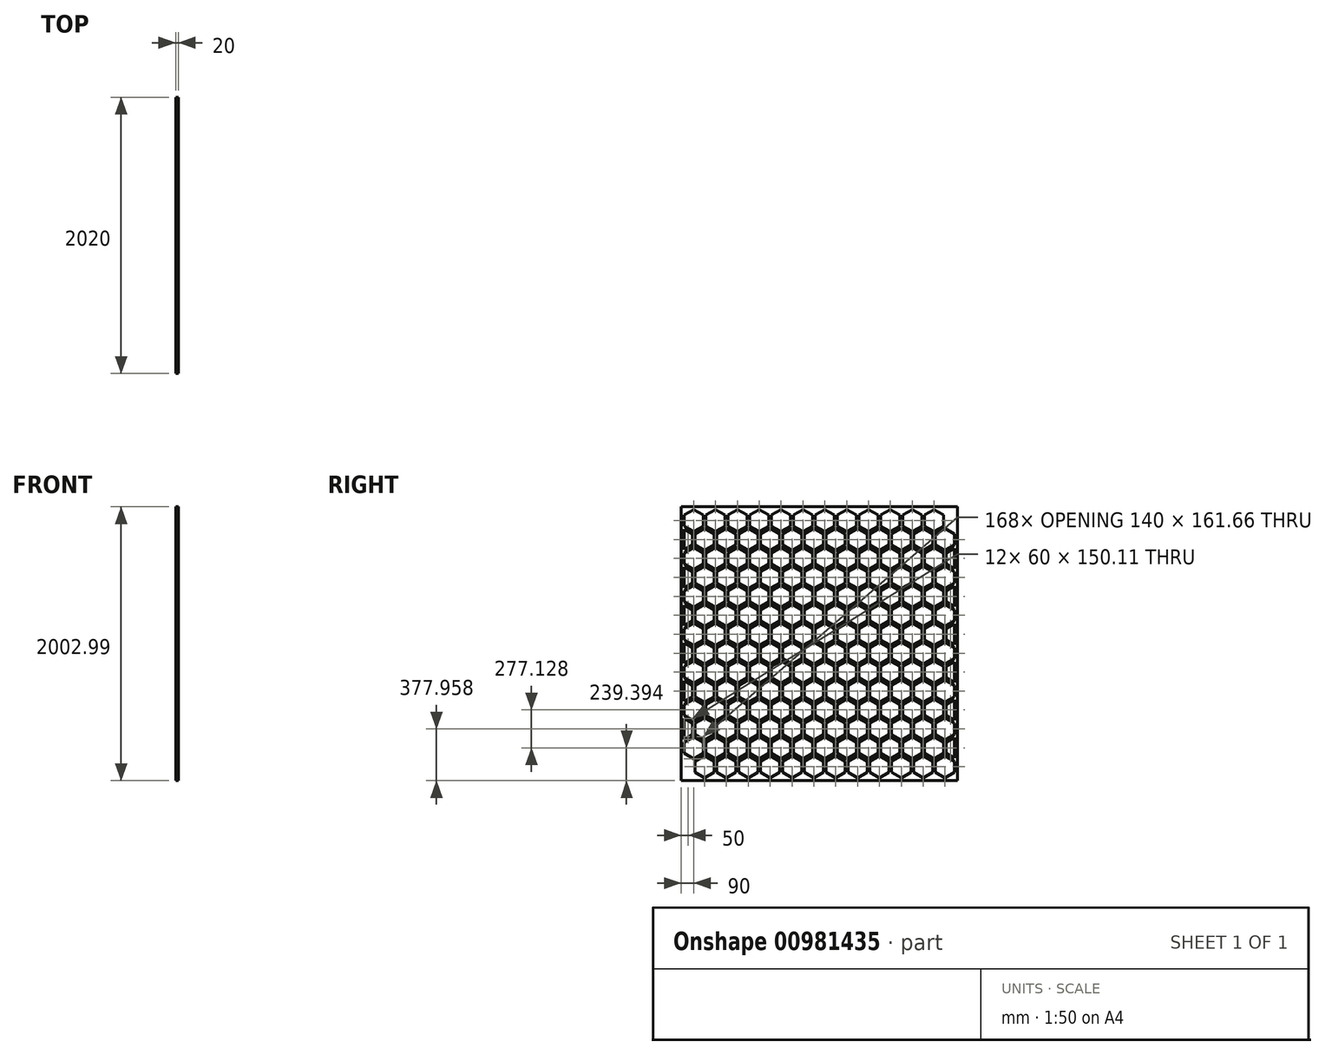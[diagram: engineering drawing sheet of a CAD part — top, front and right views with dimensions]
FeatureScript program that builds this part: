
annotation { "Feature Type Name" : "Feature", "Feature Type Description" : "" }
export const myFeature = defineFeature(function(context is Context, id is Id, definition is map)
    precondition{}
    {
        {
            var Q0;
            Q0=qCreatedBy(makeId("Right.planeOp"),FACE);
            var sketch = newSketch(context, id + "F0", { "sketchPlane" : qUnion([Q0])});
            skLineSegment(sketch, "E0", {"start": v(0, -80.83) * mm, "end": v(-70, -40.41) * mm});
            skLineSegment(sketch, "E1", {"start": v(-70, -40.41) * mm, "end": v(-70, 40.41) * mm});
            skLineSegment(sketch, "E2", {"start": v(-70, 40.41) * mm, "end": v(0, 80.83) * mm});
            skLineSegment(sketch, "E3", {"start": v(0, 80.83) * mm, "end": v(70, 40.41) * mm});
            skLineSegment(sketch, "E4", {"start": v(70, 40.41) * mm, "end": v(70, -40.41) * mm});
            skLineSegment(sketch, "E5", {"start": v(70, -40.41) * mm, "end": v(0, -80.83) * mm});
            skLineSegment(sketch, "E6.MirrorCS", {"start": v(10, 98.15) * mm, "end": v(80, 57.74) * mm});
            skLineSegment(sketch, "E7.MirrorCS", {"start": v(80, 57.74) * mm, "end": v(150, 98.15) * mm});
            skLineSegment(sketch, "E8.MirrorCS", {"start": v(80, 219.4) * mm, "end": v(10, 178.98) * mm});
            skLineSegment(sketch, "E9.MirrorCS", {"start": v(150, 178.98) * mm, "end": v(80, 219.4) * mm});
            skLineSegment(sketch, "E10.MirrorCS", {"start": v(150, 98.15) * mm, "end": v(150, 178.98) * mm});
            skLineSegment(sketch, "E11.MirrorCS", {"start": v(10, 178.98) * mm, "end": v(10, 98.15) * mm});
            skLineSegment(sketch, "E12.MirrorCS", {"start": v(160, -80.83) * mm, "end": v(230, -40.41) * mm});
            skLineSegment(sketch, "E13.MirrorCS", {"start": v(90, 40.41) * mm, "end": v(90, -40.41) * mm});
            skLineSegment(sketch, "E14.MirrorCS", {"start": v(230, 40.41) * mm, "end": v(160, 80.83) * mm});
            skLineSegment(sketch, "E15.MirrorCS", {"start": v(230, -40.41) * mm, "end": v(230, 40.41) * mm});
            skLineSegment(sketch, "E16.MirrorCS", {"start": v(160, 80.83) * mm, "end": v(90, 40.41) * mm});
            skLineSegment(sketch, "E17.MirrorCS", {"start": v(90, -40.41) * mm, "end": v(160, -80.83) * mm});
            skLineSegment(sketch, "E18.MirrorCS", {"start": v(410, 40.41) * mm, "end": v(410, -40.41) * mm});
            skLineSegment(sketch, "E19.MirrorCS", {"start": v(400, 57.74) * mm, "end": v(330, 98.15) * mm});
            skLineSegment(sketch, "E20.MirrorCS", {"start": v(320, 80.83) * mm, "end": v(390, 40.41) * mm});
            skLineSegment(sketch, "E21.MirrorCS", {"start": v(480, 80.83) * mm, "end": v(410, 40.41) * mm});
            skLineSegment(sketch, "E22.MirrorCS", {"start": v(320, -80.83) * mm, "end": v(250, -40.41) * mm});
            skLineSegment(sketch, "E23.MirrorCS", {"start": v(390, 40.41) * mm, "end": v(390, -40.41) * mm});
            skLineSegment(sketch, "E24.MirrorCS", {"start": v(250, -40.41) * mm, "end": v(250, 40.41) * mm});
            skLineSegment(sketch, "E25.MirrorCS", {"start": v(480, -80.83) * mm, "end": v(550, -40.41) * mm});
            skLineSegment(sketch, "E26.MirrorCS", {"start": v(330, 178.98) * mm, "end": v(400, 219.4) * mm});
            skLineSegment(sketch, "E27.MirrorCS", {"start": v(550, 40.41) * mm, "end": v(480, 80.83) * mm});
            skLineSegment(sketch, "E28.MirrorCS", {"start": v(470, 178.98) * mm, "end": v(470, 98.15) * mm});
            skLineSegment(sketch, "E29.MirrorCS", {"start": v(550, -40.41) * mm, "end": v(550, 40.41) * mm});
            skLineSegment(sketch, "E30.MirrorCS", {"start": v(390, -40.41) * mm, "end": v(320, -80.83) * mm});
            skLineSegment(sketch, "E31.MirrorCS", {"start": v(410, -40.41) * mm, "end": v(480, -80.83) * mm});
            skLineSegment(sketch, "E32.MirrorCS", {"start": v(250, 40.41) * mm, "end": v(320, 80.83) * mm});
            skLineSegment(sketch, "E33.MirrorCS", {"start": v(470, 98.15) * mm, "end": v(400, 57.74) * mm});
            skLineSegment(sketch, "E34.MirrorCS", {"start": v(330, 98.15) * mm, "end": v(330, 178.98) * mm});
            skLineSegment(sketch, "E35.MirrorCS", {"start": v(400, 219.4) * mm, "end": v(470, 178.98) * mm});
            skLineSegment(sketch, "E36.MirrorCS", {"start": v(1120, -80.83) * mm, "end": v(1190, -40.41) * mm});
            skLineSegment(sketch, "E37.MirrorCS", {"start": v(870, 40.41) * mm, "end": v(800, 80.83) * mm});
            skLineSegment(sketch, "E38.MirrorCS", {"start": v(800, 80.83) * mm, "end": v(730, 40.41) * mm});
            skLineSegment(sketch, "E39.MirrorCS", {"start": v(640, 80.83) * mm, "end": v(710, 40.41) * mm});
            skLineSegment(sketch, "E40.MirrorCS", {"start": v(790, 178.98) * mm, "end": v(720, 219.4) * mm});
            skLineSegment(sketch, "E41.MirrorCS", {"start": v(960, -80.83) * mm, "end": v(890, -40.41) * mm});
            skLineSegment(sketch, "E42.MirrorCS", {"start": v(570, 40.41) * mm, "end": v(640, 80.83) * mm});
            skLineSegment(sketch, "E43.MirrorCS", {"start": v(1120, 80.83) * mm, "end": v(1050, 40.41) * mm});
            skLineSegment(sketch, "E44.MirrorCS", {"start": v(970, 178.98) * mm, "end": v(1040, 219.4) * mm});
            skLineSegment(sketch, "E45.MirrorCS", {"start": v(650, 98.15) * mm, "end": v(720, 57.74) * mm});
            skLineSegment(sketch, "E46.MirrorCS", {"start": v(710, 40.41) * mm, "end": v(710, -40.41) * mm});
            skLineSegment(sketch, "E47.MirrorCS", {"start": v(1030, 40.41) * mm, "end": v(1030, -40.41) * mm});
            skLineSegment(sketch, "E48.MirrorCS", {"start": v(720, 219.4) * mm, "end": v(650, 178.98) * mm});
            skLineSegment(sketch, "E49.MirrorCS", {"start": v(890, -40.41) * mm, "end": v(890, 40.41) * mm});
            skLineSegment(sketch, "E50.MirrorCS", {"start": v(570, -40.41) * mm, "end": v(570, 40.41) * mm});
            skLineSegment(sketch, "E51.MirrorCS", {"start": v(1110, 98.15) * mm, "end": v(1040, 57.74) * mm});
            skLineSegment(sketch, "E52.MirrorCS", {"start": v(870, -40.41) * mm, "end": v(870, 40.41) * mm});
            skLineSegment(sketch, "E53.MirrorCS", {"start": v(1040, 57.74) * mm, "end": v(970, 98.15) * mm});
            skLineSegment(sketch, "E54.MirrorCS", {"start": v(890, 40.41) * mm, "end": v(960, 80.83) * mm});
            skLineSegment(sketch, "E55.MirrorCS", {"start": v(970, 98.15) * mm, "end": v(970, 178.98) * mm});
            skLineSegment(sketch, "E56.MirrorCS", {"start": v(730, -40.41) * mm, "end": v(800, -80.83) * mm});
            skLineSegment(sketch, "E57.MirrorCS", {"start": v(1110, 178.98) * mm, "end": v(1110, 98.15) * mm});
            skLineSegment(sketch, "E58.MirrorCS", {"start": v(790, 98.15) * mm, "end": v(790, 178.98) * mm});
            skLineSegment(sketch, "E59.MirrorCS", {"start": v(650, 178.98) * mm, "end": v(650, 98.15) * mm});
            skLineSegment(sketch, "E60.MirrorCS", {"start": v(1190, -40.41) * mm, "end": v(1190, 40.41) * mm});
            skLineSegment(sketch, "E61.MirrorCS", {"start": v(1190, 40.41) * mm, "end": v(1120, 80.83) * mm});
            skLineSegment(sketch, "E62.MirrorCS", {"start": v(960, 80.83) * mm, "end": v(1030, 40.41) * mm});
            skLineSegment(sketch, "E63.MirrorCS", {"start": v(710, -40.41) * mm, "end": v(640, -80.83) * mm});
            skLineSegment(sketch, "E64.MirrorCS", {"start": v(1030, -40.41) * mm, "end": v(960, -80.83) * mm});
            skLineSegment(sketch, "E65.MirrorCS", {"start": v(640, -80.83) * mm, "end": v(570, -40.41) * mm});
            skLineSegment(sketch, "E66.MirrorCS", {"start": v(730, 40.41) * mm, "end": v(730, -40.41) * mm});
            skLineSegment(sketch, "E67.MirrorCS", {"start": v(1050, -40.41) * mm, "end": v(1120, -80.83) * mm});
            skLineSegment(sketch, "E68.MirrorCS", {"start": v(720, 57.74) * mm, "end": v(790, 98.15) * mm});
            skLineSegment(sketch, "E69.MirrorCS", {"start": v(800, -80.83) * mm, "end": v(870, -40.41) * mm});
            skLineSegment(sketch, "E70.MirrorCS", {"start": v(1040, 219.4) * mm, "end": v(1110, 178.98) * mm});
            skLineSegment(sketch, "E71.MirrorCS", {"start": v(1050, 40.41) * mm, "end": v(1050, -40.41) * mm});
            skLineSegment(sketch, "E72.MirrorCS", {"start": v(-640, -80.83) * mm, "end": v(-710, -40.41) * mm});
            skLineSegment(sketch, "E73.MirrorCS", {"start": v(-710, 40.41) * mm, "end": v(-640, 80.83) * mm});
            skLineSegment(sketch, "E74.MirrorCS", {"start": v(-710, -40.41) * mm, "end": v(-710, 40.41) * mm});
            skLineSegment(sketch, "E75.MirrorCS", {"start": v(-160, 80.83) * mm, "end": v(-230, 40.41) * mm});
            skLineSegment(sketch, "E76.MirrorCS", {"start": v(-160, -80.83) * mm, "end": v(-90, -40.41) * mm});
            skLineSegment(sketch, "E77.MirrorCS", {"start": v(-250, -40.41) * mm, "end": v(-320, -80.83) * mm});
            skLineSegment(sketch, "E78.MirrorCS", {"start": v(-480, 80.83) * mm, "end": v(-550, 40.41) * mm});
            skLineSegment(sketch, "E79.MirrorCS", {"start": v(-490, 178.98) * mm, "end": v(-560, 219.4) * mm});
            skLineSegment(sketch, "E80.MirrorCS", {"start": v(-630, 98.15) * mm, "end": v(-560, 57.74) * mm});
            skLineSegment(sketch, "E81.MirrorCS", {"start": v(-570, -40.41) * mm, "end": v(-640, -80.83) * mm});
            skLineSegment(sketch, "E82.MirrorCS", {"start": v(-90, -40.41) * mm, "end": v(-90, 40.41) * mm});
            skLineSegment(sketch, "E83.MirrorCS", {"start": v(-630, 178.98) * mm, "end": v(-630, 98.15) * mm});
            skLineSegment(sketch, "E84.MirrorCS", {"start": v(-320, -80.83) * mm, "end": v(-390, -40.41) * mm});
            skLineSegment(sketch, "E85.MirrorCS", {"start": v(-480, -80.83) * mm, "end": v(-410, -40.41) * mm});
            skLineSegment(sketch, "E86.MirrorCS", {"start": v(-490, 98.15) * mm, "end": v(-490, 178.98) * mm});
            skLineSegment(sketch, "E87.MirrorCS", {"start": v(-570, 40.41) * mm, "end": v(-570, -40.41) * mm});
            skLineSegment(sketch, "E88.MirrorCS", {"start": v(-410, 40.41) * mm, "end": v(-480, 80.83) * mm});
            skLineSegment(sketch, "E89.MirrorCS", {"start": v(-170, 178.98) * mm, "end": v(-170, 98.15) * mm});
            skLineSegment(sketch, "E90.MirrorCS", {"start": v(-310, 178.98) * mm, "end": v(-240, 219.4) * mm});
            skLineSegment(sketch, "E91.MirrorCS", {"start": v(-230, 40.41) * mm, "end": v(-230, -40.41) * mm});
            skLineSegment(sketch, "E92.MirrorCS", {"start": v(-550, 40.41) * mm, "end": v(-550, -40.41) * mm});
            skLineSegment(sketch, "E93.MirrorCS", {"start": v(-390, 40.41) * mm, "end": v(-320, 80.83) * mm});
            skLineSegment(sketch, "E94.MirrorCS", {"start": v(-240, 219.4) * mm, "end": v(-170, 178.98) * mm});
            skLineSegment(sketch, "E95.MirrorCS", {"start": v(-560, 57.74) * mm, "end": v(-490, 98.15) * mm});
            skLineSegment(sketch, "E96.MirrorCS", {"start": v(-550, -40.41) * mm, "end": v(-480, -80.83) * mm});
            skLineSegment(sketch, "E97.MirrorCS", {"start": v(-250, 40.41) * mm, "end": v(-250, -40.41) * mm});
            skLineSegment(sketch, "E98.MirrorCS", {"start": v(-90, 40.41) * mm, "end": v(-160, 80.83) * mm});
            skLineSegment(sketch, "E99.MirrorCS", {"start": v(-230, -40.41) * mm, "end": v(-160, -80.83) * mm});
            skLineSegment(sketch, "E100.MirrorCS", {"start": v(-240, 57.74) * mm, "end": v(-310, 98.15) * mm});
            skLineSegment(sketch, "E101.MirrorCS", {"start": v(-310, 98.15) * mm, "end": v(-310, 178.98) * mm});
            skLineSegment(sketch, "E102.MirrorCS", {"start": v(-390, -40.41) * mm, "end": v(-390, 40.41) * mm});
            skLineSegment(sketch, "E103.MirrorCS", {"start": v(-170, 98.15) * mm, "end": v(-240, 57.74) * mm});
            skLineSegment(sketch, "E104.MirrorCS", {"start": v(-320, 80.83) * mm, "end": v(-250, 40.41) * mm});
            skLineSegment(sketch, "E105.MirrorCS", {"start": v(-560, 219.4) * mm, "end": v(-630, 178.98) * mm});
            skLineSegment(sketch, "E106.MirrorCS", {"start": v(-640, 80.83) * mm, "end": v(-570, 40.41) * mm});
            skLineSegment(sketch, "E107.MirrorCS", {"start": v(-410, -40.41) * mm, "end": v(-410, 40.41) * mm});
            skLineSegment(sketch, "E108.MirrorCS", {"start": v(-400, 57.74) * mm, "end": v(-470, 98.15) * mm});
            skLineSegment(sketch, "E109.MirrorCS", {"start": v(-330, 98.15) * mm, "end": v(-400, 57.74) * mm});
            skLineSegment(sketch, "E110.MirrorCS", {"start": v(-400, 219.4) * mm, "end": v(-330, 178.98) * mm});
            skLineSegment(sketch, "E111.MirrorCS", {"start": v(-470, 98.15) * mm, "end": v(-470, 178.98) * mm});
            skLineSegment(sketch, "E112.MirrorCS", {"start": v(-470, 178.98) * mm, "end": v(-400, 219.4) * mm});
            skLineSegment(sketch, "E113.MirrorCS", {"start": v(-330, 178.98) * mm, "end": v(-330, 98.15) * mm});
            skLineSegment(sketch, "E114.MirrorCS", {"start": v(310, 178.98) * mm, "end": v(310, 98.15) * mm});
            skLineSegment(sketch, "E115.MirrorCS", {"start": v(240, 219.4) * mm, "end": v(310, 178.98) * mm});
            skLineSegment(sketch, "E116.MirrorCS", {"start": v(240, 57.74) * mm, "end": v(170, 98.15) * mm});
            skLineSegment(sketch, "E117.MirrorCS", {"start": v(310, 98.15) * mm, "end": v(240, 57.74) * mm});
            skLineSegment(sketch, "E118.MirrorCS", {"start": v(170, 178.98) * mm, "end": v(240, 219.4) * mm});
            skLineSegment(sketch, "E119.MirrorCS", {"start": v(170, 98.15) * mm, "end": v(170, 178.98) * mm});
            skLineSegment(sketch, "E120.MirrorCS", {"start": v(-10, 98.15) * mm, "end": v(-10, 178.98) * mm});
            skLineSegment(sketch, "E121.MirrorCS", {"start": v(-80, 57.74) * mm, "end": v(-10, 98.15) * mm});
            skLineSegment(sketch, "E122.MirrorCS", {"start": v(-150, 98.15) * mm, "end": v(-80, 57.74) * mm});
            skLineSegment(sketch, "E123.MirrorCS", {"start": v(-150, 178.98) * mm, "end": v(-150, 98.15) * mm});
            skLineSegment(sketch, "E124.MirrorCS", {"start": v(-80, 219.4) * mm, "end": v(-150, 178.98) * mm});
            skLineSegment(sketch, "E125.MirrorCS", {"start": v(-10, 178.98) * mm, "end": v(-80, 219.4) * mm});
            skLineSegment(sketch, "E126.MirrorCS", {"start": v(-790, 178.98) * mm, "end": v(-790, 98.15) * mm});
            skLineSegment(sketch, "E127.MirrorCS", {"start": v(-720, 219.4) * mm, "end": v(-790, 178.98) * mm});
            skLineSegment(sketch, "E128.MirrorCS", {"start": v(-650, 178.98) * mm, "end": v(-720, 219.4) * mm});
            skLineSegment(sketch, "E129.MirrorCS", {"start": v(-650, 98.15) * mm, "end": v(-650, 178.98) * mm});
            skLineSegment(sketch, "E130.MirrorCS", {"start": v(-720, 57.74) * mm, "end": v(-650, 98.15) * mm});
            skLineSegment(sketch, "E131.MirrorCS", {"start": v(-790, 98.15) * mm, "end": v(-720, 57.74) * mm});
            skLineSegment(sketch, "E132.MirrorCS", {"start": v(1130, 98.15) * mm, "end": v(1190, 63.5) * mm});
            skLineSegment(sketch, "E133.MirrorCS", {"start": v(1130, 178.98) * mm, "end": v(1130, 98.15) * mm});
            skLineSegment(sketch, "E134.MirrorCS", {"start": v(1190, 213.62) * mm, "end": v(1130, 178.98) * mm});
            skLineSegment(sketch, "E135.MirrorCS", {"start": v(950, 178.98) * mm, "end": v(950, 98.15) * mm});
            skLineSegment(sketch, "E136.MirrorCS", {"start": v(880, 219.4) * mm, "end": v(950, 178.98) * mm});
            skLineSegment(sketch, "E137.MirrorCS", {"start": v(950, 98.15) * mm, "end": v(880, 57.74) * mm});
            skLineSegment(sketch, "E138.MirrorCS", {"start": v(880, 57.74) * mm, "end": v(810, 98.15) * mm});
            skLineSegment(sketch, "E139.MirrorCS", {"start": v(810, 98.15) * mm, "end": v(810, 178.98) * mm});
            skLineSegment(sketch, "E140.MirrorCS", {"start": v(810, 178.98) * mm, "end": v(880, 219.4) * mm});
            skLineSegment(sketch, "E141.MirrorCS", {"start": v(490, 98.15) * mm, "end": v(560, 57.74) * mm});
            skLineSegment(sketch, "E142.MirrorCS", {"start": v(560, 57.74) * mm, "end": v(630, 98.15) * mm});
            skLineSegment(sketch, "E143.MirrorCS", {"start": v(630, 98.15) * mm, "end": v(630, 178.98) * mm});
            skLineSegment(sketch, "E144.MirrorCS", {"start": v(630, 178.98) * mm, "end": v(560, 219.4) * mm});
            skLineSegment(sketch, "E145.MirrorCS", {"start": v(560, 219.4) * mm, "end": v(490, 178.98) * mm});
            skLineSegment(sketch, "E146.MirrorCS", {"start": v(490, 178.98) * mm, "end": v(490, 98.15) * mm});
            skLineSegment(sketch, "E147.MirrorCS", {"start": v(0, 357.96) * mm, "end": v(-70, 317.54) * mm});
            skLineSegment(sketch, "E148.MirrorCS", {"start": v(0, 196.3) * mm, "end": v(70, 236.71) * mm});
            skLineSegment(sketch, "E149.MirrorCS", {"start": v(-70, 236.71) * mm, "end": v(0, 196.3) * mm});
            skLineSegment(sketch, "E150.MirrorCS", {"start": v(-170, 178.98) * mm, "end": v(-240, 219.4) * mm});
            skLineSegment(sketch, "E151.MirrorCS", {"start": v(640, 357.96) * mm, "end": v(570, 317.54) * mm});
            skLineSegment(sketch, "E152.MirrorCS", {"start": v(-80, 219.4) * mm, "end": v(-10, 178.98) * mm});
            skLineSegment(sketch, "E153.MirrorCS", {"start": v(560, 219.4) * mm, "end": v(630, 178.98) * mm});
            skLineSegment(sketch, "E154.MirrorCS", {"start": v(390, 236.71) * mm, "end": v(390, 317.54) * mm});
            skLineSegment(sketch, "E155.MirrorCS", {"start": v(10, 178.98) * mm, "end": v(80, 219.4) * mm});
            skLineSegment(sketch, "E156.MirrorCS", {"start": v(-250, 236.71) * mm, "end": v(-250, 317.54) * mm});
            skLineSegment(sketch, "E157.MirrorCS", {"start": v(710, 236.71) * mm, "end": v(710, 317.54) * mm});
            skLineSegment(sketch, "E158.MirrorCS", {"start": v(240, 219.4) * mm, "end": v(170, 178.98) * mm});
            skLineSegment(sketch, "E159.MirrorCS", {"start": v(-150, 178.98) * mm, "end": v(-80, 219.4) * mm});
            skLineSegment(sketch, "E160.MirrorCS", {"start": v(-400, 219.4) * mm, "end": v(-470, 178.98) * mm});
            skLineSegment(sketch, "E161.MirrorCS", {"start": v(410, 236.71) * mm, "end": v(410, 317.54) * mm});
            skLineSegment(sketch, "E162.MirrorCS", {"start": v(640, 196.3) * mm, "end": v(710, 236.71) * mm});
            skLineSegment(sketch, "E163.MirrorCS", {"start": v(550, 236.71) * mm, "end": v(480, 196.3) * mm});
            skLineSegment(sketch, "E164.MirrorCS", {"start": v(-240, 219.4) * mm, "end": v(-310, 178.98) * mm});
            skLineSegment(sketch, "E165.MirrorCS", {"start": v(480, 357.96) * mm, "end": v(550, 317.54) * mm});
            skLineSegment(sketch, "E166.MirrorCS", {"start": v(570, 236.71) * mm, "end": v(640, 196.3) * mm});
            skLineSegment(sketch, "E167.MirrorCS", {"start": v(-480, 196.3) * mm, "end": v(-550, 236.71) * mm});
            skLineSegment(sketch, "E168.MirrorCS", {"start": v(950, 178.98) * mm, "end": v(880, 219.4) * mm});
            skLineSegment(sketch, "E169.MirrorCS", {"start": v(-480, 357.96) * mm, "end": v(-410, 317.54) * mm});
            skLineSegment(sketch, "E170.MirrorCS", {"start": v(-410, 317.54) * mm, "end": v(-410, 236.71) * mm});
            skLineSegment(sketch, "E171.MirrorCS", {"start": v(-560, 219.4) * mm, "end": v(-490, 178.98) * mm});
            skLineSegment(sketch, "E172.MirrorCS", {"start": v(-550, 317.54) * mm, "end": v(-480, 357.96) * mm});
            skLineSegment(sketch, "E173.MirrorCS", {"start": v(480, 196.3) * mm, "end": v(410, 236.71) * mm});
            skLineSegment(sketch, "E174.MirrorCS", {"start": v(320, 196.3) * mm, "end": v(390, 236.71) * mm});
            skLineSegment(sketch, "E175.MirrorCS", {"start": v(320, 357.96) * mm, "end": v(250, 317.54) * mm});
            skLineSegment(sketch, "E176.MirrorCS", {"start": v(90, 236.71) * mm, "end": v(90, 317.54) * mm});
            skLineSegment(sketch, "E177.MirrorCS", {"start": v(80, 219.4) * mm, "end": v(150, 178.98) * mm});
            skLineSegment(sketch, "E178.MirrorCS", {"start": v(960, 196.3) * mm, "end": v(1030, 236.71) * mm});
            skLineSegment(sketch, "E179.MirrorCS", {"start": v(-230, 317.54) * mm, "end": v(-160, 357.96) * mm});
            skLineSegment(sketch, "E180.MirrorCS", {"start": v(400, 219.4) * mm, "end": v(330, 178.98) * mm});
            skLineSegment(sketch, "E181.MirrorCS", {"start": v(160, 357.96) * mm, "end": v(230, 317.54) * mm});
            skLineSegment(sketch, "E182.MirrorCS", {"start": v(-390, 317.54) * mm, "end": v(-390, 236.71) * mm});
            skLineSegment(sketch, "E183.MirrorCS", {"start": v(650, 178.98) * mm, "end": v(720, 219.4) * mm});
            skLineSegment(sketch, "E184.MirrorCS", {"start": v(-90, 236.71) * mm, "end": v(-160, 196.3) * mm});
            skLineSegment(sketch, "E185.MirrorCS", {"start": v(-330, 178.98) * mm, "end": v(-400, 219.4) * mm});
            skLineSegment(sketch, "E186.MirrorCS", {"start": v(-640, 196.3) * mm, "end": v(-570, 236.71) * mm});
            skLineSegment(sketch, "E187.MirrorCS", {"start": v(1120, 196.3) * mm, "end": v(1050, 236.71) * mm});
            skLineSegment(sketch, "E188.MirrorCS", {"start": v(1030, 317.54) * mm, "end": v(960, 357.96) * mm});
            skLineSegment(sketch, "E189.MirrorCS", {"start": v(160, 196.3) * mm, "end": v(90, 236.71) * mm});
            skLineSegment(sketch, "E190.MirrorCS", {"start": v(470, 178.98) * mm, "end": v(400, 219.4) * mm});
            skLineSegment(sketch, "E191.MirrorCS", {"start": v(880, 219.4) * mm, "end": v(810, 178.98) * mm});
            skLineSegment(sketch, "E192.MirrorCS", {"start": v(310, 178.98) * mm, "end": v(240, 219.4) * mm});
            skLineSegment(sketch, "E193.MirrorCS", {"start": v(-730, 236.71) * mm, "end": v(-790, 202.07) * mm});
            skLineSegment(sketch, "E194.MirrorCS", {"start": v(-390, 236.71) * mm, "end": v(-320, 196.3) * mm});
            skLineSegment(sketch, "E195.MirrorCS", {"start": v(-410, 236.71) * mm, "end": v(-480, 196.3) * mm});
            skLineSegment(sketch, "E196.MirrorCS", {"start": v(-320, 196.3) * mm, "end": v(-250, 236.71) * mm});
            skLineSegment(sketch, "E197.MirrorCS", {"start": v(-730, 317.54) * mm, "end": v(-730, 236.71) * mm});
            skLineSegment(sketch, "E198.MirrorCS", {"start": v(-710, 236.71) * mm, "end": v(-640, 196.3) * mm});
            skLineSegment(sketch, "E199.MirrorCS", {"start": v(1190, 236.71) * mm, "end": v(1120, 196.3) * mm});
            skLineSegment(sketch, "E200.MirrorCS", {"start": v(230, 317.54) * mm, "end": v(230, 236.71) * mm});
            skLineSegment(sketch, "E201.MirrorCS", {"start": v(-160, 196.3) * mm, "end": v(-230, 236.71) * mm});
            skLineSegment(sketch, "E202.MirrorCS", {"start": v(1190, 317.54) * mm, "end": v(1190, 236.71) * mm});
            skLineSegment(sketch, "E203.MirrorCS", {"start": v(250, 236.71) * mm, "end": v(320, 196.3) * mm});
            skLineSegment(sketch, "E204.MirrorCS", {"start": v(1130, 178.98) * mm, "end": v(1190, 213.62) * mm});
            skLineSegment(sketch, "E205.MirrorCS", {"start": v(720, 219.4) * mm, "end": v(790, 178.98) * mm});
            skLineSegment(sketch, "E206.MirrorCS", {"start": v(870, 236.71) * mm, "end": v(800, 196.3) * mm});
            skLineSegment(sketch, "E207.MirrorCS", {"start": v(410, 317.54) * mm, "end": v(480, 357.96) * mm});
            skLineSegment(sketch, "E208.MirrorCS", {"start": v(730, 317.54) * mm, "end": v(800, 357.96) * mm});
            skLineSegment(sketch, "E209.MirrorCS", {"start": v(-570, 317.54) * mm, "end": v(-640, 357.96) * mm});
            skLineSegment(sketch, "E210.MirrorCS", {"start": v(-230, 236.71) * mm, "end": v(-230, 317.54) * mm});
            skLineSegment(sketch, "E211.MirrorCS", {"start": v(1120, 357.96) * mm, "end": v(1190, 317.54) * mm});
            skLineSegment(sketch, "E212.MirrorCS", {"start": v(1050, 236.71) * mm, "end": v(1050, 317.54) * mm});
            skLineSegment(sketch, "E213.MirrorCS", {"start": v(730, 236.71) * mm, "end": v(730, 317.54) * mm});
            skLineSegment(sketch, "E214.MirrorCS", {"start": v(-790, 352.18) * mm, "end": v(-730, 317.54) * mm});
            skLineSegment(sketch, "E215.MirrorCS", {"start": v(-250, 317.54) * mm, "end": v(-320, 357.96) * mm});
            skLineSegment(sketch, "E216.MirrorCS", {"start": v(-570, 236.71) * mm, "end": v(-570, 317.54) * mm});
            skLineSegment(sketch, "E217.MirrorCS", {"start": v(-640, 357.96) * mm, "end": v(-710, 317.54) * mm});
            skLineSegment(sketch, "E218.MirrorCS", {"start": v(1040, 219.4) * mm, "end": v(970, 178.98) * mm});
            skLineSegment(sketch, "E219.MirrorCS", {"start": v(-160, 357.96) * mm, "end": v(-90, 317.54) * mm});
            skLineSegment(sketch, "E220.MirrorCS", {"start": v(-710, 317.54) * mm, "end": v(-710, 236.71) * mm});
            skLineSegment(sketch, "E221.MirrorCS", {"start": v(800, 196.3) * mm, "end": v(730, 236.71) * mm});
            skLineSegment(sketch, "E222.MirrorCS", {"start": v(890, 317.54) * mm, "end": v(890, 236.71) * mm});
            skLineSegment(sketch, "E223.MirrorCS", {"start": v(550, 317.54) * mm, "end": v(550, 236.71) * mm});
            skLineSegment(sketch, "E224.MirrorCS", {"start": v(-90, 317.54) * mm, "end": v(-90, 236.71) * mm});
            skLineSegment(sketch, "E225.MirrorCS", {"start": v(-720, 219.4) * mm, "end": v(-650, 178.98) * mm});
            skLineSegment(sketch, "E226.MirrorCS", {"start": v(90, 317.54) * mm, "end": v(160, 357.96) * mm});
            skLineSegment(sketch, "E227.MirrorCS", {"start": v(1110, 178.98) * mm, "end": v(1040, 219.4) * mm});
            skLineSegment(sketch, "E228.MirrorCS", {"start": v(1030, 236.71) * mm, "end": v(1030, 317.54) * mm});
            skLineSegment(sketch, "E229.MirrorCS", {"start": v(250, 317.54) * mm, "end": v(250, 236.71) * mm});
            skLineSegment(sketch, "E230.MirrorCS", {"start": v(-790, 178.98) * mm, "end": v(-720, 219.4) * mm});
            skLineSegment(sketch, "E231.MirrorCS", {"start": v(-630, 178.98) * mm, "end": v(-560, 219.4) * mm});
            skLineSegment(sketch, "E232.MirrorCS", {"start": v(890, 236.71) * mm, "end": v(960, 196.3) * mm});
            skLineSegment(sketch, "E233.MirrorCS", {"start": v(230, 236.71) * mm, "end": v(160, 196.3) * mm});
            skLineSegment(sketch, "E234.MirrorCS", {"start": v(490, 178.98) * mm, "end": v(560, 219.4) * mm});
            skLineSegment(sketch, "E235.MirrorCS", {"start": v(1050, 317.54) * mm, "end": v(1120, 357.96) * mm});
            skLineSegment(sketch, "E236.MirrorCS", {"start": v(70, 317.54) * mm, "end": v(0, 357.96) * mm});
            skLineSegment(sketch, "E237.MirrorCS", {"start": v(870, 317.54) * mm, "end": v(870, 236.71) * mm});
            skLineSegment(sketch, "E238.MirrorCS", {"start": v(-550, 236.71) * mm, "end": v(-550, 317.54) * mm});
            skLineSegment(sketch, "E239.MirrorCS", {"start": v(-320, 357.96) * mm, "end": v(-390, 317.54) * mm});
            skLineSegment(sketch, "E240.MirrorCS", {"start": v(390, 317.54) * mm, "end": v(320, 357.96) * mm});
            skLineSegment(sketch, "E241.MirrorCS", {"start": v(570, 317.54) * mm, "end": v(570, 236.71) * mm});
            skLineSegment(sketch, "E242.MirrorCS", {"start": v(70, 236.71) * mm, "end": v(70, 317.54) * mm});
            skLineSegment(sketch, "E243.MirrorCS", {"start": v(960, 357.96) * mm, "end": v(890, 317.54) * mm});
            skLineSegment(sketch, "E244.MirrorCS", {"start": v(710, 317.54) * mm, "end": v(640, 357.96) * mm});
            skLineSegment(sketch, "E245.MirrorCS", {"start": v(800, 357.96) * mm, "end": v(870, 317.54) * mm});
            skLineSegment(sketch, "E246.MirrorCS", {"start": v(-70, 317.54) * mm, "end": v(-70, 236.71) * mm});
            skLineSegment(sketch, "E247.MirrorCS", {"start": v(1040, 334.86) * mm, "end": v(970, 375.28) * mm});
            skLineSegment(sketch, "E248.MirrorCS", {"start": v(80, 334.86) * mm, "end": v(150, 375.28) * mm});
            skLineSegment(sketch, "E249.MirrorCS", {"start": v(-240, 334.86) * mm, "end": v(-170, 375.28) * mm});
            skLineSegment(sketch, "E250.MirrorCS", {"start": v(0, 635.09) * mm, "end": v(-70, 594.67) * mm});
            skLineSegment(sketch, "E251.MirrorCS", {"start": v(1040, 334.86) * mm, "end": v(1110, 375.28) * mm});
            skLineSegment(sketch, "E252.MirrorCS", {"start": v(0, 473.43) * mm, "end": v(70, 513.84) * mm});
            skLineSegment(sketch, "E253.MirrorCS", {"start": v(-630, 375.28) * mm, "end": v(-560, 334.86) * mm});
            skLineSegment(sketch, "E254.MirrorCS", {"start": v(-720, 334.86) * mm, "end": v(-790, 375.28) * mm});
            skLineSegment(sketch, "E255.MirrorCS", {"start": v(720, 334.86) * mm, "end": v(650, 375.28) * mm});
            skLineSegment(sketch, "E256.MirrorCS", {"start": v(310, 375.28) * mm, "end": v(240, 334.86) * mm});
            skLineSegment(sketch, "E257.MirrorCS", {"start": v(470, 375.28) * mm, "end": v(400, 334.86) * mm});
            skLineSegment(sketch, "E258.MirrorCS", {"start": v(10, 375.28) * mm, "end": v(80, 334.86) * mm});
            skLineSegment(sketch, "E259.MirrorCS", {"start": v(-720, 334.86) * mm, "end": v(-650, 375.28) * mm});
            skLineSegment(sketch, "E260.MirrorCS", {"start": v(-150, 375.28) * mm, "end": v(-80, 334.86) * mm});
            skLineSegment(sketch, "E261.MirrorCS", {"start": v(-470, 375.28) * mm, "end": v(-400, 334.86) * mm});
            skLineSegment(sketch, "E262.MirrorCS", {"start": v(400, 334.86) * mm, "end": v(330, 375.28) * mm});
            skLineSegment(sketch, "E263.MirrorCS", {"start": v(170, 375.28) * mm, "end": v(240, 334.86) * mm});
            skLineSegment(sketch, "E264.MirrorCS", {"start": v(1130, 375.28) * mm, "end": v(1190, 340.64) * mm});
            skLineSegment(sketch, "E265.MirrorCS", {"start": v(-330, 375.28) * mm, "end": v(-400, 334.86) * mm});
            skLineSegment(sketch, "E266.MirrorCS", {"start": v(950, 375.28) * mm, "end": v(880, 334.86) * mm});
            skLineSegment(sketch, "E267.MirrorCS", {"start": v(880, 334.86) * mm, "end": v(810, 375.28) * mm});
            skLineSegment(sketch, "E268.MirrorCS", {"start": v(720, 334.86) * mm, "end": v(790, 375.28) * mm});
            skLineSegment(sketch, "E269.MirrorCS", {"start": v(-240, 334.86) * mm, "end": v(-310, 375.28) * mm});
            skLineSegment(sketch, "E270.MirrorCS", {"start": v(-560, 334.86) * mm, "end": v(-490, 375.28) * mm});
            skLineSegment(sketch, "E271.MirrorCS", {"start": v(560, 334.86) * mm, "end": v(490, 375.28) * mm});
            skLineSegment(sketch, "E272.MirrorCS", {"start": v(560, 334.86) * mm, "end": v(630, 375.28) * mm});
            skLineSegment(sketch, "E273.MirrorCS", {"start": v(-80, 334.86) * mm, "end": v(-10, 375.28) * mm});
            skLineSegment(sketch, "E274.MirrorCS", {"start": v(160, 473.43) * mm, "end": v(90, 513.84) * mm});
            skLineSegment(sketch, "E275.MirrorCS", {"start": v(1110, 375.28) * mm, "end": v(1110, 456.1) * mm});
            skLineSegment(sketch, "E276.MirrorCS", {"start": v(230, 513.84) * mm, "end": v(160, 473.43) * mm});
            skLineSegment(sketch, "E277.MirrorCS", {"start": v(-710, 594.67) * mm, "end": v(-710, 513.84) * mm});
            skLineSegment(sketch, "E278.MirrorCS", {"start": v(-170, 456.1) * mm, "end": v(-240, 496.52) * mm});
            skLineSegment(sketch, "E279.MirrorCS", {"start": v(390, 513.84) * mm, "end": v(390, 594.67) * mm});
            skLineSegment(sketch, "E280.MirrorCS", {"start": v(970, 375.28) * mm, "end": v(1040, 334.86) * mm});
            skLineSegment(sketch, "E281.MirrorCS", {"start": v(1130, 375.28) * mm, "end": v(1130, 456.1) * mm});
            skLineSegment(sketch, "E282.MirrorCS", {"start": v(710, 594.67) * mm, "end": v(640, 635.09) * mm});
            skLineSegment(sketch, "E283.MirrorCS", {"start": v(570, 513.84) * mm, "end": v(640, 473.43) * mm});
            skLineSegment(sketch, "E284.MirrorCS", {"start": v(1190, 594.67) * mm, "end": v(1190, 513.84) * mm});
            skLineSegment(sketch, "E285.MirrorCS", {"start": v(1050, 513.84) * mm, "end": v(1050, 594.67) * mm});
            skLineSegment(sketch, "E286.MirrorCS", {"start": v(870, 317.54) * mm, "end": v(800, 357.96) * mm});
            skLineSegment(sketch, "E287.MirrorCS", {"start": v(630, 375.28) * mm, "end": v(560, 334.86) * mm});
            skLineSegment(sketch, "E288.MirrorCS", {"start": v(90, 594.67) * mm, "end": v(160, 635.09) * mm});
            skLineSegment(sketch, "E289.MirrorCS", {"start": v(640, 357.96) * mm, "end": v(710, 317.54) * mm});
            skLineSegment(sketch, "E290.MirrorCS", {"start": v(-570, 513.84) * mm, "end": v(-570, 594.67) * mm});
            skLineSegment(sketch, "E291.MirrorCS", {"start": v(810, 375.28) * mm, "end": v(880, 334.86) * mm});
            skLineSegment(sketch, "E292.MirrorCS", {"start": v(-790, 375.28) * mm, "end": v(-720, 334.86) * mm});
            skLineSegment(sketch, "E293.MirrorCS", {"start": v(-320, 635.09) * mm, "end": v(-390, 594.67) * mm});
            skLineSegment(sketch, "E294.MirrorCS", {"start": v(-560, 334.86) * mm, "end": v(-630, 375.28) * mm});
            skLineSegment(sketch, "E295.MirrorCS", {"start": v(250, 594.67) * mm, "end": v(250, 513.84) * mm});
            skLineSegment(sketch, "E296.MirrorCS", {"start": v(310, 456.1) * mm, "end": v(240, 496.52) * mm});
            skLineSegment(sketch, "E297.MirrorCS", {"start": v(-790, 456.1) * mm, "end": v(-720, 496.52) * mm});
            skLineSegment(sketch, "E298.MirrorCS", {"start": v(800, 357.96) * mm, "end": v(730, 317.54) * mm});
            skLineSegment(sketch, "E299.MirrorCS", {"start": v(880, 334.86) * mm, "end": v(950, 375.28) * mm});
            skLineSegment(sketch, "E300.MirrorCS", {"start": v(-710, 317.54) * mm, "end": v(-640, 357.96) * mm});
            skLineSegment(sketch, "E301.MirrorCS", {"start": v(-10, 375.28) * mm, "end": v(-80, 334.86) * mm});
            skLineSegment(sketch, "E302.MirrorCS", {"start": v(-560, 496.52) * mm, "end": v(-490, 456.1) * mm});
            skLineSegment(sketch, "E303.MirrorCS", {"start": v(240, 334.86) * mm, "end": v(310, 375.28) * mm});
            skLineSegment(sketch, "E304.MirrorCS", {"start": v(800, 473.43) * mm, "end": v(730, 513.84) * mm});
            skLineSegment(sketch, "E305.MirrorCS", {"start": v(650, 375.28) * mm, "end": v(650, 456.1) * mm});
            skLineSegment(sketch, "E306.MirrorCS", {"start": v(-490, 375.28) * mm, "end": v(-560, 334.86) * mm});
            skLineSegment(sketch, "E307.MirrorCS", {"start": v(160, 635.09) * mm, "end": v(230, 594.67) * mm});
            skLineSegment(sketch, "E308.MirrorCS", {"start": v(960, 473.43) * mm, "end": v(1030, 513.84) * mm});
            skLineSegment(sketch, "E309.MirrorCS", {"start": v(160, 357.96) * mm, "end": v(90, 317.54) * mm});
            skLineSegment(sketch, "E310.MirrorCS", {"start": v(-310, 375.28) * mm, "end": v(-240, 334.86) * mm});
            skLineSegment(sketch, "E311.MirrorCS", {"start": v(890, 594.67) * mm, "end": v(890, 513.84) * mm});
            skLineSegment(sketch, "E312.MirrorCS", {"start": v(-170, 375.28) * mm, "end": v(-240, 334.86) * mm});
            skLineSegment(sketch, "E313.MirrorCS", {"start": v(-330, 375.28) * mm, "end": v(-330, 456.1) * mm});
            skLineSegment(sketch, "E314.MirrorCS", {"start": v(-790, 629.31) * mm, "end": v(-730, 594.67) * mm});
            skLineSegment(sketch, "E315.MirrorCS", {"start": v(790, 375.28) * mm, "end": v(720, 334.86) * mm});
            skLineSegment(sketch, "E316.MirrorCS", {"start": v(10, 375.28) * mm, "end": v(10, 456.1) * mm});
            skLineSegment(sketch, "E317.MirrorCS", {"start": v(-70, 594.67) * mm, "end": v(-70, 513.84) * mm});
            skLineSegment(sketch, "E318.MirrorCS", {"start": v(-400, 334.86) * mm, "end": v(-330, 375.28) * mm});
            skLineSegment(sketch, "E319.MirrorCS", {"start": v(320, 357.96) * mm, "end": v(390, 317.54) * mm});
            skLineSegment(sketch, "E320.MirrorCS", {"start": v(1120, 357.96) * mm, "end": v(1050, 317.54) * mm});
            skLineSegment(sketch, "E321.MirrorCS", {"start": v(-730, 513.84) * mm, "end": v(-790, 479.2) * mm});
            skLineSegment(sketch, "E322.MirrorCS", {"start": v(-480, 473.43) * mm, "end": v(-550, 513.84) * mm});
            skLineSegment(sketch, "E323.MirrorCS", {"start": v(170, 456.1) * mm, "end": v(170, 375.28) * mm});
            skLineSegment(sketch, "E324.MirrorCS", {"start": v(-320, 473.43) * mm, "end": v(-250, 513.84) * mm});
            skLineSegment(sketch, "E325.MirrorCS", {"start": v(1030, 594.67) * mm, "end": v(960, 635.09) * mm});
            skLineSegment(sketch, "E326.MirrorCS", {"start": v(410, 594.67) * mm, "end": v(480, 635.09) * mm});
            skLineSegment(sketch, "E327.MirrorCS", {"start": v(570, 317.54) * mm, "end": v(640, 357.96) * mm});
            skLineSegment(sketch, "E328.MirrorCS", {"start": v(-250, 594.67) * mm, "end": v(-320, 635.09) * mm});
            skLineSegment(sketch, "E329.MirrorCS", {"start": v(230, 594.67) * mm, "end": v(230, 513.84) * mm});
            skLineSegment(sketch, "E330.MirrorCS", {"start": v(-160, 635.09) * mm, "end": v(-90, 594.67) * mm});
            skLineSegment(sketch, "E331.MirrorCS", {"start": v(1040, 496.52) * mm, "end": v(970, 456.1) * mm});
            skLineSegment(sketch, "E332.MirrorCS", {"start": v(320, 635.09) * mm, "end": v(250, 594.67) * mm});
            skLineSegment(sketch, "E333.MirrorCS", {"start": v(-150, 375.28) * mm, "end": v(-150, 456.1) * mm});
            skLineSegment(sketch, "E334.MirrorCS", {"start": v(-70, 317.54) * mm, "end": v(0, 357.96) * mm});
            skLineSegment(sketch, "E335.MirrorCS", {"start": v(-70, 513.84) * mm, "end": v(0, 473.43) * mm});
            skLineSegment(sketch, "E336.MirrorCS", {"start": v(90, 513.84) * mm, "end": v(90, 594.67) * mm});
            skLineSegment(sketch, "E337.MirrorCS", {"start": v(730, 513.84) * mm, "end": v(730, 594.67) * mm});
            skLineSegment(sketch, "E338.MirrorCS", {"start": v(490, 375.28) * mm, "end": v(490, 456.1) * mm});
            skLineSegment(sketch, "E339.MirrorCS", {"start": v(810, 456.1) * mm, "end": v(810, 375.28) * mm});
            skLineSegment(sketch, "E340.MirrorCS", {"start": v(470, 375.28) * mm, "end": v(470, 456.1) * mm});
            skLineSegment(sketch, "E341.MirrorCS", {"start": v(-400, 334.86) * mm, "end": v(-470, 375.28) * mm});
            skLineSegment(sketch, "E342.MirrorCS", {"start": v(0, 357.96) * mm, "end": v(70, 317.54) * mm});
            skLineSegment(sketch, "E343.MirrorCS", {"start": v(-790, 375.28) * mm, "end": v(-790, 456.1) * mm});
            skLineSegment(sketch, "E344.MirrorCS", {"start": v(-730, 594.67) * mm, "end": v(-730, 513.84) * mm});
            skLineSegment(sketch, "E345.MirrorCS", {"start": v(-170, 375.28) * mm, "end": v(-170, 456.1) * mm});
            skLineSegment(sketch, "E346.MirrorCS", {"start": v(-550, 513.84) * mm, "end": v(-550, 594.67) * mm});
            skLineSegment(sketch, "E347.MirrorCS", {"start": v(-470, 456.1) * mm, "end": v(-470, 375.28) * mm});
            skLineSegment(sketch, "E348.MirrorCS", {"start": v(950, 375.28) * mm, "end": v(950, 456.1) * mm});
            skLineSegment(sketch, "E349.MirrorCS", {"start": v(240, 334.86) * mm, "end": v(170, 375.28) * mm});
            skLineSegment(sketch, "E350.MirrorCS", {"start": v(-480, 357.96) * mm, "end": v(-550, 317.54) * mm});
            skLineSegment(sketch, "E351.MirrorCS", {"start": v(470, 456.1) * mm, "end": v(400, 496.52) * mm});
            skLineSegment(sketch, "E352.MirrorCS", {"start": v(-490, 456.1) * mm, "end": v(-490, 375.28) * mm});
            skLineSegment(sketch, "E353.MirrorCS", {"start": v(-390, 513.84) * mm, "end": v(-320, 473.43) * mm});
            skLineSegment(sketch, "E354.MirrorCS", {"start": v(250, 317.54) * mm, "end": v(320, 357.96) * mm});
            skLineSegment(sketch, "E355.MirrorCS", {"start": v(970, 456.1) * mm, "end": v(970, 375.28) * mm});
            skLineSegment(sketch, "E356.MirrorCS", {"start": v(-250, 513.84) * mm, "end": v(-250, 594.67) * mm});
            skLineSegment(sketch, "E357.MirrorCS", {"start": v(-480, 635.09) * mm, "end": v(-410, 594.67) * mm});
            skLineSegment(sketch, "E358.MirrorCS", {"start": v(-90, 513.84) * mm, "end": v(-160, 473.43) * mm});
            skLineSegment(sketch, "E359.MirrorCS", {"start": v(870, 594.67) * mm, "end": v(870, 513.84) * mm});
            skLineSegment(sketch, "E360.MirrorCS", {"start": v(1120, 635.09) * mm, "end": v(1190, 594.67) * mm});
            skLineSegment(sketch, "E361.MirrorCS", {"start": v(320, 473.43) * mm, "end": v(390, 513.84) * mm});
            skLineSegment(sketch, "E362.MirrorCS", {"start": v(-80, 496.52) * mm, "end": v(-10, 456.1) * mm});
            skLineSegment(sketch, "E363.MirrorCS", {"start": v(-570, 594.67) * mm, "end": v(-640, 635.09) * mm});
            skLineSegment(sketch, "E364.MirrorCS", {"start": v(870, 513.84) * mm, "end": v(800, 473.43) * mm});
            skLineSegment(sketch, "E365.MirrorCS", {"start": v(-10, 456.1) * mm, "end": v(-10, 375.28) * mm});
            skLineSegment(sketch, "E366.MirrorCS", {"start": v(80, 334.86) * mm, "end": v(10, 375.28) * mm});
            skLineSegment(sketch, "E367.MirrorCS", {"start": v(-310, 456.1) * mm, "end": v(-310, 375.28) * mm});
            skLineSegment(sketch, "E368.MirrorCS", {"start": v(70, 594.67) * mm, "end": v(0, 635.09) * mm});
            skLineSegment(sketch, "E369.MirrorCS", {"start": v(480, 635.09) * mm, "end": v(550, 594.67) * mm});
            skLineSegment(sketch, "E370.MirrorCS", {"start": v(250, 513.84) * mm, "end": v(320, 473.43) * mm});
            skLineSegment(sketch, "E371.MirrorCS", {"start": v(570, 594.67) * mm, "end": v(570, 513.84) * mm});
            skLineSegment(sketch, "E372.MirrorCS", {"start": v(1030, 513.84) * mm, "end": v(1030, 594.67) * mm});
            skLineSegment(sketch, "E373.MirrorCS", {"start": v(-90, 594.67) * mm, "end": v(-90, 513.84) * mm});
            skLineSegment(sketch, "E374.MirrorCS", {"start": v(550, 594.67) * mm, "end": v(550, 513.84) * mm});
            skLineSegment(sketch, "E375.MirrorCS", {"start": v(960, 357.96) * mm, "end": v(1030, 317.54) * mm});
            skLineSegment(sketch, "E376.MirrorCS", {"start": v(80, 496.52) * mm, "end": v(150, 456.1) * mm});
            skLineSegment(sketch, "E377.MirrorCS", {"start": v(-640, 473.43) * mm, "end": v(-570, 513.84) * mm});
            skLineSegment(sketch, "E378.MirrorCS", {"start": v(-160, 473.43) * mm, "end": v(-230, 513.84) * mm});
            skLineSegment(sketch, "E379.MirrorCS", {"start": v(-320, 357.96) * mm, "end": v(-250, 317.54) * mm});
            skLineSegment(sketch, "E380.MirrorCS", {"start": v(1190, 340.64) * mm, "end": v(1130, 375.28) * mm});
            skLineSegment(sketch, "E381.MirrorCS", {"start": v(1130, 456.1) * mm, "end": v(1190, 490.75) * mm});
            skLineSegment(sketch, "E382.MirrorCS", {"start": v(640, 635.09) * mm, "end": v(570, 594.67) * mm});
            skLineSegment(sketch, "E383.MirrorCS", {"start": v(-650, 375.28) * mm, "end": v(-720, 334.86) * mm});
            skLineSegment(sketch, "E384.MirrorCS", {"start": v(-410, 317.54) * mm, "end": v(-480, 357.96) * mm});
            skLineSegment(sketch, "E385.MirrorCS", {"start": v(-550, 594.67) * mm, "end": v(-480, 635.09) * mm});
            skLineSegment(sketch, "E386.MirrorCS", {"start": v(-400, 496.52) * mm, "end": v(-470, 456.1) * mm});
            skLineSegment(sketch, "E387.MirrorCS", {"start": v(550, 513.84) * mm, "end": v(480, 473.43) * mm});
            skLineSegment(sketch, "E388.MirrorCS", {"start": v(150, 456.1) * mm, "end": v(150, 375.28) * mm});
            skLineSegment(sketch, "E389.MirrorCS", {"start": v(330, 375.28) * mm, "end": v(400, 334.86) * mm});
            skLineSegment(sketch, "E390.MirrorCS", {"start": v(-720, 496.52) * mm, "end": v(-650, 456.1) * mm});
            skLineSegment(sketch, "E391.MirrorCS", {"start": v(490, 456.1) * mm, "end": v(560, 496.52) * mm});
            skLineSegment(sketch, "E392.MirrorCS", {"start": v(800, 635.09) * mm, "end": v(870, 594.67) * mm});
            skLineSegment(sketch, "E393.MirrorCS", {"start": v(-240, 496.52) * mm, "end": v(-310, 456.1) * mm});
            skLineSegment(sketch, "E394.MirrorCS", {"start": v(-230, 594.67) * mm, "end": v(-160, 635.09) * mm});
            skLineSegment(sketch, "E395.MirrorCS", {"start": v(1190, 513.84) * mm, "end": v(1120, 473.43) * mm});
            skLineSegment(sketch, "E396.MirrorCS", {"start": v(720, 496.52) * mm, "end": v(790, 456.1) * mm});
            skLineSegment(sketch, "E397.MirrorCS", {"start": v(-390, 594.67) * mm, "end": v(-390, 513.84) * mm});
            skLineSegment(sketch, "E398.MirrorCS", {"start": v(-630, 375.28) * mm, "end": v(-630, 456.1) * mm});
            skLineSegment(sketch, "E399.MirrorCS", {"start": v(730, 594.67) * mm, "end": v(800, 635.09) * mm});
            skLineSegment(sketch, "E400.MirrorCS", {"start": v(-90, 317.54) * mm, "end": v(-160, 357.96) * mm});
            skLineSegment(sketch, "E401.MirrorCS", {"start": v(480, 357.96) * mm, "end": v(410, 317.54) * mm});
            skLineSegment(sketch, "E402.MirrorCS", {"start": v(390, 594.67) * mm, "end": v(320, 635.09) * mm});
            skLineSegment(sketch, "E403.MirrorCS", {"start": v(10, 456.1) * mm, "end": v(80, 496.52) * mm});
            skLineSegment(sketch, "E404.MirrorCS", {"start": v(890, 317.54) * mm, "end": v(960, 357.96) * mm});
            skLineSegment(sketch, "E405.MirrorCS", {"start": v(650, 375.28) * mm, "end": v(720, 334.86) * mm});
            skLineSegment(sketch, "E406.MirrorCS", {"start": v(490, 375.28) * mm, "end": v(560, 334.86) * mm});
            skLineSegment(sketch, "E407.MirrorCS", {"start": v(560, 496.52) * mm, "end": v(630, 456.1) * mm});
            skLineSegment(sketch, "E408.MirrorCS", {"start": v(-330, 456.1) * mm, "end": v(-400, 496.52) * mm});
            skLineSegment(sketch, "E409.MirrorCS", {"start": v(1190, 317.54) * mm, "end": v(1120, 357.96) * mm});
            skLineSegment(sketch, "E410.MirrorCS", {"start": v(70, 513.84) * mm, "end": v(70, 594.67) * mm});
            skLineSegment(sketch, "E411.MirrorCS", {"start": v(-410, 513.84) * mm, "end": v(-480, 473.43) * mm});
            skLineSegment(sketch, "E412.MirrorCS", {"start": v(-80, 334.86) * mm, "end": v(-150, 375.28) * mm});
            skLineSegment(sketch, "E413.MirrorCS", {"start": v(-390, 317.54) * mm, "end": v(-320, 357.96) * mm});
            skLineSegment(sketch, "E414.MirrorCS", {"start": v(1050, 594.67) * mm, "end": v(1120, 635.09) * mm});
            skLineSegment(sketch, "E415.MirrorCS", {"start": v(890, 513.84) * mm, "end": v(960, 473.43) * mm});
            skLineSegment(sketch, "E416.MirrorCS", {"start": v(150, 375.28) * mm, "end": v(80, 334.86) * mm});
            skLineSegment(sketch, "E417.MirrorCS", {"start": v(640, 473.43) * mm, "end": v(710, 513.84) * mm});
            skLineSegment(sketch, "E418.MirrorCS", {"start": v(-630, 456.1) * mm, "end": v(-560, 496.52) * mm});
            skLineSegment(sketch, "E419.MirrorCS", {"start": v(790, 456.1) * mm, "end": v(790, 375.28) * mm});
            skLineSegment(sketch, "E420.MirrorCS", {"start": v(-160, 357.96) * mm, "end": v(-230, 317.54) * mm});
            skLineSegment(sketch, "E421.MirrorCS", {"start": v(310, 375.28) * mm, "end": v(310, 456.1) * mm});
            skLineSegment(sketch, "E422.MirrorCS", {"start": v(-730, 317.54) * mm, "end": v(-790, 352.18) * mm});
            skLineSegment(sketch, "E423.MirrorCS", {"start": v(-150, 456.1) * mm, "end": v(-80, 496.52) * mm});
            skLineSegment(sketch, "E424.MirrorCS", {"start": v(1110, 375.28) * mm, "end": v(1040, 334.86) * mm});
            skLineSegment(sketch, "E425.MirrorCS", {"start": v(550, 317.54) * mm, "end": v(480, 357.96) * mm});
            skLineSegment(sketch, "E426.MirrorCS", {"start": v(-650, 456.1) * mm, "end": v(-650, 375.28) * mm});
            skLineSegment(sketch, "E427.MirrorCS", {"start": v(880, 496.52) * mm, "end": v(810, 456.1) * mm});
            skLineSegment(sketch, "E428.MirrorCS", {"start": v(-640, 357.96) * mm, "end": v(-570, 317.54) * mm});
            skLineSegment(sketch, "E429.MirrorCS", {"start": v(330, 456.1) * mm, "end": v(330, 375.28) * mm});
            skLineSegment(sketch, "E430.MirrorCS", {"start": v(410, 513.84) * mm, "end": v(410, 594.67) * mm});
            skLineSegment(sketch, "E431.MirrorCS", {"start": v(960, 635.09) * mm, "end": v(890, 594.67) * mm});
            skLineSegment(sketch, "E432.MirrorCS", {"start": v(240, 496.52) * mm, "end": v(170, 456.1) * mm});
            skLineSegment(sketch, "E433.MirrorCS", {"start": v(230, 317.54) * mm, "end": v(160, 357.96) * mm});
            skLineSegment(sketch, "E434.MirrorCS", {"start": v(710, 513.84) * mm, "end": v(710, 594.67) * mm});
            skLineSegment(sketch, "E435.MirrorCS", {"start": v(-640, 635.09) * mm, "end": v(-710, 594.67) * mm});
            skLineSegment(sketch, "E436.MirrorCS", {"start": v(1120, 473.43) * mm, "end": v(1050, 513.84) * mm});
            skLineSegment(sketch, "E437.MirrorCS", {"start": v(480, 473.43) * mm, "end": v(410, 513.84) * mm});
            skLineSegment(sketch, "E438.MirrorCS", {"start": v(-710, 513.84) * mm, "end": v(-640, 473.43) * mm});
            skLineSegment(sketch, "E439.MirrorCS", {"start": v(630, 456.1) * mm, "end": v(630, 375.28) * mm});
            skLineSegment(sketch, "E440.MirrorCS", {"start": v(650, 456.1) * mm, "end": v(720, 496.52) * mm});
            skLineSegment(sketch, "E441.MirrorCS", {"start": v(950, 456.1) * mm, "end": v(880, 496.52) * mm});
            skLineSegment(sketch, "E442.MirrorCS", {"start": v(-230, 513.84) * mm, "end": v(-230, 594.67) * mm});
            skLineSegment(sketch, "E443.MirrorCS", {"start": v(1110, 456.1) * mm, "end": v(1040, 496.52) * mm});
            skLineSegment(sketch, "E444.MirrorCS", {"start": v(400, 334.86) * mm, "end": v(470, 375.28) * mm});
            skLineSegment(sketch, "E445.MirrorCS", {"start": v(400, 496.52) * mm, "end": v(330, 456.1) * mm});
            skLineSegment(sketch, "E446.MirrorCS", {"start": v(-410, 594.67) * mm, "end": v(-410, 513.84) * mm});
            skLineSegment(sketch, "E447.MirrorCS", {"start": v(1130, 733.23) * mm, "end": v(1190, 767.88) * mm});
            skLineSegment(sketch, "E448.MirrorCS", {"start": v(320, 750.56) * mm, "end": v(250, 790.97) * mm});
            skLineSegment(sketch, "E449.MirrorCS", {"start": v(950, 733.23) * mm, "end": v(880, 773.65) * mm});
            skLineSegment(sketch, "E450.MirrorCS", {"start": v(-400, 773.65) * mm, "end": v(-470, 733.23) * mm});
            skLineSegment(sketch, "E451.MirrorCS", {"start": v(10, 733.23) * mm, "end": v(80, 773.65) * mm});
            skLineSegment(sketch, "E452.MirrorCS", {"start": v(150, 733.23) * mm, "end": v(80, 773.65) * mm});
            skLineSegment(sketch, "E453.MirrorCS", {"start": v(80, 889.12) * mm, "end": v(150, 929.53) * mm});
            skLineSegment(sketch, "E454.MirrorCS", {"start": v(560, 773.65) * mm, "end": v(630, 733.23) * mm});
            skLineSegment(sketch, "E455.MirrorCS", {"start": v(1190, 790.97) * mm, "end": v(1120, 750.56) * mm});
            skLineSegment(sketch, "E456.MirrorCS", {"start": v(720, 889.12) * mm, "end": v(790, 929.53) * mm});
            skLineSegment(sketch, "E457.MirrorCS", {"start": v(1110, 733.23) * mm, "end": v(1040, 773.65) * mm});
            skLineSegment(sketch, "E458.MirrorCS", {"start": v(-650, 733.23) * mm, "end": v(-720, 773.65) * mm});
            skLineSegment(sketch, "E459.MirrorCS", {"start": v(550, 790.97) * mm, "end": v(480, 750.56) * mm});
            skLineSegment(sketch, "E460.MirrorCS", {"start": v(490, 733.23) * mm, "end": v(560, 773.65) * mm});
            skLineSegment(sketch, "E461.MirrorCS", {"start": v(0, 750.56) * mm, "end": v(70, 790.97) * mm});
            skLineSegment(sketch, "E462.MirrorCS", {"start": v(810, 733.23) * mm, "end": v(880, 773.65) * mm});
            skLineSegment(sketch, "E463.MirrorCS", {"start": v(10, 929.53) * mm, "end": v(80, 889.12) * mm});
            skLineSegment(sketch, "E464.MirrorCS", {"start": v(-80, 889.12) * mm, "end": v(-10, 929.53) * mm});
            skLineSegment(sketch, "E465.MirrorCS", {"start": v(640, 750.56) * mm, "end": v(710, 790.97) * mm});
            skLineSegment(sketch, "E466.MirrorCS", {"start": v(-80, 773.65) * mm, "end": v(-150, 733.23) * mm});
            skLineSegment(sketch, "E467.MirrorCS", {"start": v(-70, 790.97) * mm, "end": v(0, 750.56) * mm});
            skLineSegment(sketch, "E468.MirrorCS", {"start": v(320, 750.56) * mm, "end": v(390, 790.97) * mm});
            skLineSegment(sketch, "E469.MirrorCS", {"start": v(-70, 1068.1) * mm, "end": v(0, 1027.68) * mm});
            skLineSegment(sketch, "E470.MirrorCS", {"start": v(870, 790.97) * mm, "end": v(800, 750.56) * mm});
            skLineSegment(sketch, "E471.MirrorCS", {"start": v(400, 773.65) * mm, "end": v(330, 733.23) * mm});
            skLineSegment(sketch, "E472.MirrorCS", {"start": v(1040, 889.12) * mm, "end": v(970, 929.53) * mm});
            skLineSegment(sketch, "E473.MirrorCS", {"start": v(-730, 790.97) * mm, "end": v(-790, 756.33) * mm});
            skLineSegment(sketch, "E474.MirrorCS", {"start": v(-630, 929.53) * mm, "end": v(-560, 889.12) * mm});
            skLineSegment(sketch, "E475.MirrorCS", {"start": v(480, 750.56) * mm, "end": v(410, 790.97) * mm});
            skLineSegment(sketch, "E476.MirrorCS", {"start": v(1040, 889.12) * mm, "end": v(1110, 929.53) * mm});
            skLineSegment(sketch, "E477.MirrorCS", {"start": v(0, 1027.68) * mm, "end": v(70, 1068.1) * mm});
            skLineSegment(sketch, "E478.MirrorCS", {"start": v(-240, 889.12) * mm, "end": v(-310, 929.53) * mm});
            skLineSegment(sketch, "E479.MirrorCS", {"start": v(-720, 773.65) * mm, "end": v(-790, 733.23) * mm});
            skLineSegment(sketch, "E480.MirrorCS", {"start": v(470, 929.53) * mm, "end": v(400, 889.12) * mm});
            skLineSegment(sketch, "E481.MirrorCS", {"start": v(-320, 750.56) * mm, "end": v(-250, 790.97) * mm});
            skLineSegment(sketch, "E482.MirrorCS", {"start": v(960, 750.56) * mm, "end": v(1030, 790.97) * mm});
            skLineSegment(sketch, "E483.MirrorCS", {"start": v(790, 733.23) * mm, "end": v(720, 773.65) * mm});
            skLineSegment(sketch, "E484.MirrorCS", {"start": v(-410, 790.97) * mm, "end": v(-480, 750.56) * mm});
            skLineSegment(sketch, "E485.MirrorCS", {"start": v(-150, 929.53) * mm, "end": v(-80, 889.12) * mm});
            skLineSegment(sketch, "E486.MirrorCS", {"start": v(650, 733.23) * mm, "end": v(720, 773.65) * mm});
            skLineSegment(sketch, "E487.MirrorCS", {"start": v(960, 750.56) * mm, "end": v(890, 790.97) * mm});
            skLineSegment(sketch, "E488.MirrorCS", {"start": v(-240, 773.65) * mm, "end": v(-170, 733.23) * mm});
            skLineSegment(sketch, "E489.MirrorCS", {"start": v(-560, 889.12) * mm, "end": v(-490, 929.53) * mm});
            skLineSegment(sketch, "E490.MirrorCS", {"start": v(310, 929.53) * mm, "end": v(240, 889.12) * mm});
            skLineSegment(sketch, "E491.MirrorCS", {"start": v(-640, 750.56) * mm, "end": v(-570, 790.97) * mm});
            skLineSegment(sketch, "E492.MirrorCS", {"start": v(720, 889.12) * mm, "end": v(650, 929.53) * mm});
            skLineSegment(sketch, "E493.MirrorCS", {"start": v(880, 889.12) * mm, "end": v(810, 929.53) * mm});
            skLineSegment(sketch, "E494.MirrorCS", {"start": v(560, 889.12) * mm, "end": v(490, 929.53) * mm});
            skLineSegment(sketch, "E495.MirrorCS", {"start": v(560, 889.12) * mm, "end": v(630, 929.53) * mm});
            skLineSegment(sketch, "E496.MirrorCS", {"start": v(-390, 790.97) * mm, "end": v(-320, 750.56) * mm});
            skLineSegment(sketch, "E497.MirrorCS", {"start": v(-240, 889.12) * mm, "end": v(-170, 929.53) * mm});
            skLineSegment(sketch, "E498.MirrorCS", {"start": v(400, 889.12) * mm, "end": v(330, 929.53) * mm});
            skLineSegment(sketch, "E499.MirrorCS", {"start": v(-240, 773.65) * mm, "end": v(-310, 733.23) * mm});
            skLineSegment(sketch, "E500.MirrorCS", {"start": v(-160, 750.56) * mm, "end": v(-90, 790.97) * mm});
            skLineSegment(sketch, "E501.MirrorCS", {"start": v(-720, 889.12) * mm, "end": v(-650, 929.53) * mm});
            skLineSegment(sketch, "E502.MirrorCS", {"start": v(90, 790.97) * mm, "end": v(160, 750.56) * mm});
            skLineSegment(sketch, "E503.MirrorCS", {"start": v(-560, 773.65) * mm, "end": v(-490, 733.23) * mm});
            skLineSegment(sketch, "E504.MirrorCS", {"start": v(-560, 773.65) * mm, "end": v(-630, 733.23) * mm});
            skLineSegment(sketch, "E505.MirrorCS", {"start": v(0, 1189.34) * mm, "end": v(-70, 1148.93) * mm});
            skLineSegment(sketch, "E506.MirrorCS", {"start": v(-550, 790.97) * mm, "end": v(-480, 750.56) * mm});
            skLineSegment(sketch, "E507.MirrorCS", {"start": v(240, 773.65) * mm, "end": v(170, 733.23) * mm});
            skLineSegment(sketch, "E508.MirrorCS", {"start": v(170, 929.53) * mm, "end": v(240, 889.12) * mm});
            skLineSegment(sketch, "E509.MirrorCS", {"start": v(800, 750.56) * mm, "end": v(730, 790.97) * mm});
            skLineSegment(sketch, "E510.MirrorCS", {"start": v(-330, 733.23) * mm, "end": v(-400, 773.65) * mm});
            skLineSegment(sketch, "E511.MirrorCS", {"start": v(-160, 750.56) * mm, "end": v(-230, 790.97) * mm});
            skLineSegment(sketch, "E512.MirrorCS", {"start": v(950, 929.53) * mm, "end": v(880, 889.12) * mm});
            skLineSegment(sketch, "E513.MirrorCS", {"start": v(-10, 733.23) * mm, "end": v(-80, 773.65) * mm});
            skLineSegment(sketch, "E514.MirrorCS", {"start": v(-470, 929.53) * mm, "end": v(-400, 889.12) * mm});
            skLineSegment(sketch, "E515.MirrorCS", {"start": v(1130, 929.53) * mm, "end": v(1190, 894.9) * mm});
            skLineSegment(sketch, "E516.MirrorCS", {"start": v(-330, 929.53) * mm, "end": v(-400, 889.12) * mm});
            skLineSegment(sketch, "E517.MirrorCS", {"start": v(570, 790.97) * mm, "end": v(640, 750.56) * mm});
            skLineSegment(sketch, "E518.MirrorCS", {"start": v(310, 733.23) * mm, "end": v(240, 773.65) * mm});
            skLineSegment(sketch, "E519.MirrorCS", {"start": v(970, 733.23) * mm, "end": v(1040, 773.65) * mm});
            skLineSegment(sketch, "E520.MirrorCS", {"start": v(230, 790.97) * mm, "end": v(160, 750.56) * mm});
            skLineSegment(sketch, "E521.MirrorCS", {"start": v(1120, 750.56) * mm, "end": v(1050, 790.97) * mm});
            skLineSegment(sketch, "E522.MirrorCS", {"start": v(-640, 750.56) * mm, "end": v(-710, 790.97) * mm});
            skLineSegment(sketch, "E523.MirrorCS", {"start": v(470, 733.23) * mm, "end": v(400, 773.65) * mm});
            skLineSegment(sketch, "E524.MirrorCS", {"start": v(-720, 889.12) * mm, "end": v(-790, 929.53) * mm});
            skLineSegment(sketch, "E525.MirrorCS", {"start": v(550, 790.97) * mm, "end": v(550, 871.8) * mm});
            skLineSegment(sketch, "E526.MirrorCS", {"start": v(570, 790.97) * mm, "end": v(570, 871.8) * mm});
            skLineSegment(sketch, "E527.MirrorCS", {"start": v(310, 929.53) * mm, "end": v(310, 1010.36) * mm});
            skLineSegment(sketch, "E528.MirrorCS", {"start": v(-170, 929.53) * mm, "end": v(-240, 889.12) * mm});
            skLineSegment(sketch, "E529.MirrorCS", {"start": v(880, 773.65) * mm, "end": v(950, 733.23) * mm});
            skLineSegment(sketch, "E530.MirrorCS", {"start": v(710, 790.97) * mm, "end": v(640, 750.56) * mm});
            skLineSegment(sketch, "E531.MirrorCS", {"start": v(250, 1068.1) * mm, "end": v(320, 1027.68) * mm});
            skLineSegment(sketch, "E532.MirrorCS", {"start": v(870, 871.8) * mm, "end": v(800, 912.21) * mm});
            skLineSegment(sketch, "E533.MirrorCS", {"start": v(800, 750.56) * mm, "end": v(870, 790.97) * mm});
            skLineSegment(sketch, "E534.MirrorCS", {"start": v(490, 929.53) * mm, "end": v(490, 1010.36) * mm});
            skLineSegment(sketch, "E535.MirrorCS", {"start": v(-90, 594.67) * mm, "end": v(-160, 635.09) * mm});
            skLineSegment(sketch, "E536.MirrorCS", {"start": v(-560, 1050.78) * mm, "end": v(-490, 1010.36) * mm});
            skLineSegment(sketch, "E537.MirrorCS", {"start": v(-150, 652.4) * mm, "end": v(-80, 612) * mm});
            skLineSegment(sketch, "E538.MirrorCS", {"start": v(70, 1068.1) * mm, "end": v(70, 1148.93) * mm});
            skLineSegment(sketch, "E539.MirrorCS", {"start": v(630, 733.23) * mm, "end": v(560, 773.65) * mm});
            skLineSegment(sketch, "E540.MirrorCS", {"start": v(-790, 733.23) * mm, "end": v(-790, 652.4) * mm});
            skLineSegment(sketch, "E541.MirrorCS", {"start": v(320, 912.21) * mm, "end": v(390, 871.8) * mm});
            skLineSegment(sketch, "E542.MirrorCS", {"start": v(470, 929.53) * mm, "end": v(470, 1010.36) * mm});
            skLineSegment(sketch, "E543.MirrorCS", {"start": v(-80, 773.65) * mm, "end": v(-10, 733.23) * mm});
            skLineSegment(sketch, "E544.MirrorCS", {"start": v(-170, 733.23) * mm, "end": v(-170, 652.4) * mm});
            skLineSegment(sketch, "E545.MirrorCS", {"start": v(230, 1148.93) * mm, "end": v(230, 1068.1) * mm});
            skLineSegment(sketch, "E546.MirrorCS", {"start": v(-490, 652.4) * mm, "end": v(-490, 733.23) * mm});
            skLineSegment(sketch, "E547.MirrorCS", {"start": v(-90, 1068.1) * mm, "end": v(-160, 1027.68) * mm});
            skLineSegment(sketch, "E548.MirrorCS", {"start": v(-480, 750.56) * mm, "end": v(-550, 790.97) * mm});
            skLineSegment(sketch, "E549.MirrorCS", {"start": v(-390, 1148.93) * mm, "end": v(-390, 1068.1) * mm});
            skLineSegment(sketch, "E550.MirrorCS", {"start": v(-640, 1189.34) * mm, "end": v(-710, 1148.93) * mm});
            skLineSegment(sketch, "E551.MirrorCS", {"start": v(1030, 790.97) * mm, "end": v(960, 750.56) * mm});
            skLineSegment(sketch, "E552.MirrorCS", {"start": v(70, 1148.93) * mm, "end": v(0, 1189.34) * mm});
            skLineSegment(sketch, "E553.MirrorCS", {"start": v(-490, 733.23) * mm, "end": v(-560, 773.65) * mm});
            skLineSegment(sketch, "E554.MirrorCS", {"start": v(-160, 1189.34) * mm, "end": v(-90, 1148.93) * mm});
            skLineSegment(sketch, "E555.MirrorCS", {"start": v(880, 773.65) * mm, "end": v(810, 733.23) * mm});
            skLineSegment(sketch, "E556.MirrorCS", {"start": v(-720, 1050.78) * mm, "end": v(-650, 1010.36) * mm});
            skLineSegment(sketch, "E557.MirrorCS", {"start": v(1110, 929.53) * mm, "end": v(1110, 1010.36) * mm});
            skLineSegment(sketch, "E558.MirrorCS", {"start": v(810, 652.4) * mm, "end": v(810, 733.23) * mm});
            skLineSegment(sketch, "E559.MirrorCS", {"start": v(1130, 652.4) * mm, "end": v(1190, 617.76) * mm});
            skLineSegment(sketch, "E560.MirrorCS", {"start": v(-400, 1050.78) * mm, "end": v(-470, 1010.36) * mm});
            skLineSegment(sketch, "E561.MirrorCS", {"start": v(80, 612) * mm, "end": v(150, 652.4) * mm});
            skLineSegment(sketch, "E562.MirrorCS", {"start": v(-10, 652.4) * mm, "end": v(-10, 733.23) * mm});
            skLineSegment(sketch, "E563.MirrorCS", {"start": v(-90, 790.97) * mm, "end": v(-160, 750.56) * mm});
            skLineSegment(sketch, "E564.MirrorCS", {"start": v(1030, 1068.1) * mm, "end": v(1030, 1148.93) * mm});
            skLineSegment(sketch, "E565.MirrorCS", {"start": v(-150, 733.23) * mm, "end": v(-80, 773.65) * mm});
            skLineSegment(sketch, "E566.MirrorCS", {"start": v(390, 1068.1) * mm, "end": v(390, 1148.93) * mm});
            skLineSegment(sketch, "E567.MirrorCS", {"start": v(570, 1068.1) * mm, "end": v(640, 1027.68) * mm});
            skLineSegment(sketch, "E568.MirrorCS", {"start": v(570, 871.8) * mm, "end": v(640, 912.21) * mm});
            skLineSegment(sketch, "E569.MirrorCS", {"start": v(150, 929.53) * mm, "end": v(80, 889.12) * mm});
            skLineSegment(sketch, "E570.MirrorCS", {"start": v(1190, 894.9) * mm, "end": v(1130, 929.53) * mm});
            skLineSegment(sketch, "E571.MirrorCS", {"start": v(800, 635.09) * mm, "end": v(730, 594.67) * mm});
            skLineSegment(sketch, "E572.MirrorCS", {"start": v(-400, 889.12) * mm, "end": v(-330, 929.53) * mm});
            skLineSegment(sketch, "E573.MirrorCS", {"start": v(800, 1189.34) * mm, "end": v(870, 1148.93) * mm});
            skLineSegment(sketch, "E574.MirrorCS", {"start": v(1120, 1189.34) * mm, "end": v(1190, 1148.93) * mm});
            skLineSegment(sketch, "E575.MirrorCS", {"start": v(1190, 767.88) * mm, "end": v(1130, 733.23) * mm});
            skLineSegment(sketch, "E576.MirrorCS", {"start": v(720, 773.65) * mm, "end": v(650, 733.23) * mm});
            skLineSegment(sketch, "E577.MirrorCS", {"start": v(-470, 733.23) * mm, "end": v(-400, 773.65) * mm});
            skLineSegment(sketch, "E578.MirrorCS", {"start": v(170, 733.23) * mm, "end": v(240, 773.65) * mm});
            skLineSegment(sketch, "E579.MirrorCS", {"start": v(320, 1189.34) * mm, "end": v(250, 1148.93) * mm});
            skLineSegment(sketch, "E580.MirrorCS", {"start": v(1190, 594.67) * mm, "end": v(1120, 635.09) * mm});
            skLineSegment(sketch, "E581.MirrorCS", {"start": v(640, 750.56) * mm, "end": v(570, 790.97) * mm});
            skLineSegment(sketch, "E582.MirrorCS", {"start": v(1110, 1010.36) * mm, "end": v(1040, 1050.78) * mm});
            skLineSegment(sketch, "E583.MirrorCS", {"start": v(-320, 1189.34) * mm, "end": v(-390, 1148.93) * mm});
            skLineSegment(sketch, "E584.MirrorCS", {"start": v(550, 1148.93) * mm, "end": v(550, 1068.1) * mm});
            skLineSegment(sketch, "E585.MirrorCS", {"start": v(310, 652.4) * mm, "end": v(240, 612) * mm});
            skLineSegment(sketch, "E586.MirrorCS", {"start": v(250, 1148.93) * mm, "end": v(250, 1068.1) * mm});
            skLineSegment(sketch, "E587.MirrorCS", {"start": v(-320, 1027.68) * mm, "end": v(-250, 1068.1) * mm});
            skLineSegment(sketch, "E588.MirrorCS", {"start": v(880, 1050.78) * mm, "end": v(810, 1010.36) * mm});
            skLineSegment(sketch, "E589.MirrorCS", {"start": v(470, 1010.36) * mm, "end": v(400, 1050.78) * mm});
            skLineSegment(sketch, "E590.MirrorCS", {"start": v(640, 1189.34) * mm, "end": v(570, 1148.93) * mm});
            skLineSegment(sketch, "E591.MirrorCS", {"start": v(400, 612) * mm, "end": v(330, 652.4) * mm});
            skLineSegment(sketch, "E592.MirrorCS", {"start": v(250, 790.97) * mm, "end": v(320, 750.56) * mm});
            skLineSegment(sketch, "E593.MirrorCS", {"start": v(-710, 1068.1) * mm, "end": v(-640, 1027.68) * mm});
            skLineSegment(sketch, "E594.MirrorCS", {"start": v(560, 1050.78) * mm, "end": v(630, 1010.36) * mm});
            skLineSegment(sketch, "E595.MirrorCS", {"start": v(-10, 929.53) * mm, "end": v(-80, 889.12) * mm});
            skLineSegment(sketch, "E596.MirrorCS", {"start": v(890, 1148.93) * mm, "end": v(890, 1068.1) * mm});
            skLineSegment(sketch, "E597.MirrorCS", {"start": v(-710, 1148.93) * mm, "end": v(-710, 1068.1) * mm});
            skLineSegment(sketch, "E598.MirrorCS", {"start": v(-70, 1148.93) * mm, "end": v(-70, 1068.1) * mm});
            skLineSegment(sketch, "E599.MirrorCS", {"start": v(240, 773.65) * mm, "end": v(310, 733.23) * mm});
            skLineSegment(sketch, "E600.MirrorCS", {"start": v(-310, 1010.36) * mm, "end": v(-310, 929.53) * mm});
            skLineSegment(sketch, "E601.MirrorCS", {"start": v(-250, 1068.1) * mm, "end": v(-250, 1148.93) * mm});
            skLineSegment(sketch, "E602.MirrorCS", {"start": v(640, 635.09) * mm, "end": v(710, 594.67) * mm});
            skLineSegment(sketch, "E603.MirrorCS", {"start": v(400, 773.65) * mm, "end": v(470, 733.23) * mm});
            skLineSegment(sketch, "E604.MirrorCS", {"start": v(-720, 773.65) * mm, "end": v(-650, 733.23) * mm});
            skLineSegment(sketch, "E605.MirrorCS", {"start": v(330, 929.53) * mm, "end": v(400, 889.12) * mm});
            skLineSegment(sketch, "E606.MirrorCS", {"start": v(1050, 1068.1) * mm, "end": v(1050, 1148.93) * mm});
            skLineSegment(sketch, "E607.MirrorCS", {"start": v(10, 733.23) * mm, "end": v(10, 652.4) * mm});
            skLineSegment(sketch, "E608.MirrorCS", {"start": v(-90, 790.97) * mm, "end": v(-90, 871.8) * mm});
            skLineSegment(sketch, "E609.MirrorCS", {"start": v(90, 1068.1) * mm, "end": v(90, 1148.93) * mm});
            skLineSegment(sketch, "E610.MirrorCS", {"start": v(70, 790.97) * mm, "end": v(0, 750.56) * mm});
            skLineSegment(sketch, "E611.MirrorCS", {"start": v(1050, 790.97) * mm, "end": v(1120, 750.56) * mm});
            skLineSegment(sketch, "E612.MirrorCS", {"start": v(-790, 733.23) * mm, "end": v(-720, 773.65) * mm});
            skLineSegment(sketch, "E613.MirrorCS", {"start": v(160, 912.21) * mm, "end": v(90, 871.8) * mm});
            skLineSegment(sketch, "E614.MirrorCS", {"start": v(-640, 1027.68) * mm, "end": v(-570, 1068.1) * mm});
            skLineSegment(sketch, "E615.MirrorCS", {"start": v(710, 1148.93) * mm, "end": v(640, 1189.34) * mm});
            skLineSegment(sketch, "E616.MirrorCS", {"start": v(1110, 652.4) * mm, "end": v(1040, 612) * mm});
            skLineSegment(sketch, "E617.MirrorCS", {"start": v(-650, 1010.36) * mm, "end": v(-650, 929.53) * mm});
            skLineSegment(sketch, "E618.MirrorCS", {"start": v(720, 1050.78) * mm, "end": v(790, 1010.36) * mm});
            skLineSegment(sketch, "E619.MirrorCS", {"start": v(-410, 790.97) * mm, "end": v(-410, 871.8) * mm});
            skLineSegment(sketch, "E620.MirrorCS", {"start": v(-720, 612) * mm, "end": v(-650, 652.4) * mm});
            skLineSegment(sketch, "E621.MirrorCS", {"start": v(-480, 1027.68) * mm, "end": v(-550, 1068.1) * mm});
            skLineSegment(sketch, "E622.MirrorCS", {"start": v(10, 1010.36) * mm, "end": v(80, 1050.78) * mm});
            skLineSegment(sketch, "E623.MirrorCS", {"start": v(150, 1010.36) * mm, "end": v(150, 929.53) * mm});
            skLineSegment(sketch, "E624.MirrorCS", {"start": v(720, 612) * mm, "end": v(790, 652.4) * mm});
            skLineSegment(sketch, "E625.MirrorCS", {"start": v(-560, 889.12) * mm, "end": v(-630, 929.53) * mm});
            skLineSegment(sketch, "E626.MirrorCS", {"start": v(-390, 594.67) * mm, "end": v(-320, 635.09) * mm});
            skLineSegment(sketch, "E627.MirrorCS", {"start": v(-480, 1189.34) * mm, "end": v(-410, 1148.93) * mm});
            skLineSegment(sketch, "E628.MirrorCS", {"start": v(790, 929.53) * mm, "end": v(720, 889.12) * mm});
            skLineSegment(sketch, "E629.MirrorCS", {"start": v(400, 1050.78) * mm, "end": v(330, 1010.36) * mm});
            skLineSegment(sketch, "E630.MirrorCS", {"start": v(230, 594.67) * mm, "end": v(160, 635.09) * mm});
            skLineSegment(sketch, "E631.MirrorCS", {"start": v(-790, 1183.57) * mm, "end": v(-730, 1148.93) * mm});
            skLineSegment(sketch, "E632.MirrorCS", {"start": v(1130, 1010.36) * mm, "end": v(1190, 1045) * mm});
            skLineSegment(sketch, "E633.MirrorCS", {"start": v(-470, 1010.36) * mm, "end": v(-470, 929.53) * mm});
            skLineSegment(sketch, "E634.MirrorCS", {"start": v(90, 1148.93) * mm, "end": v(160, 1189.34) * mm});
            skLineSegment(sketch, "E635.MirrorCS", {"start": v(1120, 912.21) * mm, "end": v(1050, 871.8) * mm});
            skLineSegment(sketch, "E636.MirrorCS", {"start": v(310, 1010.36) * mm, "end": v(240, 1050.78) * mm});
            skLineSegment(sketch, "E637.MirrorCS", {"start": v(890, 1068.1) * mm, "end": v(960, 1027.68) * mm});
            skLineSegment(sketch, "E638.MirrorCS", {"start": v(-480, 750.56) * mm, "end": v(-410, 790.97) * mm});
            skLineSegment(sketch, "E639.MirrorCS", {"start": v(950, 733.23) * mm, "end": v(950, 652.4) * mm});
            skLineSegment(sketch, "E640.MirrorCS", {"start": v(-470, 652.4) * mm, "end": v(-470, 733.23) * mm});
            skLineSegment(sketch, "E641.MirrorCS", {"start": v(-570, 1068.1) * mm, "end": v(-570, 1148.93) * mm});
            skLineSegment(sketch, "E642.MirrorCS", {"start": v(-650, 652.4) * mm, "end": v(-650, 733.23) * mm});
            skLineSegment(sketch, "E643.MirrorCS", {"start": v(-230, 1068.1) * mm, "end": v(-230, 1148.93) * mm});
            skLineSegment(sketch, "E644.MirrorCS", {"start": v(1190, 1068.1) * mm, "end": v(1120, 1027.68) * mm});
            skLineSegment(sketch, "E645.MirrorCS", {"start": v(80, 773.65) * mm, "end": v(150, 733.23) * mm});
            skLineSegment(sketch, "E646.MirrorCS", {"start": v(90, 871.8) * mm, "end": v(90, 790.97) * mm});
            skLineSegment(sketch, "E647.MirrorCS", {"start": v(240, 889.12) * mm, "end": v(170, 929.53) * mm});
            skLineSegment(sketch, "E648.MirrorCS", {"start": v(570, 1148.93) * mm, "end": v(570, 1068.1) * mm});
            skLineSegment(sketch, "E649.MirrorCS", {"start": v(-480, 912.21) * mm, "end": v(-550, 871.8) * mm});
            skLineSegment(sketch, "E650.MirrorCS", {"start": v(730, 790.97) * mm, "end": v(800, 750.56) * mm});
            skLineSegment(sketch, "E651.MirrorCS", {"start": v(400, 889.12) * mm, "end": v(470, 929.53) * mm});
            skLineSegment(sketch, "E652.MirrorCS", {"start": v(320, 1027.68) * mm, "end": v(390, 1068.1) * mm});
            skLineSegment(sketch, "E653.MirrorCS", {"start": v(-480, 635.09) * mm, "end": v(-550, 594.67) * mm});
            skLineSegment(sketch, "E654.MirrorCS", {"start": v(-640, 912.21) * mm, "end": v(-570, 871.8) * mm});
            skLineSegment(sketch, "E655.MirrorCS", {"start": v(890, 790.97) * mm, "end": v(960, 750.56) * mm});
            skLineSegment(sketch, "E656.MirrorCS", {"start": v(-730, 871.8) * mm, "end": v(-790, 906.44) * mm});
            skLineSegment(sketch, "E657.MirrorCS", {"start": v(650, 1010.36) * mm, "end": v(720, 1050.78) * mm});
            skLineSegment(sketch, "E658.MirrorCS", {"start": v(1130, 733.23) * mm, "end": v(1130, 652.4) * mm});
            skLineSegment(sketch, "E659.MirrorCS", {"start": v(160, 750.56) * mm, "end": v(90, 790.97) * mm});
            skLineSegment(sketch, "E660.MirrorCS", {"start": v(-70, 594.67) * mm, "end": v(0, 635.09) * mm});
            skLineSegment(sketch, "E661.MirrorCS", {"start": v(480, 1027.68) * mm, "end": v(410, 1068.1) * mm});
            skLineSegment(sketch, "E662.MirrorCS", {"start": v(560, 773.65) * mm, "end": v(490, 733.23) * mm});
            skLineSegment(sketch, "E663.MirrorCS", {"start": v(730, 1068.1) * mm, "end": v(730, 1148.93) * mm});
            skLineSegment(sketch, "E664.MirrorCS", {"start": v(1040, 1050.78) * mm, "end": v(970, 1010.36) * mm});
            skLineSegment(sketch, "E665.MirrorCS", {"start": v(-790, 652.4) * mm, "end": v(-720, 612) * mm});
            skLineSegment(sketch, "E666.MirrorCS", {"start": v(-570, 1148.93) * mm, "end": v(-640, 1189.34) * mm});
            skLineSegment(sketch, "E667.MirrorCS", {"start": v(650, 929.53) * mm, "end": v(720, 889.12) * mm});
            skLineSegment(sketch, "E668.MirrorCS", {"start": v(490, 929.53) * mm, "end": v(560, 889.12) * mm});
            skLineSegment(sketch, "E669.MirrorCS", {"start": v(890, 790.97) * mm, "end": v(890, 871.8) * mm});
            skLineSegment(sketch, "E670.MirrorCS", {"start": v(950, 652.4) * mm, "end": v(880, 612) * mm});
            skLineSegment(sketch, "E671.MirrorCS", {"start": v(-330, 652.4) * mm, "end": v(-400, 612) * mm});
            skLineSegment(sketch, "E672.MirrorCS", {"start": v(80, 773.65) * mm, "end": v(10, 733.23) * mm});
            skLineSegment(sketch, "E673.MirrorCS", {"start": v(160, 1027.68) * mm, "end": v(90, 1068.1) * mm});
            skLineSegment(sketch, "E674.MirrorCS", {"start": v(870, 594.67) * mm, "end": v(800, 635.09) * mm});
            skLineSegment(sketch, "E675.MirrorCS", {"start": v(640, 912.21) * mm, "end": v(710, 871.8) * mm});
            skLineSegment(sketch, "E676.MirrorCS", {"start": v(80, 1050.78) * mm, "end": v(150, 1010.36) * mm});
            skLineSegment(sketch, "E677.MirrorCS", {"start": v(0, 912.21) * mm, "end": v(70, 871.8) * mm});
            skLineSegment(sketch, "E678.MirrorCS", {"start": v(410, 1148.93) * mm, "end": v(480, 1189.34) * mm});
            skLineSegment(sketch, "E679.MirrorCS", {"start": v(-570, 871.8) * mm, "end": v(-570, 790.97) * mm});
            skLineSegment(sketch, "E680.MirrorCS", {"start": v(-170, 733.23) * mm, "end": v(-240, 773.65) * mm});
            skLineSegment(sketch, "E681.MirrorCS", {"start": v(-710, 790.97) * mm, "end": v(-710, 871.8) * mm});
            skLineSegment(sketch, "E682.MirrorCS", {"start": v(-630, 652.4) * mm, "end": v(-560, 612) * mm});
            skLineSegment(sketch, "E683.MirrorCS", {"start": v(-710, 594.67) * mm, "end": v(-640, 635.09) * mm});
            skLineSegment(sketch, "E684.MirrorCS", {"start": v(550, 1068.1) * mm, "end": v(480, 1027.68) * mm});
            skLineSegment(sketch, "E685.MirrorCS", {"start": v(1190, 871.8) * mm, "end": v(1120, 912.21) * mm});
            skLineSegment(sketch, "E686.MirrorCS", {"start": v(-80, 1050.78) * mm, "end": v(-10, 1010.36) * mm});
            skLineSegment(sketch, "E687.MirrorCS", {"start": v(-630, 1010.36) * mm, "end": v(-560, 1050.78) * mm});
            skLineSegment(sketch, "E688.MirrorCS", {"start": v(480, 1189.34) * mm, "end": v(550, 1148.93) * mm});
            skLineSegment(sketch, "E689.MirrorCS", {"start": v(1190, 790.97) * mm, "end": v(1190, 871.8) * mm});
            skLineSegment(sketch, "E690.MirrorCS", {"start": v(570, 594.67) * mm, "end": v(640, 635.09) * mm});
            skLineSegment(sketch, "E691.MirrorCS", {"start": v(490, 733.23) * mm, "end": v(490, 652.4) * mm});
            skLineSegment(sketch, "E692.MirrorCS", {"start": v(-330, 1010.36) * mm, "end": v(-400, 1050.78) * mm});
            skLineSegment(sketch, "E693.MirrorCS", {"start": v(650, 733.23) * mm, "end": v(650, 652.4) * mm});
            skLineSegment(sketch, "E694.MirrorCS", {"start": v(-10, 1010.36) * mm, "end": v(-10, 929.53) * mm});
            skLineSegment(sketch, "E695.MirrorCS", {"start": v(810, 929.53) * mm, "end": v(880, 889.12) * mm});
            skLineSegment(sketch, "E696.MirrorCS", {"start": v(1110, 929.53) * mm, "end": v(1040, 889.12) * mm});
            skLineSegment(sketch, "E697.MirrorCS", {"start": v(10, 929.53) * mm, "end": v(10, 1010.36) * mm});
            skLineSegment(sketch, "E698.MirrorCS", {"start": v(710, 871.8) * mm, "end": v(710, 790.97) * mm});
            skLineSegment(sketch, "E699.MirrorCS", {"start": v(870, 790.97) * mm, "end": v(870, 871.8) * mm});
            skLineSegment(sketch, "E700.MirrorCS", {"start": v(-250, 1148.93) * mm, "end": v(-320, 1189.34) * mm});
            skLineSegment(sketch, "E701.MirrorCS", {"start": v(-240, 612) * mm, "end": v(-310, 652.4) * mm});
            skLineSegment(sketch, "E702.MirrorCS", {"start": v(-790, 756.33) * mm, "end": v(-730, 790.97) * mm});
            skLineSegment(sketch, "E703.MirrorCS", {"start": v(-560, 612) * mm, "end": v(-490, 652.4) * mm});
            skLineSegment(sketch, "E704.MirrorCS", {"start": v(-630, 733.23) * mm, "end": v(-630, 652.4) * mm});
            skLineSegment(sketch, "E705.MirrorCS", {"start": v(-400, 773.65) * mm, "end": v(-330, 733.23) * mm});
            skLineSegment(sketch, "E706.MirrorCS", {"start": v(870, 1068.1) * mm, "end": v(800, 1027.68) * mm});
            skLineSegment(sketch, "E707.MirrorCS", {"start": v(-250, 790.97) * mm, "end": v(-320, 750.56) * mm});
            skLineSegment(sketch, "E708.MirrorCS", {"start": v(-710, 790.97) * mm, "end": v(-640, 750.56) * mm});
            skLineSegment(sketch, "E709.MirrorCS", {"start": v(950, 929.53) * mm, "end": v(950, 1010.36) * mm});
            skLineSegment(sketch, "E710.MirrorCS", {"start": v(-170, 929.53) * mm, "end": v(-170, 1010.36) * mm});
            skLineSegment(sketch, "E711.MirrorCS", {"start": v(970, 1010.36) * mm, "end": v(970, 929.53) * mm});
            skLineSegment(sketch, "E712.MirrorCS", {"start": v(230, 790.97) * mm, "end": v(230, 871.8) * mm});
            skLineSegment(sketch, "E713.MirrorCS", {"start": v(-390, 871.8) * mm, "end": v(-320, 912.21) * mm});
            skLineSegment(sketch, "E714.MirrorCS", {"start": v(1110, 733.23) * mm, "end": v(1110, 652.4) * mm});
            skLineSegment(sketch, "E715.MirrorCS", {"start": v(-90, 1148.93) * mm, "end": v(-90, 1068.1) * mm});
            skLineSegment(sketch, "E716.MirrorCS", {"start": v(-630, 929.53) * mm, "end": v(-630, 1010.36) * mm});
            skLineSegment(sketch, "E717.MirrorCS", {"start": v(320, 635.09) * mm, "end": v(390, 594.67) * mm});
            skLineSegment(sketch, "E718.MirrorCS", {"start": v(240, 889.12) * mm, "end": v(310, 929.53) * mm});
            skLineSegment(sketch, "E719.MirrorCS", {"start": v(0, 750.56) * mm, "end": v(-70, 790.97) * mm});
            skLineSegment(sketch, "E720.MirrorCS", {"start": v(-650, 929.53) * mm, "end": v(-720, 889.12) * mm});
            skLineSegment(sketch, "E721.MirrorCS", {"start": v(-730, 594.67) * mm, "end": v(-790, 629.31) * mm});
            skLineSegment(sketch, "E722.MirrorCS", {"start": v(480, 635.09) * mm, "end": v(410, 594.67) * mm});
            skLineSegment(sketch, "E723.MirrorCS", {"start": v(480, 750.56) * mm, "end": v(550, 790.97) * mm});
            skLineSegment(sketch, "E724.MirrorCS", {"start": v(970, 652.4) * mm, "end": v(970, 733.23) * mm});
            skLineSegment(sketch, "E725.MirrorCS", {"start": v(470, 733.23) * mm, "end": v(470, 652.4) * mm});
            skLineSegment(sketch, "E726.MirrorCS", {"start": v(490, 1010.36) * mm, "end": v(560, 1050.78) * mm});
            skLineSegment(sketch, "E727.MirrorCS", {"start": v(1030, 871.8) * mm, "end": v(1030, 790.97) * mm});
            skLineSegment(sketch, "E728.MirrorCS", {"start": v(1120, 750.56) * mm, "end": v(1190, 790.97) * mm});
            skLineSegment(sketch, "E729.MirrorCS", {"start": v(630, 652.4) * mm, "end": v(630, 733.23) * mm});
            skLineSegment(sketch, "E730.MirrorCS", {"start": v(170, 652.4) * mm, "end": v(170, 733.23) * mm});
            skLineSegment(sketch, "E731.MirrorCS", {"start": v(-320, 635.09) * mm, "end": v(-250, 594.67) * mm});
            skLineSegment(sketch, "E732.MirrorCS", {"start": v(-150, 1010.36) * mm, "end": v(-80, 1050.78) * mm});
            skLineSegment(sketch, "E733.MirrorCS", {"start": v(-230, 1148.93) * mm, "end": v(-160, 1189.34) * mm});
            skLineSegment(sketch, "E734.MirrorCS", {"start": v(810, 1010.36) * mm, "end": v(810, 929.53) * mm});
            skLineSegment(sketch, "E735.MirrorCS", {"start": v(240, 612) * mm, "end": v(170, 652.4) * mm});
            skLineSegment(sketch, "E736.MirrorCS", {"start": v(-70, 790.97) * mm, "end": v(-70, 871.8) * mm});
            skLineSegment(sketch, "E737.MirrorCS", {"start": v(150, 652.4) * mm, "end": v(150, 733.23) * mm});
            skLineSegment(sketch, "E738.MirrorCS", {"start": v(-550, 1068.1) * mm, "end": v(-550, 1148.93) * mm});
            skLineSegment(sketch, "E739.MirrorCS", {"start": v(250, 871.8) * mm, "end": v(320, 912.21) * mm});
            skLineSegment(sketch, "E740.MirrorCS", {"start": v(470, 652.4) * mm, "end": v(400, 612) * mm});
            skLineSegment(sketch, "E741.MirrorCS", {"start": v(230, 871.8) * mm, "end": v(160, 912.21) * mm});
            skLineSegment(sketch, "E742.MirrorCS", {"start": v(1030, 1148.93) * mm, "end": v(960, 1189.34) * mm});
            skLineSegment(sketch, "E743.MirrorCS", {"start": v(1040, 612) * mm, "end": v(970, 652.4) * mm});
            skLineSegment(sketch, "E744.MirrorCS", {"start": v(-310, 733.23) * mm, "end": v(-240, 773.65) * mm});
            skLineSegment(sketch, "E745.MirrorCS", {"start": v(410, 1068.1) * mm, "end": v(410, 1148.93) * mm});
            skLineSegment(sketch, "E746.MirrorCS", {"start": v(-390, 790.97) * mm, "end": v(-390, 871.8) * mm});
            skLineSegment(sketch, "E747.MirrorCS", {"start": v(880, 612) * mm, "end": v(810, 652.4) * mm});
            skLineSegment(sketch, "E748.MirrorCS", {"start": v(-70, 871.8) * mm, "end": v(0, 912.21) * mm});
            skLineSegment(sketch, "E749.MirrorCS", {"start": v(230, 1068.1) * mm, "end": v(160, 1027.68) * mm});
            skLineSegment(sketch, "E750.MirrorCS", {"start": v(550, 594.67) * mm, "end": v(480, 635.09) * mm});
            skLineSegment(sketch, "E751.MirrorCS", {"start": v(-170, 1010.36) * mm, "end": v(-240, 1050.78) * mm});
            skLineSegment(sketch, "E752.MirrorCS", {"start": v(240, 1050.78) * mm, "end": v(170, 1010.36) * mm});
            skLineSegment(sketch, "E753.MirrorCS", {"start": v(160, 635.09) * mm, "end": v(90, 594.67) * mm});
            skLineSegment(sketch, "E754.MirrorCS", {"start": v(880, 889.12) * mm, "end": v(950, 929.53) * mm});
            skLineSegment(sketch, "E755.MirrorCS", {"start": v(-160, 1027.68) * mm, "end": v(-230, 1068.1) * mm});
            skLineSegment(sketch, "E756.MirrorCS", {"start": v(1040, 773.65) * mm, "end": v(970, 733.23) * mm});
            skLineSegment(sketch, "E757.MirrorCS", {"start": v(-80, 889.12) * mm, "end": v(-150, 929.53) * mm});
            skLineSegment(sketch, "E758.MirrorCS", {"start": v(630, 929.53) * mm, "end": v(560, 889.12) * mm});
            skLineSegment(sketch, "E759.MirrorCS", {"start": v(1190, 1148.93) * mm, "end": v(1190, 1068.1) * mm});
            skLineSegment(sketch, "E760.MirrorCS", {"start": v(-550, 871.8) * mm, "end": v(-550, 790.97) * mm});
            skLineSegment(sketch, "E761.MirrorCS", {"start": v(70, 871.8) * mm, "end": v(70, 790.97) * mm});
            skLineSegment(sketch, "E762.MirrorCS", {"start": v(410, 790.97) * mm, "end": v(480, 750.56) * mm});
            skLineSegment(sketch, "E763.MirrorCS", {"start": v(-150, 733.23) * mm, "end": v(-150, 652.4) * mm});
            skLineSegment(sketch, "E764.MirrorCS", {"start": v(730, 1148.93) * mm, "end": v(800, 1189.34) * mm});
            skLineSegment(sketch, "E765.MirrorCS", {"start": v(960, 635.09) * mm, "end": v(1030, 594.67) * mm});
            skLineSegment(sketch, "E766.MirrorCS", {"start": v(-730, 790.97) * mm, "end": v(-730, 871.8) * mm});
            skLineSegment(sketch, "E767.MirrorCS", {"start": v(-310, 929.53) * mm, "end": v(-240, 889.12) * mm});
            skLineSegment(sketch, "E768.MirrorCS", {"start": v(390, 1148.93) * mm, "end": v(320, 1189.34) * mm});
            skLineSegment(sketch, "E769.MirrorCS", {"start": v(-550, 1148.93) * mm, "end": v(-480, 1189.34) * mm});
            skLineSegment(sketch, "E770.MirrorCS", {"start": v(790, 1010.36) * mm, "end": v(790, 929.53) * mm});
            skLineSegment(sketch, "E771.MirrorCS", {"start": v(390, 871.8) * mm, "end": v(390, 790.97) * mm});
            skLineSegment(sketch, "E772.MirrorCS", {"start": v(-320, 750.56) * mm, "end": v(-390, 790.97) * mm});
            skLineSegment(sketch, "E773.MirrorCS", {"start": v(800, 1027.68) * mm, "end": v(730, 1068.1) * mm});
            skLineSegment(sketch, "E774.MirrorCS", {"start": v(-490, 1010.36) * mm, "end": v(-490, 929.53) * mm});
            skLineSegment(sketch, "E775.MirrorCS", {"start": v(960, 912.21) * mm, "end": v(1030, 871.8) * mm});
            skLineSegment(sketch, "E776.MirrorCS", {"start": v(390, 790.97) * mm, "end": v(320, 750.56) * mm});
            skLineSegment(sketch, "E777.MirrorCS", {"start": v(870, 1148.93) * mm, "end": v(870, 1068.1) * mm});
            skLineSegment(sketch, "E778.MirrorCS", {"start": v(1120, 1027.68) * mm, "end": v(1050, 1068.1) * mm});
            skLineSegment(sketch, "E779.MirrorCS", {"start": v(-490, 929.53) * mm, "end": v(-560, 889.12) * mm});
            skLineSegment(sketch, "E780.MirrorCS", {"start": v(-790, 929.53) * mm, "end": v(-790, 1010.36) * mm});
            skLineSegment(sketch, "E781.MirrorCS", {"start": v(-240, 1050.78) * mm, "end": v(-310, 1010.36) * mm});
            skLineSegment(sketch, "E782.MirrorCS", {"start": v(890, 871.8) * mm, "end": v(960, 912.21) * mm});
            skLineSegment(sketch, "E783.MirrorCS", {"start": v(550, 871.8) * mm, "end": v(480, 912.21) * mm});
            skLineSegment(sketch, "E784.MirrorCS", {"start": v(170, 1010.36) * mm, "end": v(170, 929.53) * mm});
            skLineSegment(sketch, "E785.MirrorCS", {"start": v(730, 871.8) * mm, "end": v(730, 790.97) * mm});
            skLineSegment(sketch, "E786.MirrorCS", {"start": v(-330, 733.23) * mm, "end": v(-330, 652.4) * mm});
            skLineSegment(sketch, "E787.MirrorCS", {"start": v(-630, 733.23) * mm, "end": v(-560, 773.65) * mm});
            skLineSegment(sketch, "E788.MirrorCS", {"start": v(-710, 871.8) * mm, "end": v(-640, 912.21) * mm});
            skLineSegment(sketch, "E789.MirrorCS", {"start": v(-330, 929.53) * mm, "end": v(-330, 1010.36) * mm});
            skLineSegment(sketch, "E790.MirrorCS", {"start": v(-170, 652.4) * mm, "end": v(-240, 612) * mm});
            skLineSegment(sketch, "E791.MirrorCS", {"start": v(-310, 652.4) * mm, "end": v(-310, 733.23) * mm});
            skLineSegment(sketch, "E792.MirrorCS", {"start": v(970, 929.53) * mm, "end": v(1040, 889.12) * mm});
            skLineSegment(sketch, "E793.MirrorCS", {"start": v(-730, 1148.93) * mm, "end": v(-730, 1068.1) * mm});
            skLineSegment(sketch, "E794.MirrorCS", {"start": v(310, 733.23) * mm, "end": v(310, 652.4) * mm});
            skLineSegment(sketch, "E795.MirrorCS", {"start": v(-410, 1068.1) * mm, "end": v(-480, 1027.68) * mm});
            skLineSegment(sketch, "E796.MirrorCS", {"start": v(-410, 594.67) * mm, "end": v(-480, 635.09) * mm});
            skLineSegment(sketch, "E797.MirrorCS", {"start": v(-160, 912.21) * mm, "end": v(-230, 871.8) * mm});
            skLineSegment(sketch, "E798.MirrorCS", {"start": v(-150, 929.53) * mm, "end": v(-150, 1010.36) * mm});
            skLineSegment(sketch, "E799.MirrorCS", {"start": v(-230, 871.8) * mm, "end": v(-230, 790.97) * mm});
            skLineSegment(sketch, "E800.MirrorCS", {"start": v(250, 790.97) * mm, "end": v(250, 871.8) * mm});
            skLineSegment(sketch, "E801.MirrorCS", {"start": v(-410, 871.8) * mm, "end": v(-480, 912.21) * mm});
            skLineSegment(sketch, "E802.MirrorCS", {"start": v(710, 1068.1) * mm, "end": v(710, 1148.93) * mm});
            skLineSegment(sketch, "E803.MirrorCS", {"start": v(790, 652.4) * mm, "end": v(790, 733.23) * mm});
            skLineSegment(sketch, "E804.MirrorCS", {"start": v(650, 652.4) * mm, "end": v(720, 612) * mm});
            skLineSegment(sketch, "E805.MirrorCS", {"start": v(160, 750.56) * mm, "end": v(230, 790.97) * mm});
            skLineSegment(sketch, "E806.MirrorCS", {"start": v(-790, 1010.36) * mm, "end": v(-720, 1050.78) * mm});
            skLineSegment(sketch, "E807.MirrorCS", {"start": v(-410, 1148.93) * mm, "end": v(-410, 1068.1) * mm});
            skLineSegment(sketch, "E808.MirrorCS", {"start": v(490, 652.4) * mm, "end": v(560, 612) * mm});
            skLineSegment(sketch, "E809.MirrorCS", {"start": v(80, 889.12) * mm, "end": v(10, 929.53) * mm});
            skLineSegment(sketch, "E810.MirrorCS", {"start": v(-160, 635.09) * mm, "end": v(-230, 594.67) * mm});
            skLineSegment(sketch, "E811.MirrorCS", {"start": v(-320, 912.21) * mm, "end": v(-250, 871.8) * mm});
            skLineSegment(sketch, "E812.MirrorCS", {"start": v(-250, 871.8) * mm, "end": v(-250, 790.97) * mm});
            skLineSegment(sketch, "E813.MirrorCS", {"start": v(10, 652.4) * mm, "end": v(80, 612) * mm});
            skLineSegment(sketch, "E814.MirrorCS", {"start": v(-80, 612) * mm, "end": v(-10, 652.4) * mm});
            skLineSegment(sketch, "E815.MirrorCS", {"start": v(-790, 929.53) * mm, "end": v(-720, 889.12) * mm});
            skLineSegment(sketch, "E816.MirrorCS", {"start": v(-400, 889.12) * mm, "end": v(-470, 929.53) * mm});
            skLineSegment(sketch, "E817.MirrorCS", {"start": v(-570, 790.97) * mm, "end": v(-640, 750.56) * mm});
            skLineSegment(sketch, "E818.MirrorCS", {"start": v(650, 929.53) * mm, "end": v(650, 1010.36) * mm});
            skLineSegment(sketch, "E819.MirrorCS", {"start": v(1130, 929.53) * mm, "end": v(1130, 1010.36) * mm});
            skLineSegment(sketch, "E820.MirrorCS", {"start": v(950, 1010.36) * mm, "end": v(880, 1050.78) * mm});
            skLineSegment(sketch, "E821.MirrorCS", {"start": v(410, 871.8) * mm, "end": v(410, 790.97) * mm});
            skLineSegment(sketch, "E822.MirrorCS", {"start": v(330, 652.4) * mm, "end": v(330, 733.23) * mm});
            skLineSegment(sketch, "E823.MirrorCS", {"start": v(640, 1027.68) * mm, "end": v(710, 1068.1) * mm});
            skLineSegment(sketch, "E824.MirrorCS", {"start": v(1120, 635.09) * mm, "end": v(1050, 594.67) * mm});
            skLineSegment(sketch, "E825.MirrorCS", {"start": v(-640, 635.09) * mm, "end": v(-570, 594.67) * mm});
            skLineSegment(sketch, "E826.MirrorCS", {"start": v(330, 733.23) * mm, "end": v(400, 773.65) * mm});
            skLineSegment(sketch, "E827.MirrorCS", {"start": v(330, 1010.36) * mm, "end": v(330, 929.53) * mm});
            skLineSegment(sketch, "E828.MirrorCS", {"start": v(-90, 871.8) * mm, "end": v(-160, 912.21) * mm});
            skLineSegment(sketch, "E829.MirrorCS", {"start": v(-390, 1068.1) * mm, "end": v(-320, 1027.68) * mm});
            skLineSegment(sketch, "E830.MirrorCS", {"start": v(-230, 790.97) * mm, "end": v(-160, 750.56) * mm});
            skLineSegment(sketch, "E831.MirrorCS", {"start": v(160, 1189.34) * mm, "end": v(230, 1148.93) * mm});
            skLineSegment(sketch, "E832.MirrorCS", {"start": v(0, 635.09) * mm, "end": v(70, 594.67) * mm});
            skLineSegment(sketch, "E833.MirrorCS", {"start": v(960, 1027.68) * mm, "end": v(1030, 1068.1) * mm});
            skLineSegment(sketch, "E834.MirrorCS", {"start": v(250, 594.67) * mm, "end": v(320, 635.09) * mm});
            skLineSegment(sketch, "E835.MirrorCS", {"start": v(1050, 871.8) * mm, "end": v(1050, 790.97) * mm});
            skLineSegment(sketch, "E836.MirrorCS", {"start": v(560, 612) * mm, "end": v(630, 652.4) * mm});
            skLineSegment(sketch, "E837.MirrorCS", {"start": v(1050, 1148.93) * mm, "end": v(1120, 1189.34) * mm});
            skLineSegment(sketch, "E838.MirrorCS", {"start": v(720, 773.65) * mm, "end": v(790, 733.23) * mm});
            skLineSegment(sketch, "E839.MirrorCS", {"start": v(1040, 773.65) * mm, "end": v(1110, 733.23) * mm});
            skLineSegment(sketch, "E840.MirrorCS", {"start": v(630, 1010.36) * mm, "end": v(630, 929.53) * mm});
            skLineSegment(sketch, "E841.MirrorCS", {"start": v(-730, 1068.1) * mm, "end": v(-790, 1033.46) * mm});
            skLineSegment(sketch, "E842.MirrorCS", {"start": v(800, 912.21) * mm, "end": v(730, 871.8) * mm});
            skLineSegment(sketch, "E843.MirrorCS", {"start": v(890, 594.67) * mm, "end": v(960, 635.09) * mm});
            skLineSegment(sketch, "E844.MirrorCS", {"start": v(480, 912.21) * mm, "end": v(410, 871.8) * mm});
            skLineSegment(sketch, "E845.MirrorCS", {"start": v(-400, 612) * mm, "end": v(-470, 652.4) * mm});
            skLineSegment(sketch, "E846.MirrorCS", {"start": v(960, 1189.34) * mm, "end": v(890, 1148.93) * mm});
            skLineSegment(sketch, "E847.MirrorCS", {"start": v(-640, 1466.47) * mm, "end": v(-710, 1426.06) * mm});
            skLineSegment(sketch, "E848.MirrorCS", {"start": v(-400, 1882.16) * mm, "end": v(-470, 1841.75) * mm});
            skLineSegment(sketch, "E849.MirrorCS", {"start": v(400, 1327.9) * mm, "end": v(470, 1287.5) * mm});
            skLineSegment(sketch, "E850.MirrorCS", {"start": v(790, 1841.75) * mm, "end": v(720, 1882.16) * mm});
            skLineSegment(sketch, "E851.MirrorCS", {"start": v(400, 1443.38) * mm, "end": v(330, 1483.8) * mm});
            skLineSegment(sketch, "E852.MirrorCS", {"start": v(-650, 1841.75) * mm, "end": v(-720, 1882.16) * mm});
            skLineSegment(sketch, "E853.MirrorCS", {"start": v(1040, 1443.38) * mm, "end": v(970, 1483.8) * mm});
            skLineSegment(sketch, "E854.MirrorCS", {"start": v(640, 1466.47) * mm, "end": v(570, 1426.06) * mm});
            skLineSegment(sketch, "E855.MirrorCS", {"start": v(1190, 1322.13) * mm, "end": v(1130, 1287.5) * mm});
            skLineSegment(sketch, "E856.MirrorCS", {"start": v(630, 1287.5) * mm, "end": v(560, 1327.9) * mm});
            skLineSegment(sketch, "E857.MirrorCS", {"start": v(-570, 1622.35) * mm, "end": v(-640, 1581.94) * mm});
            skLineSegment(sketch, "E858.MirrorCS", {"start": v(-790, 1841.75) * mm, "end": v(-720, 1882.16) * mm});
            skLineSegment(sketch, "E859.MirrorCS", {"start": v(1110, 1841.75) * mm, "end": v(1040, 1882.16) * mm});
            skLineSegment(sketch, "E860.MirrorCS", {"start": v(-560, 1882.16) * mm, "end": v(-490, 1841.75) * mm});
            skLineSegment(sketch, "E861.MirrorCS", {"start": v(-320, 1581.94) * mm, "end": v(-250, 1622.35) * mm});
            skLineSegment(sketch, "E862.MirrorCS", {"start": v(490, 1287.5) * mm, "end": v(560, 1327.9) * mm});
            skLineSegment(sketch, "E863.MirrorCS", {"start": v(-150, 1841.75) * mm, "end": v(-80, 1882.16) * mm});
            skLineSegment(sketch, "E864.MirrorCS", {"start": v(-630, 1287.5) * mm, "end": v(-560, 1327.9) * mm});
            skLineSegment(sketch, "E865.MirrorCS", {"start": v(-80, 1327.9) * mm, "end": v(-10, 1287.5) * mm});
            skLineSegment(sketch, "E866.MirrorCS", {"start": v(10, 1483.8) * mm, "end": v(80, 1443.38) * mm});
            skLineSegment(sketch, "E867.MirrorCS", {"start": v(240, 1882.16) * mm, "end": v(310, 1841.75) * mm});
            skLineSegment(sketch, "E868.MirrorCS", {"start": v(70, 1622.35) * mm, "end": v(0, 1581.94) * mm});
            skLineSegment(sketch, "E869.MirrorCS", {"start": v(960, 1581.94) * mm, "end": v(1030, 1622.35) * mm});
            skLineSegment(sketch, "E870.MirrorCS", {"start": v(-400, 1443.38) * mm, "end": v(-470, 1483.8) * mm});
            skLineSegment(sketch, "E871.MirrorCS", {"start": v(-720, 1327.9) * mm, "end": v(-790, 1287.5) * mm});
            skLineSegment(sketch, "E872.MirrorCS", {"start": v(-150, 1483.8) * mm, "end": v(-80, 1443.38) * mm});
            skLineSegment(sketch, "E873.MirrorCS", {"start": v(890, 1622.35) * mm, "end": v(960, 1581.94) * mm});
            skLineSegment(sketch, "E874.MirrorCS", {"start": v(810, 1841.75) * mm, "end": v(880, 1882.16) * mm});
            skLineSegment(sketch, "E875.MirrorCS", {"start": v(-400, 1327.9) * mm, "end": v(-330, 1287.5) * mm});
            skLineSegment(sketch, "E876.MirrorCS", {"start": v(650, 1841.75) * mm, "end": v(720, 1882.16) * mm});
            skLineSegment(sketch, "E877.MirrorCS", {"start": v(560, 1882.16) * mm, "end": v(630, 1841.75) * mm});
            skLineSegment(sketch, "E878.MirrorCS", {"start": v(640, 1466.47) * mm, "end": v(710, 1426.06) * mm});
            skLineSegment(sketch, "E879.MirrorCS", {"start": v(-470, 1287.5) * mm, "end": v(-400, 1327.9) * mm});
            skLineSegment(sketch, "E880.MirrorCS", {"start": v(-330, 1483.8) * mm, "end": v(-400, 1443.38) * mm});
            skLineSegment(sketch, "E881.MirrorCS", {"start": v(470, 1483.8) * mm, "end": v(400, 1443.38) * mm});
            skLineSegment(sketch, "E882.MirrorCS", {"start": v(80, 1882.16) * mm, "end": v(150, 1841.75) * mm});
            skLineSegment(sketch, "E883.MirrorCS", {"start": v(-70, 1426.06) * mm, "end": v(0, 1466.47) * mm});
            skLineSegment(sketch, "E884.MirrorCS", {"start": v(-630, 1841.75) * mm, "end": v(-560, 1882.16) * mm});
            skLineSegment(sketch, "E885.MirrorCS", {"start": v(-70, 1622.35) * mm, "end": v(0, 1581.94) * mm});
            skLineSegment(sketch, "E886.MirrorCS", {"start": v(890, 1426.06) * mm, "end": v(960, 1466.47) * mm});
            skLineSegment(sketch, "E887.MirrorCS", {"start": v(550, 1426.06) * mm, "end": v(480, 1466.47) * mm});
            skLineSegment(sketch, "E888.MirrorCS", {"start": v(10, 1287.5) * mm, "end": v(80, 1327.9) * mm});
            skLineSegment(sketch, "E889.MirrorCS", {"start": v(640, 1581.94) * mm, "end": v(710, 1622.35) * mm});
            skLineSegment(sketch, "E890.MirrorCS", {"start": v(950, 1483.8) * mm, "end": v(880, 1443.38) * mm});
            skLineSegment(sketch, "E891.MirrorCS", {"start": v(950, 1841.75) * mm, "end": v(880, 1882.16) * mm});
            skLineSegment(sketch, "E892.MirrorCS", {"start": v(880, 1327.9) * mm, "end": v(950, 1287.5) * mm});
            skLineSegment(sketch, "E893.MirrorCS", {"start": v(1040, 1882.16) * mm, "end": v(970, 1841.75) * mm});
            skLineSegment(sketch, "E894.MirrorCS", {"start": v(960, 1466.47) * mm, "end": v(1030, 1426.06) * mm});
            skLineSegment(sketch, "E895.MirrorCS", {"start": v(-730, 1426.06) * mm, "end": v(-790, 1460.7) * mm});
            skLineSegment(sketch, "E896.MirrorCS", {"start": v(-240, 1443.38) * mm, "end": v(-310, 1483.8) * mm});
            skLineSegment(sketch, "E897.MirrorCS", {"start": v(-410, 1426.06) * mm, "end": v(-480, 1466.47) * mm});
            skLineSegment(sketch, "E898.MirrorCS", {"start": v(-160, 1581.94) * mm, "end": v(-90, 1622.35) * mm});
            skLineSegment(sketch, "E899.MirrorCS", {"start": v(870, 1426.06) * mm, "end": v(800, 1466.47) * mm});
            skLineSegment(sketch, "E900.MirrorCS", {"start": v(1190, 1449.15) * mm, "end": v(1130, 1483.8) * mm});
            skLineSegment(sketch, "E901.MirrorCS", {"start": v(870, 1622.35) * mm, "end": v(800, 1581.94) * mm});
            skLineSegment(sketch, "E902.MirrorCS", {"start": v(320, 1581.94) * mm, "end": v(250, 1622.35) * mm});
            skLineSegment(sketch, "E903.MirrorCS", {"start": v(-720, 1443.38) * mm, "end": v(-650, 1483.8) * mm});
            skLineSegment(sketch, "E904.MirrorCS", {"start": v(-570, 1426.06) * mm, "end": v(-640, 1466.47) * mm});
            skLineSegment(sketch, "E905.MirrorCS", {"start": v(-560, 1443.38) * mm, "end": v(-630, 1483.8) * mm});
            skLineSegment(sketch, "E906.MirrorCS", {"start": v(10, 1841.75) * mm, "end": v(80, 1882.16) * mm});
            skLineSegment(sketch, "E907.MirrorCS", {"start": v(1040, 1443.38) * mm, "end": v(1110, 1483.8) * mm});
            skLineSegment(sketch, "E908.MirrorCS", {"start": v(-560, 1443.38) * mm, "end": v(-490, 1483.8) * mm});
            skLineSegment(sketch, "E909.MirrorCS", {"start": v(480, 1466.47) * mm, "end": v(410, 1426.06) * mm});
            skLineSegment(sketch, "E910.MirrorCS", {"start": v(-150, 1287.5) * mm, "end": v(-80, 1327.9) * mm});
            skLineSegment(sketch, "E911.MirrorCS", {"start": v(330, 1287.5) * mm, "end": v(400, 1327.9) * mm});
            skLineSegment(sketch, "E912.MirrorCS", {"start": v(150, 1287.5) * mm, "end": v(80, 1327.9) * mm});
            skLineSegment(sketch, "E913.MirrorCS", {"start": v(-790, 1483.8) * mm, "end": v(-720, 1443.38) * mm});
            skLineSegment(sketch, "E914.MirrorCS", {"start": v(570, 1622.35) * mm, "end": v(640, 1581.94) * mm});
            skLineSegment(sketch, "E915.MirrorCS", {"start": v(0, 1466.47) * mm, "end": v(70, 1426.06) * mm});
            skLineSegment(sketch, "E916.MirrorCS", {"start": v(150, 1483.8) * mm, "end": v(80, 1443.38) * mm});
            skLineSegment(sketch, "E917.MirrorCS", {"start": v(480, 1581.94) * mm, "end": v(410, 1622.35) * mm});
            skLineSegment(sketch, "E918.MirrorCS", {"start": v(320, 1466.47) * mm, "end": v(250, 1426.06) * mm});
            skLineSegment(sketch, "E919.MirrorCS", {"start": v(-480, 1581.94) * mm, "end": v(-410, 1622.35) * mm});
            skLineSegment(sketch, "E920.MirrorCS", {"start": v(-720, 1327.9) * mm, "end": v(-650, 1287.5) * mm});
            skLineSegment(sketch, "E921.MirrorCS", {"start": v(1120, 1581.94) * mm, "end": v(1050, 1622.35) * mm});
            skLineSegment(sketch, "E922.MirrorCS", {"start": v(320, 1581.94) * mm, "end": v(390, 1622.35) * mm});
            skLineSegment(sketch, "E923.MirrorCS", {"start": v(560, 1443.38) * mm, "end": v(630, 1483.8) * mm});
            skLineSegment(sketch, "E924.MirrorCS", {"start": v(240, 1443.38) * mm, "end": v(170, 1483.8) * mm});
            skLineSegment(sketch, "E925.MirrorCS", {"start": v(-330, 1841.75) * mm, "end": v(-400, 1882.16) * mm});
            skLineSegment(sketch, "E926.MirrorCS", {"start": v(560, 1882.16) * mm, "end": v(490, 1841.75) * mm});
            skLineSegment(sketch, "E927.MirrorCS", {"start": v(240, 1443.38) * mm, "end": v(310, 1483.8) * mm});
            skLineSegment(sketch, "E928.MirrorCS", {"start": v(1120, 1466.47) * mm, "end": v(1050, 1426.06) * mm});
            skLineSegment(sketch, "E929.MirrorCS", {"start": v(1120, 1581.94) * mm, "end": v(1190, 1622.35) * mm});
            skLineSegment(sketch, "E930.MirrorCS", {"start": v(720, 1327.9) * mm, "end": v(790, 1287.5) * mm});
            skLineSegment(sketch, "E931.MirrorCS", {"start": v(-490, 1287.5) * mm, "end": v(-560, 1327.9) * mm});
            skLineSegment(sketch, "E932.MirrorCS", {"start": v(800, 1581.94) * mm, "end": v(730, 1622.35) * mm});
            skLineSegment(sketch, "E933.MirrorCS", {"start": v(1040, 1327.9) * mm, "end": v(1110, 1287.5) * mm});
            skLineSegment(sketch, "E934.MirrorCS", {"start": v(-160, 1466.47) * mm, "end": v(-90, 1426.06) * mm});
            skLineSegment(sketch, "E935.MirrorCS", {"start": v(560, 1443.38) * mm, "end": v(490, 1483.8) * mm});
            skLineSegment(sketch, "E936.MirrorCS", {"start": v(-170, 1483.8) * mm, "end": v(-240, 1443.38) * mm});
            skLineSegment(sketch, "E937.MirrorCS", {"start": v(810, 1483.8) * mm, "end": v(880, 1443.38) * mm});
            skLineSegment(sketch, "E938.MirrorCS", {"start": v(-10, 1841.75) * mm, "end": v(-80, 1882.16) * mm});
            skLineSegment(sketch, "E939.MirrorCS", {"start": v(-240, 1882.16) * mm, "end": v(-310, 1841.75) * mm});
            skLineSegment(sketch, "E940.MirrorCS", {"start": v(1120, 1466.47) * mm, "end": v(1190, 1426.06) * mm});
            skLineSegment(sketch, "E941.MirrorCS", {"start": v(240, 1882.16) * mm, "end": v(170, 1841.75) * mm});
            skLineSegment(sketch, "E942.MirrorCS", {"start": v(-550, 1622.35) * mm, "end": v(-480, 1581.94) * mm});
            skLineSegment(sketch, "E943.MirrorCS", {"start": v(400, 1882.16) * mm, "end": v(470, 1841.75) * mm});
            skLineSegment(sketch, "E944.MirrorCS", {"start": v(-170, 1287.5) * mm, "end": v(-240, 1327.9) * mm});
            skLineSegment(sketch, "E945.MirrorCS", {"start": v(-160, 1581.94) * mm, "end": v(-230, 1622.35) * mm});
            skLineSegment(sketch, "E946.MirrorCS", {"start": v(160, 1581.94) * mm, "end": v(230, 1622.35) * mm});
            skLineSegment(sketch, "E947.MirrorCS", {"start": v(1040, 1327.9) * mm, "end": v(970, 1287.5) * mm});
            skLineSegment(sketch, "E948.MirrorCS", {"start": v(-250, 1426.06) * mm, "end": v(-320, 1466.47) * mm});
            skLineSegment(sketch, "E949.MirrorCS", {"start": v(-480, 1466.47) * mm, "end": v(-550, 1426.06) * mm});
            skLineSegment(sketch, "E950.MirrorCS", {"start": v(-390, 1622.35) * mm, "end": v(-320, 1581.94) * mm});
            skLineSegment(sketch, "E951.MirrorCS", {"start": v(330, 1841.75) * mm, "end": v(400, 1882.16) * mm});
            skLineSegment(sketch, "E952.MirrorCS", {"start": v(810, 1287.5) * mm, "end": v(880, 1327.9) * mm});
            skLineSegment(sketch, "E953.MirrorCS", {"start": v(-390, 1426.06) * mm, "end": v(-320, 1466.47) * mm});
            skLineSegment(sketch, "E954.MirrorCS", {"start": v(160, 1466.47) * mm, "end": v(90, 1426.06) * mm});
            skLineSegment(sketch, "E955.MirrorCS", {"start": v(790, 1483.8) * mm, "end": v(720, 1443.38) * mm});
            skLineSegment(sketch, "E956.MirrorCS", {"start": v(160, 1581.94) * mm, "end": v(90, 1622.35) * mm});
            skLineSegment(sketch, "E957.MirrorCS", {"start": v(-160, 1466.47) * mm, "end": v(-230, 1426.06) * mm});
            skLineSegment(sketch, "E958.MirrorCS", {"start": v(480, 1581.94) * mm, "end": v(550, 1622.35) * mm});
            skLineSegment(sketch, "E959.MirrorCS", {"start": v(720, 1327.9) * mm, "end": v(650, 1287.5) * mm});
            skLineSegment(sketch, "E960.MirrorCS", {"start": v(240, 1327.9) * mm, "end": v(310, 1287.5) * mm});
            skLineSegment(sketch, "E961.MirrorCS", {"start": v(-240, 1882.16) * mm, "end": v(-170, 1841.75) * mm});
            skLineSegment(sketch, "E962.MirrorCS", {"start": v(-310, 1287.5) * mm, "end": v(-240, 1327.9) * mm});
            skLineSegment(sketch, "E963.MirrorCS", {"start": v(-10, 1483.8) * mm, "end": v(-80, 1443.38) * mm});
            skLineSegment(sketch, "E964.MirrorCS", {"start": v(170, 1287.5) * mm, "end": v(240, 1327.9) * mm});
            skLineSegment(sketch, "E965.MirrorCS", {"start": v(-710, 1622.35) * mm, "end": v(-640, 1581.94) * mm});
            skLineSegment(sketch, "E966.MirrorCS", {"start": v(650, 1483.8) * mm, "end": v(720, 1443.38) * mm});
            skLineSegment(sketch, "E967.MirrorCS", {"start": v(730, 1426.06) * mm, "end": v(800, 1466.47) * mm});
            skLineSegment(sketch, "E968.MirrorCS", {"start": v(230, 1426.06) * mm, "end": v(160, 1466.47) * mm});
            skLineSegment(sketch, "E969.MirrorCS", {"start": v(320, 1466.47) * mm, "end": v(390, 1426.06) * mm});
            skLineSegment(sketch, "E970.MirrorCS", {"start": v(-730, 1622.35) * mm, "end": v(-790, 1587.71) * mm});
            skLineSegment(sketch, "E971.MirrorCS", {"start": v(-80, 1882.16) * mm, "end": v(-10, 1841.75) * mm});
            skLineSegment(sketch, "E972.MirrorCS", {"start": v(1110, 1206.66) * mm, "end": v(1040, 1166.25) * mm});
            skLineSegment(sketch, "E973.MirrorCS", {"start": v(240, 1720.5) * mm, "end": v(170, 1760.92) * mm});
            skLineSegment(sketch, "E974.MirrorCS", {"start": v(400, 1443.38) * mm, "end": v(470, 1483.8) * mm});
            skLineSegment(sketch, "E975.MirrorCS", {"start": v(570, 1426.06) * mm, "end": v(570, 1345.23) * mm});
            skLineSegment(sketch, "E976.MirrorCS", {"start": v(630, 1760.92) * mm, "end": v(630, 1841.75) * mm});
            skLineSegment(sketch, "E977.MirrorCS", {"start": v(80, 1605.03) * mm, "end": v(150, 1564.62) * mm});
            skLineSegment(sketch, "E978.MirrorCS", {"start": v(870, 1622.35) * mm, "end": v(870, 1703.18) * mm});
            skLineSegment(sketch, "E979.MirrorCS", {"start": v(490, 1841.75) * mm, "end": v(490, 1760.92) * mm});
            skLineSegment(sketch, "E980.MirrorCS", {"start": v(890, 1622.35) * mm, "end": v(890, 1703.18) * mm});
            skLineSegment(sketch, "E981.MirrorCS", {"start": v(170, 1841.75) * mm, "end": v(240, 1882.16) * mm});
            skLineSegment(sketch, "E982.MirrorCS", {"start": v(410, 1703.18) * mm, "end": v(410, 1622.35) * mm});
            skLineSegment(sketch, "E983.MirrorCS", {"start": v(570, 1622.35) * mm, "end": v(570, 1703.18) * mm});
            skLineSegment(sketch, "E984.MirrorCS", {"start": v(720, 1882.16) * mm, "end": v(650, 1841.75) * mm});
            skLineSegment(sketch, "E985.MirrorCS", {"start": v(1130, 1287.5) * mm, "end": v(1190, 1322.13) * mm});
            skLineSegment(sketch, "E986.MirrorCS", {"start": v(310, 1287.5) * mm, "end": v(310, 1206.66) * mm});
            skLineSegment(sketch, "E987.MirrorCS", {"start": v(400, 1166.25) * mm, "end": v(330, 1206.66) * mm});
            skLineSegment(sketch, "E988.MirrorCS", {"start": v(-570, 1345.23) * mm, "end": v(-570, 1426.06) * mm});
            skLineSegment(sketch, "E989.MirrorCS", {"start": v(-490, 1760.92) * mm, "end": v(-490, 1841.75) * mm});
            skLineSegment(sketch, "E990.MirrorCS", {"start": v(560, 1720.5) * mm, "end": v(630, 1760.92) * mm});
            skLineSegment(sketch, "E991.MirrorCS", {"start": v(330, 1483.8) * mm, "end": v(400, 1443.38) * mm});
            skLineSegment(sketch, "E992.MirrorCS", {"start": v(870, 1148.93) * mm, "end": v(800, 1189.34) * mm});
            skLineSegment(sketch, "E993.MirrorCS", {"start": v(-330, 1287.5) * mm, "end": v(-330, 1206.66) * mm});
            skLineSegment(sketch, "E994.MirrorCS", {"start": v(400, 1605.03) * mm, "end": v(330, 1564.62) * mm});
            skLineSegment(sketch, "E995.MirrorCS", {"start": v(-730, 1345.23) * mm, "end": v(-790, 1310.59) * mm});
            skLineSegment(sketch, "E996.MirrorCS", {"start": v(-390, 1426.06) * mm, "end": v(-390, 1345.23) * mm});
            skLineSegment(sketch, "E997.MirrorCS", {"start": v(250, 1622.35) * mm, "end": v(250, 1703.18) * mm});
            skLineSegment(sketch, "E998.MirrorCS", {"start": v(640, 1189.34) * mm, "end": v(710, 1148.93) * mm});
            skLineSegment(sketch, "E999.MirrorCS", {"start": v(-470, 1564.62) * mm, "end": v(-470, 1483.8) * mm});
            skLineSegment(sketch, "E1000.MirrorCS", {"start": v(-10, 1760.92) * mm, "end": v(-10, 1841.75) * mm});
            skLineSegment(sketch, "E1001.MirrorCS", {"start": v(890, 1148.93) * mm, "end": v(960, 1189.34) * mm});
            skLineSegment(sketch, "E1002.MirrorCS", {"start": v(310, 1841.75) * mm, "end": v(240, 1882.16) * mm});
            skLineSegment(sketch, "E1003.MirrorCS", {"start": v(710, 1426.06) * mm, "end": v(640, 1466.47) * mm});
            skLineSegment(sketch, "E1004.MirrorCS", {"start": v(1110, 1287.5) * mm, "end": v(1040, 1327.9) * mm});
            skLineSegment(sketch, "E1005.MirrorCS", {"start": v(-150, 1483.8) * mm, "end": v(-150, 1564.62) * mm});
            skLineSegment(sketch, "E1006.MirrorCS", {"start": v(230, 1622.35) * mm, "end": v(230, 1703.18) * mm});
            skLineSegment(sketch, "E1007.MirrorCS", {"start": v(240, 1166.25) * mm, "end": v(170, 1206.66) * mm});
            skLineSegment(sketch, "E1008.MirrorCS", {"start": v(560, 1166.25) * mm, "end": v(630, 1206.66) * mm});
            skLineSegment(sketch, "E1009.MirrorCS", {"start": v(-720, 1882.16) * mm, "end": v(-650, 1841.75) * mm});
            skLineSegment(sketch, "E1010.MirrorCS", {"start": v(70, 1345.23) * mm, "end": v(70, 1426.06) * mm});
            skLineSegment(sketch, "E1011.MirrorCS", {"start": v(150, 1841.75) * mm, "end": v(80, 1882.16) * mm});
            skLineSegment(sketch, "E1012.MirrorCS", {"start": v(710, 1703.18) * mm, "end": v(710, 1622.35) * mm});
            skLineSegment(sketch, "E1013.MirrorCS", {"start": v(-150, 1287.5) * mm, "end": v(-150, 1206.66) * mm});
            skLineSegment(sketch, "E1014.MirrorCS", {"start": v(90, 1622.35) * mm, "end": v(160, 1581.94) * mm});
            skLineSegment(sketch, "E1015.MirrorCS", {"start": v(-710, 1703.18) * mm, "end": v(-640, 1743.6) * mm});
            skLineSegment(sketch, "E1016.MirrorCS", {"start": v(-630, 1564.62) * mm, "end": v(-560, 1605.03) * mm});
            skLineSegment(sketch, "E1017.MirrorCS", {"start": v(-550, 1426.06) * mm, "end": v(-480, 1466.47) * mm});
            skLineSegment(sketch, "E1018.MirrorCS", {"start": v(-240, 1443.38) * mm, "end": v(-170, 1483.8) * mm});
            skLineSegment(sketch, "E1019.MirrorCS", {"start": v(490, 1206.66) * mm, "end": v(560, 1166.25) * mm});
            skLineSegment(sketch, "E1020.MirrorCS", {"start": v(-790, 1564.62) * mm, "end": v(-720, 1605.03) * mm});
            skLineSegment(sketch, "E1021.MirrorCS", {"start": v(490, 1564.62) * mm, "end": v(560, 1605.03) * mm});
            skLineSegment(sketch, "E1022.MirrorCS", {"start": v(470, 1841.75) * mm, "end": v(470, 1760.92) * mm});
            skLineSegment(sketch, "E1023.MirrorCS", {"start": v(-10, 1287.5) * mm, "end": v(-80, 1327.9) * mm});
            skLineSegment(sketch, "E1024.MirrorCS", {"start": v(-70, 1345.23) * mm, "end": v(0, 1304.81) * mm});
            skLineSegment(sketch, "E1025.MirrorCS", {"start": v(960, 1743.6) * mm, "end": v(1030, 1703.18) * mm});
            skLineSegment(sketch, "E1026.MirrorCS", {"start": v(-410, 1703.18) * mm, "end": v(-480, 1743.6) * mm});
            skLineSegment(sketch, "E1027.MirrorCS", {"start": v(470, 1564.62) * mm, "end": v(400, 1605.03) * mm});
            skLineSegment(sketch, "E1028.MirrorCS", {"start": v(-330, 1564.62) * mm, "end": v(-400, 1605.03) * mm});
            skLineSegment(sketch, "E1029.MirrorCS", {"start": v(80, 1327.9) * mm, "end": v(10, 1287.5) * mm});
            skLineSegment(sketch, "E1030.MirrorCS", {"start": v(970, 1760.92) * mm, "end": v(970, 1841.75) * mm});
            skLineSegment(sketch, "E1031.MirrorCS", {"start": v(950, 1760.92) * mm, "end": v(880, 1720.5) * mm});
            skLineSegment(sketch, "E1032.MirrorCS", {"start": v(170, 1760.92) * mm, "end": v(170, 1841.75) * mm});
            skLineSegment(sketch, "E1033.MirrorCS", {"start": v(-640, 1581.94) * mm, "end": v(-570, 1622.35) * mm});
            skLineSegment(sketch, "E1034.MirrorCS", {"start": v(-550, 1345.23) * mm, "end": v(-550, 1426.06) * mm});
            skLineSegment(sketch, "E1035.MirrorCS", {"start": v(-160, 1304.81) * mm, "end": v(-230, 1345.23) * mm});
            skLineSegment(sketch, "E1036.MirrorCS", {"start": v(-240, 1327.9) * mm, "end": v(-310, 1287.5) * mm});
            skLineSegment(sketch, "E1037.MirrorCS", {"start": v(470, 1206.66) * mm, "end": v(400, 1166.25) * mm});
            skLineSegment(sketch, "E1038.MirrorCS", {"start": v(250, 1148.93) * mm, "end": v(320, 1189.34) * mm});
            skLineSegment(sketch, "E1039.MirrorCS", {"start": v(-320, 1466.47) * mm, "end": v(-250, 1426.06) * mm});
            skLineSegment(sketch, "E1040.MirrorCS", {"start": v(90, 1345.23) * mm, "end": v(90, 1426.06) * mm});
            skLineSegment(sketch, "E1041.MirrorCS", {"start": v(650, 1760.92) * mm, "end": v(720, 1720.5) * mm});
            skLineSegment(sketch, "E1042.MirrorCS", {"start": v(160, 1466.47) * mm, "end": v(230, 1426.06) * mm});
            skLineSegment(sketch, "E1043.MirrorCS", {"start": v(-230, 1345.23) * mm, "end": v(-230, 1426.06) * mm});
            skLineSegment(sketch, "E1044.MirrorCS", {"start": v(490, 1760.92) * mm, "end": v(560, 1720.5) * mm});
            skLineSegment(sketch, "E1045.MirrorCS", {"start": v(1130, 1483.8) * mm, "end": v(1190, 1449.15) * mm});
            skLineSegment(sketch, "E1046.MirrorCS", {"start": v(870, 1703.18) * mm, "end": v(800, 1743.6) * mm});
            skLineSegment(sketch, "E1047.MirrorCS", {"start": v(800, 1466.47) * mm, "end": v(730, 1426.06) * mm});
            skLineSegment(sketch, "E1048.MirrorCS", {"start": v(960, 1189.34) * mm, "end": v(1030, 1148.93) * mm});
            skLineSegment(sketch, "E1049.MirrorCS", {"start": v(-70, 1426.06) * mm, "end": v(-70, 1345.23) * mm});
            skLineSegment(sketch, "E1050.MirrorCS", {"start": v(0, 1581.94) * mm, "end": v(70, 1622.35) * mm});
            skLineSegment(sketch, "E1051.MirrorCS", {"start": v(720, 1443.38) * mm, "end": v(790, 1483.8) * mm});
            skLineSegment(sketch, "E1052.MirrorCS", {"start": v(650, 1206.66) * mm, "end": v(720, 1166.25) * mm});
            skLineSegment(sketch, "E1053.MirrorCS", {"start": v(710, 1345.23) * mm, "end": v(710, 1426.06) * mm});
            skLineSegment(sketch, "E1054.MirrorCS", {"start": v(480, 1304.81) * mm, "end": v(410, 1345.23) * mm});
            skLineSegment(sketch, "E1055.MirrorCS", {"start": v(950, 1287.5) * mm, "end": v(880, 1327.9) * mm});
            skLineSegment(sketch, "E1056.MirrorCS", {"start": v(-630, 1841.75) * mm, "end": v(-630, 1760.92) * mm});
            skLineSegment(sketch, "E1057.MirrorCS", {"start": v(-490, 1564.62) * mm, "end": v(-490, 1483.8) * mm});
            skLineSegment(sketch, "E1058.MirrorCS", {"start": v(-250, 1345.23) * mm, "end": v(-250, 1426.06) * mm});
            skLineSegment(sketch, "E1059.MirrorCS", {"start": v(720, 1605.03) * mm, "end": v(790, 1564.62) * mm});
            skLineSegment(sketch, "E1060.MirrorCS", {"start": v(160, 1304.81) * mm, "end": v(90, 1345.23) * mm});
            skLineSegment(sketch, "E1061.MirrorCS", {"start": v(-80, 1443.38) * mm, "end": v(-150, 1483.8) * mm});
            skLineSegment(sketch, "E1062.MirrorCS", {"start": v(330, 1760.92) * mm, "end": v(330, 1841.75) * mm});
            skLineSegment(sketch, "E1063.MirrorCS", {"start": v(470, 1287.5) * mm, "end": v(470, 1206.66) * mm});
            skLineSegment(sketch, "E1064.MirrorCS", {"start": v(880, 1166.25) * mm, "end": v(810, 1206.66) * mm});
            skLineSegment(sketch, "E1065.MirrorCS", {"start": v(890, 1426.06) * mm, "end": v(890, 1345.23) * mm});
            skLineSegment(sketch, "E1066.MirrorCS", {"start": v(1050, 1703.18) * mm, "end": v(1050, 1622.35) * mm});
            skLineSegment(sketch, "E1067.MirrorCS", {"start": v(890, 1345.23) * mm, "end": v(960, 1304.81) * mm});
            skLineSegment(sketch, "E1068.MirrorCS", {"start": v(1110, 1841.75) * mm, "end": v(1110, 1760.92) * mm});
            skLineSegment(sketch, "E1069.MirrorCS", {"start": v(-790, 1460.7) * mm, "end": v(-730, 1426.06) * mm});
            skLineSegment(sketch, "E1070.MirrorCS", {"start": v(470, 1760.92) * mm, "end": v(400, 1720.5) * mm});
            skLineSegment(sketch, "E1071.MirrorCS", {"start": v(1190, 1622.35) * mm, "end": v(1120, 1581.94) * mm});
            skLineSegment(sketch, "E1072.MirrorCS", {"start": v(-560, 1605.03) * mm, "end": v(-490, 1564.62) * mm});
            skLineSegment(sketch, "E1073.MirrorCS", {"start": v(-790, 1287.5) * mm, "end": v(-790, 1206.66) * mm});
            skLineSegment(sketch, "E1074.MirrorCS", {"start": v(-390, 1345.23) * mm, "end": v(-320, 1304.81) * mm});
            skLineSegment(sketch, "E1075.MirrorCS", {"start": v(-560, 1166.25) * mm, "end": v(-490, 1206.66) * mm});
            skLineSegment(sketch, "E1076.MirrorCS", {"start": v(320, 1304.81) * mm, "end": v(390, 1345.23) * mm});
            skLineSegment(sketch, "E1077.MirrorCS", {"start": v(-320, 1581.94) * mm, "end": v(-390, 1622.35) * mm});
            skLineSegment(sketch, "E1078.MirrorCS", {"start": v(-250, 1703.18) * mm, "end": v(-250, 1622.35) * mm});
            skLineSegment(sketch, "E1079.MirrorCS", {"start": v(-480, 1189.34) * mm, "end": v(-550, 1148.93) * mm});
            skLineSegment(sketch, "E1080.MirrorCS", {"start": v(390, 1622.35) * mm, "end": v(320, 1581.94) * mm});
            skLineSegment(sketch, "E1081.MirrorCS", {"start": v(960, 1581.94) * mm, "end": v(890, 1622.35) * mm});
            skLineSegment(sketch, "E1082.MirrorCS", {"start": v(1110, 1564.62) * mm, "end": v(1040, 1605.03) * mm});
            skLineSegment(sketch, "E1083.MirrorCS", {"start": v(-320, 1466.47) * mm, "end": v(-390, 1426.06) * mm});
            skLineSegment(sketch, "E1084.MirrorCS", {"start": v(880, 1605.03) * mm, "end": v(810, 1564.62) * mm});
            skLineSegment(sketch, "E1085.MirrorCS", {"start": v(0, 1743.6) * mm, "end": v(70, 1703.18) * mm});
            skLineSegment(sketch, "E1086.MirrorCS", {"start": v(880, 1882.16) * mm, "end": v(810, 1841.75) * mm});
            skLineSegment(sketch, "E1087.MirrorCS", {"start": v(170, 1206.66) * mm, "end": v(170, 1287.5) * mm});
            skLineSegment(sketch, "E1088.MirrorCS", {"start": v(-150, 1206.66) * mm, "end": v(-80, 1166.25) * mm});
            skLineSegment(sketch, "E1089.MirrorCS", {"start": v(0, 1581.94) * mm, "end": v(-70, 1622.35) * mm});
            skLineSegment(sketch, "E1090.MirrorCS", {"start": v(160, 1743.6) * mm, "end": v(90, 1703.18) * mm});
            skLineSegment(sketch, "E1091.MirrorCS", {"start": v(1030, 1345.23) * mm, "end": v(1030, 1426.06) * mm});
            skLineSegment(sketch, "E1092.MirrorCS", {"start": v(710, 1622.35) * mm, "end": v(640, 1581.94) * mm});
            skLineSegment(sketch, "E1093.MirrorCS", {"start": v(650, 1564.62) * mm, "end": v(720, 1605.03) * mm});
            skLineSegment(sketch, "E1094.MirrorCS", {"start": v(570, 1426.06) * mm, "end": v(640, 1466.47) * mm});
            skLineSegment(sketch, "E1095.MirrorCS", {"start": v(230, 1426.06) * mm, "end": v(230, 1345.23) * mm});
            skLineSegment(sketch, "E1096.MirrorCS", {"start": v(-80, 1720.5) * mm, "end": v(-10, 1760.92) * mm});
            skLineSegment(sketch, "E1097.MirrorCS", {"start": v(-630, 1483.8) * mm, "end": v(-560, 1443.38) * mm});
            skLineSegment(sketch, "E1098.MirrorCS", {"start": v(-630, 1287.5) * mm, "end": v(-630, 1206.66) * mm});
            skLineSegment(sketch, "E1099.MirrorCS", {"start": v(80, 1720.5) * mm, "end": v(150, 1760.92) * mm});
            skLineSegment(sketch, "E1100.MirrorCS", {"start": v(560, 1327.9) * mm, "end": v(630, 1287.5) * mm});
            skLineSegment(sketch, "E1101.MirrorCS", {"start": v(-400, 1166.25) * mm, "end": v(-470, 1206.66) * mm});
            skLineSegment(sketch, "E1102.MirrorCS", {"start": v(570, 1148.93) * mm, "end": v(640, 1189.34) * mm});
            skLineSegment(sketch, "E1103.MirrorCS", {"start": v(-330, 1287.5) * mm, "end": v(-400, 1327.9) * mm});
            skLineSegment(sketch, "E1104.MirrorCS", {"start": v(1120, 1304.81) * mm, "end": v(1050, 1345.23) * mm});
            skLineSegment(sketch, "E1105.MirrorCS", {"start": v(1110, 1483.8) * mm, "end": v(1110, 1564.62) * mm});
            skLineSegment(sketch, "E1106.MirrorCS", {"start": v(-410, 1622.35) * mm, "end": v(-480, 1581.94) * mm});
            skLineSegment(sketch, "E1107.MirrorCS", {"start": v(960, 1304.81) * mm, "end": v(1030, 1345.23) * mm});
            skLineSegment(sketch, "E1108.MirrorCS", {"start": v(-630, 1760.92) * mm, "end": v(-560, 1720.5) * mm});
            skLineSegment(sketch, "E1109.MirrorCS", {"start": v(-650, 1483.8) * mm, "end": v(-720, 1443.38) * mm});
            skLineSegment(sketch, "E1110.MirrorCS", {"start": v(-730, 1148.93) * mm, "end": v(-790, 1183.57) * mm});
            skLineSegment(sketch, "E1111.MirrorCS", {"start": v(880, 1443.38) * mm, "end": v(810, 1483.8) * mm});
            skLineSegment(sketch, "E1112.MirrorCS", {"start": v(10, 1483.8) * mm, "end": v(10, 1564.62) * mm});
            skLineSegment(sketch, "E1113.MirrorCS", {"start": v(1130, 1483.8) * mm, "end": v(1130, 1564.62) * mm});
            skLineSegment(sketch, "E1114.MirrorCS", {"start": v(550, 1345.23) * mm, "end": v(480, 1304.81) * mm});
            skLineSegment(sketch, "E1115.MirrorCS", {"start": v(1050, 1426.06) * mm, "end": v(1120, 1466.47) * mm});
            skLineSegment(sketch, "E1116.MirrorCS", {"start": v(-400, 1720.5) * mm, "end": v(-470, 1760.92) * mm});
            skLineSegment(sketch, "E1117.MirrorCS", {"start": v(-480, 1466.47) * mm, "end": v(-410, 1426.06) * mm});
            skLineSegment(sketch, "E1118.MirrorCS", {"start": v(310, 1206.66) * mm, "end": v(240, 1166.25) * mm});
            skLineSegment(sketch, "E1119.MirrorCS", {"start": v(1040, 1720.5) * mm, "end": v(970, 1760.92) * mm});
            skLineSegment(sketch, "E1120.MirrorCS", {"start": v(170, 1564.62) * mm, "end": v(170, 1483.8) * mm});
            skLineSegment(sketch, "E1121.MirrorCS", {"start": v(-80, 1166.25) * mm, "end": v(-10, 1206.66) * mm});
            skLineSegment(sketch, "E1122.MirrorCS", {"start": v(1030, 1622.35) * mm, "end": v(960, 1581.94) * mm});
            skLineSegment(sketch, "E1123.MirrorCS", {"start": v(-170, 1841.75) * mm, "end": v(-170, 1760.92) * mm});
            skLineSegment(sketch, "E1124.MirrorCS", {"start": v(470, 1841.75) * mm, "end": v(400, 1882.16) * mm});
            skLineSegment(sketch, "E1125.MirrorCS", {"start": v(1190, 1622.35) * mm, "end": v(1190, 1703.18) * mm});
            skLineSegment(sketch, "E1126.MirrorCS", {"start": v(10, 1287.5) * mm, "end": v(10, 1206.66) * mm});
            skLineSegment(sketch, "E1127.MirrorCS", {"start": v(490, 1483.8) * mm, "end": v(560, 1443.38) * mm});
            skLineSegment(sketch, "E1128.MirrorCS", {"start": v(-710, 1345.23) * mm, "end": v(-640, 1304.81) * mm});
            skLineSegment(sketch, "E1129.MirrorCS", {"start": v(-310, 1206.66) * mm, "end": v(-310, 1287.5) * mm});
            skLineSegment(sketch, "E1130.MirrorCS", {"start": v(-470, 1841.75) * mm, "end": v(-400, 1882.16) * mm});
            skLineSegment(sketch, "E1131.MirrorCS", {"start": v(950, 1483.8) * mm, "end": v(950, 1564.62) * mm});
            skLineSegment(sketch, "E1132.MirrorCS", {"start": v(10, 1206.66) * mm, "end": v(80, 1166.25) * mm});
            skLineSegment(sketch, "E1133.MirrorCS", {"start": v(-470, 1760.92) * mm, "end": v(-470, 1841.75) * mm});
            skLineSegment(sketch, "E1134.MirrorCS", {"start": v(970, 1206.66) * mm, "end": v(970, 1287.5) * mm});
            skLineSegment(sketch, "E1135.MirrorCS", {"start": v(-650, 1287.5) * mm, "end": v(-720, 1327.9) * mm});
            skLineSegment(sketch, "E1136.MirrorCS", {"start": v(650, 1287.5) * mm, "end": v(720, 1327.9) * mm});
            skLineSegment(sketch, "E1137.MirrorCS", {"start": v(880, 1327.9) * mm, "end": v(810, 1287.5) * mm});
            skLineSegment(sketch, "E1138.MirrorCS", {"start": v(230, 1703.18) * mm, "end": v(160, 1743.6) * mm});
            skLineSegment(sketch, "E1139.MirrorCS", {"start": v(790, 1760.92) * mm, "end": v(790, 1841.75) * mm});
            skLineSegment(sketch, "E1140.MirrorCS", {"start": v(170, 1483.8) * mm, "end": v(240, 1443.38) * mm});
            skLineSegment(sketch, "E1141.MirrorCS", {"start": v(-90, 1703.18) * mm, "end": v(-160, 1743.6) * mm});
            skLineSegment(sketch, "E1142.MirrorCS", {"start": v(80, 1443.38) * mm, "end": v(150, 1483.8) * mm});
            skLineSegment(sketch, "E1143.MirrorCS", {"start": v(1120, 1743.6) * mm, "end": v(1050, 1703.18) * mm});
            skLineSegment(sketch, "E1144.MirrorCS", {"start": v(240, 1327.9) * mm, "end": v(170, 1287.5) * mm});
            skLineSegment(sketch, "E1145.MirrorCS", {"start": v(-570, 1703.18) * mm, "end": v(-570, 1622.35) * mm});
            skLineSegment(sketch, "E1146.MirrorCS", {"start": v(790, 1287.5) * mm, "end": v(720, 1327.9) * mm});
            skLineSegment(sketch, "E1147.MirrorCS", {"start": v(1050, 1622.35) * mm, "end": v(1120, 1581.94) * mm});
            skLineSegment(sketch, "E1148.MirrorCS", {"start": v(1040, 1605.03) * mm, "end": v(970, 1564.62) * mm});
            skLineSegment(sketch, "E1149.MirrorCS", {"start": v(70, 1703.18) * mm, "end": v(70, 1622.35) * mm});
            skLineSegment(sketch, "E1150.MirrorCS", {"start": v(-410, 1148.93) * mm, "end": v(-480, 1189.34) * mm});
            skLineSegment(sketch, "E1151.MirrorCS", {"start": v(1130, 1206.66) * mm, "end": v(1190, 1172.02) * mm});
            skLineSegment(sketch, "E1152.MirrorCS", {"start": v(-330, 1841.75) * mm, "end": v(-330, 1760.92) * mm});
            skLineSegment(sketch, "E1153.MirrorCS", {"start": v(480, 1466.47) * mm, "end": v(550, 1426.06) * mm});
            skLineSegment(sketch, "E1154.MirrorCS", {"start": v(-640, 1466.47) * mm, "end": v(-570, 1426.06) * mm});
            skLineSegment(sketch, "E1155.MirrorCS", {"start": v(880, 1443.38) * mm, "end": v(950, 1483.8) * mm});
            skLineSegment(sketch, "E1156.MirrorCS", {"start": v(-490, 1483.8) * mm, "end": v(-560, 1443.38) * mm});
            skLineSegment(sketch, "E1157.MirrorCS", {"start": v(-790, 1287.5) * mm, "end": v(-720, 1327.9) * mm});
            skLineSegment(sketch, "E1158.MirrorCS", {"start": v(-410, 1426.06) * mm, "end": v(-410, 1345.23) * mm});
            skLineSegment(sketch, "E1159.MirrorCS", {"start": v(1040, 1882.16) * mm, "end": v(1110, 1841.75) * mm});
            skLineSegment(sketch, "E1160.MirrorCS", {"start": v(800, 1743.6) * mm, "end": v(730, 1703.18) * mm});
            skLineSegment(sketch, "E1161.MirrorCS", {"start": v(-410, 1345.23) * mm, "end": v(-480, 1304.81) * mm});
            skLineSegment(sketch, "E1162.MirrorCS", {"start": v(490, 1841.75) * mm, "end": v(560, 1882.16) * mm});
            skLineSegment(sketch, "E1163.MirrorCS", {"start": v(630, 1206.66) * mm, "end": v(630, 1287.5) * mm});
            skLineSegment(sketch, "E1164.MirrorCS", {"start": v(-710, 1622.35) * mm, "end": v(-710, 1703.18) * mm});
            skLineSegment(sketch, "E1165.MirrorCS", {"start": v(570, 1703.18) * mm, "end": v(640, 1743.6) * mm});
            skLineSegment(sketch, "E1166.MirrorCS", {"start": v(-70, 1148.93) * mm, "end": v(0, 1189.34) * mm});
            skLineSegment(sketch, "E1167.MirrorCS", {"start": v(880, 1720.5) * mm, "end": v(810, 1760.92) * mm});
            skLineSegment(sketch, "E1168.MirrorCS", {"start": v(-170, 1564.62) * mm, "end": v(-240, 1605.03) * mm});
            skLineSegment(sketch, "E1169.MirrorCS", {"start": v(570, 1345.23) * mm, "end": v(640, 1304.81) * mm});
            skLineSegment(sketch, "E1170.MirrorCS", {"start": v(400, 1327.9) * mm, "end": v(330, 1287.5) * mm});
            skLineSegment(sketch, "E1171.MirrorCS", {"start": v(-170, 1483.8) * mm, "end": v(-170, 1564.62) * mm});
            skLineSegment(sketch, "E1172.MirrorCS", {"start": v(310, 1287.5) * mm, "end": v(240, 1327.9) * mm});
            skLineSegment(sketch, "E1173.MirrorCS", {"start": v(-160, 1743.6) * mm, "end": v(-230, 1703.18) * mm});
            skLineSegment(sketch, "E1174.MirrorCS", {"start": v(90, 1426.06) * mm, "end": v(160, 1466.47) * mm});
            skLineSegment(sketch, "E1175.MirrorCS", {"start": v(810, 1760.92) * mm, "end": v(810, 1841.75) * mm});
            skLineSegment(sketch, "E1176.MirrorCS", {"start": v(410, 1426.06) * mm, "end": v(480, 1466.47) * mm});
            skLineSegment(sketch, "E1177.MirrorCS", {"start": v(310, 1564.62) * mm, "end": v(240, 1605.03) * mm});
            skLineSegment(sketch, "E1178.MirrorCS", {"start": v(490, 1287.5) * mm, "end": v(490, 1206.66) * mm});
            skLineSegment(sketch, "E1179.MirrorCS", {"start": v(630, 1564.62) * mm, "end": v(630, 1483.8) * mm});
            skLineSegment(sketch, "E1180.MirrorCS", {"start": v(-720, 1443.38) * mm, "end": v(-790, 1483.8) * mm});
            skLineSegment(sketch, "E1181.MirrorCS", {"start": v(-390, 1703.18) * mm, "end": v(-320, 1743.6) * mm});
            skLineSegment(sketch, "E1182.MirrorCS", {"start": v(730, 1622.35) * mm, "end": v(800, 1581.94) * mm});
            skLineSegment(sketch, "E1183.MirrorCS", {"start": v(560, 1327.9) * mm, "end": v(490, 1287.5) * mm});
            skLineSegment(sketch, "E1184.MirrorCS", {"start": v(1050, 1345.23) * mm, "end": v(1050, 1426.06) * mm});
            skLineSegment(sketch, "E1185.MirrorCS", {"start": v(550, 1703.18) * mm, "end": v(480, 1743.6) * mm});
            skLineSegment(sketch, "E1186.MirrorCS", {"start": v(-550, 1703.18) * mm, "end": v(-550, 1622.35) * mm});
            skLineSegment(sketch, "E1187.MirrorCS", {"start": v(950, 1287.5) * mm, "end": v(950, 1206.66) * mm});
            skLineSegment(sketch, "E1188.MirrorCS", {"start": v(-230, 1622.35) * mm, "end": v(-160, 1581.94) * mm});
            skLineSegment(sketch, "E1189.MirrorCS", {"start": v(230, 1345.23) * mm, "end": v(160, 1304.81) * mm});
            skLineSegment(sketch, "E1190.MirrorCS", {"start": v(-560, 1327.9) * mm, "end": v(-490, 1287.5) * mm});
            skLineSegment(sketch, "E1191.MirrorCS", {"start": v(-160, 1189.34) * mm, "end": v(-230, 1148.93) * mm});
            skLineSegment(sketch, "E1192.MirrorCS", {"start": v(970, 1564.62) * mm, "end": v(970, 1483.8) * mm});
            skLineSegment(sketch, "E1193.MirrorCS", {"start": v(400, 1882.16) * mm, "end": v(330, 1841.75) * mm});
            skLineSegment(sketch, "E1194.MirrorCS", {"start": v(-90, 1622.35) * mm, "end": v(-160, 1581.94) * mm});
            skLineSegment(sketch, "E1195.MirrorCS", {"start": v(-790, 1483.8) * mm, "end": v(-790, 1564.62) * mm});
            skLineSegment(sketch, "E1196.MirrorCS", {"start": v(-480, 1743.6) * mm, "end": v(-550, 1703.18) * mm});
            skLineSegment(sketch, "E1197.MirrorCS", {"start": v(1190, 1426.06) * mm, "end": v(1120, 1466.47) * mm});
            skLineSegment(sketch, "E1198.MirrorCS", {"start": v(-240, 1605.03) * mm, "end": v(-310, 1564.62) * mm});
            skLineSegment(sketch, "E1199.MirrorCS", {"start": v(-170, 1760.92) * mm, "end": v(-240, 1720.5) * mm});
            skLineSegment(sketch, "E1200.MirrorCS", {"start": v(-230, 1426.06) * mm, "end": v(-160, 1466.47) * mm});
            skLineSegment(sketch, "E1201.MirrorCS", {"start": v(-390, 1148.93) * mm, "end": v(-320, 1189.34) * mm});
            skLineSegment(sketch, "E1202.MirrorCS", {"start": v(-730, 1703.18) * mm, "end": v(-790, 1737.82) * mm});
            skLineSegment(sketch, "E1203.MirrorCS", {"start": v(150, 1564.62) * mm, "end": v(150, 1483.8) * mm});
            skLineSegment(sketch, "E1204.MirrorCS", {"start": v(-560, 1882.16) * mm, "end": v(-630, 1841.75) * mm});
            skLineSegment(sketch, "E1205.MirrorCS", {"start": v(800, 1189.34) * mm, "end": v(730, 1148.93) * mm});
            skLineSegment(sketch, "E1206.MirrorCS", {"start": v(1130, 1287.5) * mm, "end": v(1130, 1206.66) * mm});
            skLineSegment(sketch, "E1207.MirrorCS", {"start": v(1130, 1564.62) * mm, "end": v(1190, 1599.26) * mm});
            skLineSegment(sketch, "E1208.MirrorCS", {"start": v(0, 1304.81) * mm, "end": v(70, 1345.23) * mm});
            skLineSegment(sketch, "E1209.MirrorCS", {"start": v(-240, 1166.25) * mm, "end": v(-310, 1206.66) * mm});
            skLineSegment(sketch, "E1210.MirrorCS", {"start": v(950, 1206.66) * mm, "end": v(880, 1166.25) * mm});
            skLineSegment(sketch, "E1211.MirrorCS", {"start": v(80, 1882.16) * mm, "end": v(10, 1841.75) * mm});
            skLineSegment(sketch, "E1212.MirrorCS", {"start": v(870, 1426.06) * mm, "end": v(870, 1345.23) * mm});
            skLineSegment(sketch, "E1213.MirrorCS", {"start": v(-790, 1206.66) * mm, "end": v(-720, 1166.25) * mm});
            skLineSegment(sketch, "E1214.MirrorCS", {"start": v(-630, 1206.66) * mm, "end": v(-560, 1166.25) * mm});
            skLineSegment(sketch, "E1215.MirrorCS", {"start": v(390, 1345.23) * mm, "end": v(390, 1426.06) * mm});
            skLineSegment(sketch, "E1216.MirrorCS", {"start": v(640, 1743.6) * mm, "end": v(710, 1703.18) * mm});
            skLineSegment(sketch, "E1217.MirrorCS", {"start": v(-720, 1720.5) * mm, "end": v(-650, 1760.92) * mm});
            skLineSegment(sketch, "E1218.MirrorCS", {"start": v(-560, 1720.5) * mm, "end": v(-490, 1760.92) * mm});
            skLineSegment(sketch, "E1219.MirrorCS", {"start": v(650, 1841.75) * mm, "end": v(650, 1760.92) * mm});
            skLineSegment(sketch, "E1220.MirrorCS", {"start": v(80, 1166.25) * mm, "end": v(150, 1206.66) * mm});
            skLineSegment(sketch, "E1221.MirrorCS", {"start": v(-90, 1345.23) * mm, "end": v(-160, 1304.81) * mm});
            skLineSegment(sketch, "E1222.MirrorCS", {"start": v(1190, 1345.23) * mm, "end": v(1120, 1304.81) * mm});
            skLineSegment(sketch, "E1223.MirrorCS", {"start": v(250, 1426.06) * mm, "end": v(320, 1466.47) * mm});
            skLineSegment(sketch, "E1224.MirrorCS", {"start": v(-640, 1581.94) * mm, "end": v(-710, 1622.35) * mm});
            skLineSegment(sketch, "E1225.MirrorCS", {"start": v(240, 1605.03) * mm, "end": v(170, 1564.62) * mm});
            skLineSegment(sketch, "E1226.MirrorCS", {"start": v(-150, 1564.62) * mm, "end": v(-80, 1605.03) * mm});
            skLineSegment(sketch, "E1227.MirrorCS", {"start": v(-320, 1743.6) * mm, "end": v(-250, 1703.18) * mm});
            skLineSegment(sketch, "E1228.MirrorCS", {"start": v(870, 1345.23) * mm, "end": v(800, 1304.81) * mm});
            skLineSegment(sketch, "E1229.MirrorCS", {"start": v(-640, 1304.81) * mm, "end": v(-570, 1345.23) * mm});
            skLineSegment(sketch, "E1230.MirrorCS", {"start": v(730, 1703.18) * mm, "end": v(730, 1622.35) * mm});
            skLineSegment(sketch, "E1231.MirrorCS", {"start": v(-310, 1564.62) * mm, "end": v(-310, 1483.8) * mm});
            skLineSegment(sketch, "E1232.MirrorCS", {"start": v(730, 1345.23) * mm, "end": v(730, 1426.06) * mm});
            skLineSegment(sketch, "E1233.MirrorCS", {"start": v(480, 1743.6) * mm, "end": v(410, 1703.18) * mm});
            skLineSegment(sketch, "E1234.MirrorCS", {"start": v(390, 1703.18) * mm, "end": v(390, 1622.35) * mm});
            skLineSegment(sketch, "E1235.MirrorCS", {"start": v(470, 1483.8) * mm, "end": v(470, 1564.62) * mm});
            skLineSegment(sketch, "E1236.MirrorCS", {"start": v(550, 1148.93) * mm, "end": v(480, 1189.34) * mm});
            skLineSegment(sketch, "E1237.MirrorCS", {"start": v(90, 1703.18) * mm, "end": v(90, 1622.35) * mm});
            skLineSegment(sketch, "E1238.MirrorCS", {"start": v(10, 1841.75) * mm, "end": v(10, 1760.92) * mm});
            skLineSegment(sketch, "E1239.MirrorCS", {"start": v(-10, 1564.62) * mm, "end": v(-10, 1483.8) * mm});
            skLineSegment(sketch, "E1240.MirrorCS", {"start": v(310, 1483.8) * mm, "end": v(310, 1564.62) * mm});
            skLineSegment(sketch, "E1241.MirrorCS", {"start": v(970, 1287.5) * mm, "end": v(1040, 1327.9) * mm});
            skLineSegment(sketch, "E1242.MirrorCS", {"start": v(-90, 1148.93) * mm, "end": v(-160, 1189.34) * mm});
            skLineSegment(sketch, "E1243.MirrorCS", {"start": v(320, 1743.6) * mm, "end": v(390, 1703.18) * mm});
            skLineSegment(sketch, "E1244.MirrorCS", {"start": v(-650, 1564.62) * mm, "end": v(-650, 1483.8) * mm});
            skLineSegment(sketch, "E1245.MirrorCS", {"start": v(150, 1760.92) * mm, "end": v(150, 1841.75) * mm});
            skLineSegment(sketch, "E1246.MirrorCS", {"start": v(-80, 1605.03) * mm, "end": v(-10, 1564.62) * mm});
            skLineSegment(sketch, "E1247.MirrorCS", {"start": v(-560, 1327.9) * mm, "end": v(-630, 1287.5) * mm});
            skLineSegment(sketch, "E1248.MirrorCS", {"start": v(1190, 1426.06) * mm, "end": v(1190, 1345.23) * mm});
            skLineSegment(sketch, "E1249.MirrorCS", {"start": v(1120, 1189.34) * mm, "end": v(1050, 1148.93) * mm});
            skLineSegment(sketch, "E1250.MirrorCS", {"start": v(230, 1148.93) * mm, "end": v(160, 1189.34) * mm});
            skLineSegment(sketch, "E1251.MirrorCS", {"start": v(-70, 1703.18) * mm, "end": v(0, 1743.6) * mm});
            skLineSegment(sketch, "E1252.MirrorCS", {"start": v(250, 1622.35) * mm, "end": v(320, 1581.94) * mm});
            skLineSegment(sketch, "E1253.MirrorCS", {"start": v(410, 1345.23) * mm, "end": v(410, 1426.06) * mm});
            skLineSegment(sketch, "E1254.MirrorCS", {"start": v(-790, 1587.71) * mm, "end": v(-730, 1622.35) * mm});
            skLineSegment(sketch, "E1255.MirrorCS", {"start": v(810, 1206.66) * mm, "end": v(810, 1287.5) * mm});
            skLineSegment(sketch, "E1256.MirrorCS", {"start": v(-790, 1841.75) * mm, "end": v(-790, 1760.92) * mm});
            skLineSegment(sketch, "E1257.MirrorCS", {"start": v(-470, 1483.8) * mm, "end": v(-400, 1443.38) * mm});
            skLineSegment(sketch, "E1258.MirrorCS", {"start": v(650, 1287.5) * mm, "end": v(650, 1206.66) * mm});
            skLineSegment(sketch, "E1259.MirrorCS", {"start": v(320, 1189.34) * mm, "end": v(390, 1148.93) * mm});
            skLineSegment(sketch, "E1260.MirrorCS", {"start": v(-400, 1327.9) * mm, "end": v(-470, 1287.5) * mm});
            skLineSegment(sketch, "E1261.MirrorCS", {"start": v(410, 1622.35) * mm, "end": v(480, 1581.94) * mm});
            skLineSegment(sketch, "E1262.MirrorCS", {"start": v(-80, 1882.16) * mm, "end": v(-150, 1841.75) * mm});
            skLineSegment(sketch, "E1263.MirrorCS", {"start": v(-80, 1443.38) * mm, "end": v(-10, 1483.8) * mm});
            skLineSegment(sketch, "E1264.MirrorCS", {"start": v(-330, 1483.8) * mm, "end": v(-330, 1564.62) * mm});
            skLineSegment(sketch, "E1265.MirrorCS", {"start": v(160, 1189.34) * mm, "end": v(90, 1148.93) * mm});
            skLineSegment(sketch, "E1266.MirrorCS", {"start": v(1110, 1760.92) * mm, "end": v(1040, 1720.5) * mm});
            skLineSegment(sketch, "E1267.MirrorCS", {"start": v(-90, 1426.06) * mm, "end": v(-160, 1466.47) * mm});
            skLineSegment(sketch, "E1268.MirrorCS", {"start": v(150, 1206.66) * mm, "end": v(150, 1287.5) * mm});
            skLineSegment(sketch, "E1269.MirrorCS", {"start": v(-720, 1605.03) * mm, "end": v(-650, 1564.62) * mm});
            skLineSegment(sketch, "E1270.MirrorCS", {"start": v(-10, 1206.66) * mm, "end": v(-10, 1287.5) * mm});
            skLineSegment(sketch, "E1271.MirrorCS", {"start": v(-390, 1622.35) * mm, "end": v(-390, 1703.18) * mm});
            skLineSegment(sketch, "E1272.MirrorCS", {"start": v(310, 1760.92) * mm, "end": v(240, 1720.5) * mm});
            skLineSegment(sketch, "E1273.MirrorCS", {"start": v(790, 1206.66) * mm, "end": v(790, 1287.5) * mm});
            skLineSegment(sketch, "E1274.MirrorCS", {"start": v(10, 1564.62) * mm, "end": v(80, 1605.03) * mm});
            skLineSegment(sketch, "E1275.MirrorCS", {"start": v(-650, 1206.66) * mm, "end": v(-650, 1287.5) * mm});
            skLineSegment(sketch, "E1276.MirrorCS", {"start": v(950, 1841.75) * mm, "end": v(950, 1760.92) * mm});
            skLineSegment(sketch, "E1277.MirrorCS", {"start": v(-480, 1304.81) * mm, "end": v(-550, 1345.23) * mm});
            skLineSegment(sketch, "E1278.MirrorCS", {"start": v(250, 1426.06) * mm, "end": v(250, 1345.23) * mm});
            skLineSegment(sketch, "E1279.MirrorCS", {"start": v(550, 1622.35) * mm, "end": v(550, 1703.18) * mm});
            skLineSegment(sketch, "E1280.MirrorCS", {"start": v(-80, 1327.9) * mm, "end": v(-150, 1287.5) * mm});
            skLineSegment(sketch, "E1281.MirrorCS", {"start": v(1030, 1703.18) * mm, "end": v(1030, 1622.35) * mm});
            skLineSegment(sketch, "E1282.MirrorCS", {"start": v(1110, 1483.8) * mm, "end": v(1040, 1443.38) * mm});
            skLineSegment(sketch, "E1283.MirrorCS", {"start": v(1040, 1166.25) * mm, "end": v(970, 1206.66) * mm});
            skLineSegment(sketch, "E1284.MirrorCS", {"start": v(310, 1483.8) * mm, "end": v(240, 1443.38) * mm});
            skLineSegment(sketch, "E1285.MirrorCS", {"start": v(480, 1189.34) * mm, "end": v(410, 1148.93) * mm});
            skLineSegment(sketch, "E1286.MirrorCS", {"start": v(-710, 1426.06) * mm, "end": v(-640, 1466.47) * mm});
            skLineSegment(sketch, "E1287.MirrorCS", {"start": v(-410, 1622.35) * mm, "end": v(-410, 1703.18) * mm});
            skLineSegment(sketch, "E1288.MirrorCS", {"start": v(400, 1720.5) * mm, "end": v(330, 1760.92) * mm});
            skLineSegment(sketch, "E1289.MirrorCS", {"start": v(640, 1581.94) * mm, "end": v(570, 1622.35) * mm});
            skLineSegment(sketch, "E1290.MirrorCS", {"start": v(390, 1426.06) * mm, "end": v(320, 1466.47) * mm});
            skLineSegment(sketch, "E1291.MirrorCS", {"start": v(1110, 1287.5) * mm, "end": v(1110, 1206.66) * mm});
            skLineSegment(sketch, "E1292.MirrorCS", {"start": v(-640, 1189.34) * mm, "end": v(-570, 1148.93) * mm});
            skLineSegment(sketch, "E1293.MirrorCS", {"start": v(-490, 1206.66) * mm, "end": v(-490, 1287.5) * mm});
            skLineSegment(sketch, "E1294.MirrorCS", {"start": v(880, 1882.16) * mm, "end": v(950, 1841.75) * mm});
            skLineSegment(sketch, "E1295.MirrorCS", {"start": v(-490, 1841.75) * mm, "end": v(-560, 1882.16) * mm});
            skLineSegment(sketch, "E1296.MirrorCS", {"start": v(-790, 1760.92) * mm, "end": v(-720, 1720.5) * mm});
            skLineSegment(sketch, "E1297.MirrorCS", {"start": v(950, 1564.62) * mm, "end": v(880, 1605.03) * mm});
            skLineSegment(sketch, "E1298.MirrorCS", {"start": v(-310, 1483.8) * mm, "end": v(-240, 1443.38) * mm});
            skLineSegment(sketch, "E1299.MirrorCS", {"start": v(-470, 1206.66) * mm, "end": v(-470, 1287.5) * mm});
            skLineSegment(sketch, "E1300.MirrorCS", {"start": v(250, 1703.18) * mm, "end": v(320, 1743.6) * mm});
            skLineSegment(sketch, "E1301.MirrorCS", {"start": v(-250, 1622.35) * mm, "end": v(-320, 1581.94) * mm});
            skLineSegment(sketch, "E1302.MirrorCS", {"start": v(630, 1841.75) * mm, "end": v(560, 1882.16) * mm});
            skLineSegment(sketch, "E1303.MirrorCS", {"start": v(-70, 1622.35) * mm, "end": v(-70, 1703.18) * mm});
            skLineSegment(sketch, "E1304.MirrorCS", {"start": v(-400, 1605.03) * mm, "end": v(-470, 1564.62) * mm});
            skLineSegment(sketch, "E1305.MirrorCS", {"start": v(-330, 1760.92) * mm, "end": v(-400, 1720.5) * mm});
            skLineSegment(sketch, "E1306.MirrorCS", {"start": v(-480, 1581.94) * mm, "end": v(-550, 1622.35) * mm});
            skLineSegment(sketch, "E1307.MirrorCS", {"start": v(10, 1760.92) * mm, "end": v(80, 1720.5) * mm});
            skLineSegment(sketch, "E1308.MirrorCS", {"start": v(1030, 1426.06) * mm, "end": v(960, 1466.47) * mm});
            skLineSegment(sketch, "E1309.MirrorCS", {"start": v(960, 1466.47) * mm, "end": v(890, 1426.06) * mm});
            skLineSegment(sketch, "E1310.MirrorCS", {"start": v(-320, 1189.34) * mm, "end": v(-250, 1148.93) * mm});
            skLineSegment(sketch, "E1311.MirrorCS", {"start": v(80, 1327.9) * mm, "end": v(150, 1287.5) * mm});
            skLineSegment(sketch, "E1312.MirrorCS", {"start": v(230, 1622.35) * mm, "end": v(160, 1581.94) * mm});
            skLineSegment(sketch, "E1313.MirrorCS", {"start": v(-650, 1760.92) * mm, "end": v(-650, 1841.75) * mm});
            skLineSegment(sketch, "E1314.MirrorCS", {"start": v(-630, 1483.8) * mm, "end": v(-630, 1564.62) * mm});
            skLineSegment(sketch, "E1315.MirrorCS", {"start": v(970, 1483.8) * mm, "end": v(1040, 1443.38) * mm});
            skLineSegment(sketch, "E1316.MirrorCS", {"start": v(800, 1581.94) * mm, "end": v(870, 1622.35) * mm});
            skLineSegment(sketch, "E1317.MirrorCS", {"start": v(0, 1189.34) * mm, "end": v(70, 1148.93) * mm});
            skLineSegment(sketch, "E1318.MirrorCS", {"start": v(550, 1426.06) * mm, "end": v(550, 1345.23) * mm});
            skLineSegment(sketch, "E1319.MirrorCS", {"start": v(800, 1466.47) * mm, "end": v(870, 1426.06) * mm});
            skLineSegment(sketch, "E1320.MirrorCS", {"start": v(1190, 1703.18) * mm, "end": v(1120, 1743.6) * mm});
            skLineSegment(sketch, "E1321.MirrorCS", {"start": v(70, 1426.06) * mm, "end": v(0, 1466.47) * mm});
            skLineSegment(sketch, "E1322.MirrorCS", {"start": v(-400, 1443.38) * mm, "end": v(-330, 1483.8) * mm});
            skLineSegment(sketch, "E1323.MirrorCS", {"start": v(-170, 1206.66) * mm, "end": v(-240, 1166.25) * mm});
            skLineSegment(sketch, "E1324.MirrorCS", {"start": v(800, 1304.81) * mm, "end": v(730, 1345.23) * mm});
            skLineSegment(sketch, "E1325.MirrorCS", {"start": v(-640, 1743.6) * mm, "end": v(-570, 1703.18) * mm});
            skLineSegment(sketch, "E1326.MirrorCS", {"start": v(-730, 1426.06) * mm, "end": v(-730, 1345.23) * mm});
            skLineSegment(sketch, "E1327.MirrorCS", {"start": v(-310, 1841.75) * mm, "end": v(-240, 1882.16) * mm});
            skLineSegment(sketch, "E1328.MirrorCS", {"start": v(0, 1466.47) * mm, "end": v(-70, 1426.06) * mm});
            skLineSegment(sketch, "E1329.MirrorCS", {"start": v(550, 1622.35) * mm, "end": v(480, 1581.94) * mm});
            skLineSegment(sketch, "E1330.MirrorCS", {"start": v(-310, 1760.92) * mm, "end": v(-310, 1841.75) * mm});
            skLineSegment(sketch, "E1331.MirrorCS", {"start": v(720, 1720.5) * mm, "end": v(790, 1760.92) * mm});
            skLineSegment(sketch, "E1332.MirrorCS", {"start": v(-150, 1760.92) * mm, "end": v(-80, 1720.5) * mm});
            skLineSegment(sketch, "E1333.MirrorCS", {"start": v(630, 1483.8) * mm, "end": v(560, 1443.38) * mm});
            skLineSegment(sketch, "E1334.MirrorCS", {"start": v(970, 1841.75) * mm, "end": v(1040, 1882.16) * mm});
            skLineSegment(sketch, "E1335.MirrorCS", {"start": v(250, 1345.23) * mm, "end": v(320, 1304.81) * mm});
            skLineSegment(sketch, "E1336.MirrorCS", {"start": v(720, 1443.38) * mm, "end": v(650, 1483.8) * mm});
            skLineSegment(sketch, "E1337.MirrorCS", {"start": v(470, 1287.5) * mm, "end": v(400, 1327.9) * mm});
            skLineSegment(sketch, "E1338.MirrorCS", {"start": v(810, 1564.62) * mm, "end": v(810, 1483.8) * mm});
            skLineSegment(sketch, "E1339.MirrorCS", {"start": v(-400, 1882.16) * mm, "end": v(-330, 1841.75) * mm});
            skLineSegment(sketch, "E1340.MirrorCS", {"start": v(-720, 1166.25) * mm, "end": v(-650, 1206.66) * mm});
            skLineSegment(sketch, "E1341.MirrorCS", {"start": v(80, 1443.38) * mm, "end": v(10, 1483.8) * mm});
            skLineSegment(sketch, "E1342.MirrorCS", {"start": v(-170, 1841.75) * mm, "end": v(-240, 1882.16) * mm});
            skLineSegment(sketch, "E1343.MirrorCS", {"start": v(310, 1841.75) * mm, "end": v(310, 1760.92) * mm});
            skLineSegment(sketch, "E1344.MirrorCS", {"start": v(-150, 1841.75) * mm, "end": v(-150, 1760.92) * mm});
            skLineSegment(sketch, "E1345.MirrorCS", {"start": v(650, 1483.8) * mm, "end": v(650, 1564.62) * mm});
            skLineSegment(sketch, "E1346.MirrorCS", {"start": v(720, 1882.16) * mm, "end": v(790, 1841.75) * mm});
            skLineSegment(sketch, "E1347.MirrorCS", {"start": v(-240, 1327.9) * mm, "end": v(-170, 1287.5) * mm});
            skLineSegment(sketch, "E1348.MirrorCS", {"start": v(-330, 1206.66) * mm, "end": v(-400, 1166.25) * mm});
            skLineSegment(sketch, "E1349.MirrorCS", {"start": v(330, 1206.66) * mm, "end": v(330, 1287.5) * mm});
            skLineSegment(sketch, "E1350.MirrorCS", {"start": v(-320, 1304.81) * mm, "end": v(-250, 1345.23) * mm});
            skLineSegment(sketch, "E1351.MirrorCS", {"start": v(-90, 1426.06) * mm, "end": v(-90, 1345.23) * mm});
            skLineSegment(sketch, "E1352.MirrorCS", {"start": v(-720, 1882.16) * mm, "end": v(-790, 1841.75) * mm});
            skLineSegment(sketch, "E1353.MirrorCS", {"start": v(-240, 1720.5) * mm, "end": v(-310, 1760.92) * mm});
            skLineSegment(sketch, "E1354.MirrorCS", {"start": v(-90, 1622.35) * mm, "end": v(-90, 1703.18) * mm});
            skLineSegment(sketch, "E1355.MirrorCS", {"start": v(1190, 1148.93) * mm, "end": v(1120, 1189.34) * mm});
            skLineSegment(sketch, "E1356.MirrorCS", {"start": v(-230, 1703.18) * mm, "end": v(-230, 1622.35) * mm});
            skLineSegment(sketch, "E1357.MirrorCS", {"start": v(-170, 1287.5) * mm, "end": v(-170, 1206.66) * mm});
            skLineSegment(sketch, "E1358.MirrorCS", {"start": v(-730, 1622.35) * mm, "end": v(-730, 1703.18) * mm});
            skLineSegment(sketch, "E1359.MirrorCS", {"start": v(890, 1703.18) * mm, "end": v(960, 1743.6) * mm});
            skLineSegment(sketch, "E1360.MirrorCS", {"start": v(490, 1483.8) * mm, "end": v(490, 1564.62) * mm});
            skLineSegment(sketch, "E1361.MirrorCS", {"start": v(560, 1605.03) * mm, "end": v(630, 1564.62) * mm});
            skLineSegment(sketch, "E1362.MirrorCS", {"start": v(720, 1166.25) * mm, "end": v(790, 1206.66) * mm});
            skLineSegment(sketch, "E1363.MirrorCS", {"start": v(-710, 1426.06) * mm, "end": v(-710, 1345.23) * mm});
            skLineSegment(sketch, "E1364.MirrorCS", {"start": v(330, 1564.62) * mm, "end": v(330, 1483.8) * mm});
            skLineSegment(sketch, "E1365.MirrorCS", {"start": v(790, 1564.62) * mm, "end": v(790, 1483.8) * mm});
            skLineSegment(sketch, "E1366.MirrorCS", {"start": v(640, 1304.81) * mm, "end": v(710, 1345.23) * mm});
            skLineSegment(sketch, "E1367.MirrorCS", {"start": v(-710, 1148.93) * mm, "end": v(-640, 1189.34) * mm});
            skLineSegment(sketch, "E1368", {"start": v(1210, -100.83) * mm, "end": v(-810, -100.83) * mm});
            skLineSegment(sketch, "E1369", {"start": v(-810, -100.83) * mm, "end": v(-810, 1902.16) * mm});
            skLineSegment(sketch, "E1370", {"start": v(1210, 1902.16) * mm, "end": v(1210, -100.83) * mm});
            skPoint(sketch, "E1371.orphan", {"position": v(-810, 138.56) * mm});
            skLineSegment(sketch, "E1372.1", {"start": v(1190, 1703.18) * mm, "end": v(1190, 1622.35) * mm});
            skLineSegment(sketch, "E1372.3", {"start": v(-790, 98.15) * mm, "end": v(-790, 178.98) * mm});
            skLineSegment(sketch, "E1373", {"start": v(-810, 1902.16) * mm, "end": v(1210, 1902.16) * mm});
            skLineSegment(sketch, "E1374.trimOffspring", {"start": v(-790, 1760.92) * mm, "end": v(-790, 1841.75) * mm});
            skLineSegment(sketch, "E1375.trimOffspring", {"start": v(-790, 1587.71) * mm, "end": v(-790, 1737.82) * mm});
            skLineSegment(sketch, "E1376.trimOffspring", {"start": v(-790, 1310.59) * mm, "end": v(-790, 1460.7) * mm});
            skLineSegment(sketch, "E1377.trimOffspring", {"start": v(-790, 1206.66) * mm, "end": v(-790, 1287.5) * mm});
            skLineSegment(sketch, "E1378.trimOffspring", {"start": v(-790, 1033.46) * mm, "end": v(-790, 1183.57) * mm});
            skLineSegment(sketch, "E1379.trimOffspring", {"start": v(-790, 756.33) * mm, "end": v(-790, 906.44) * mm});
            skLineSegment(sketch, "E1380.trimOffspring", {"start": v(-790, 652.4) * mm, "end": v(-790, 733.23) * mm});
            skLineSegment(sketch, "E1381.trimOffspring", {"start": v(-790, 479.2) * mm, "end": v(-790, 629.31) * mm});
            skLineSegment(sketch, "E1382.trimOffspring", {"start": v(-790, 202.07) * mm, "end": v(-790, 352.18) * mm});
            skLineSegment(sketch, "E1383.trimOffspring", {"start": v(1190, 40.41) * mm, "end": v(1190, -40.41) * mm});
            skLineSegment(sketch, "E1384.trimOffspring", {"start": v(1190, 213.62) * mm, "end": v(1190, 63.5) * mm});
            skLineSegment(sketch, "E1385.trimOffspring", {"start": v(1190, 490.75) * mm, "end": v(1190, 340.64) * mm});
            skLineSegment(sketch, "E1386.trimOffspring", {"start": v(1190, 767.88) * mm, "end": v(1190, 617.76) * mm});
            skLineSegment(sketch, "E1387.trimOffspring", {"start": v(1190, 871.8) * mm, "end": v(1190, 790.97) * mm});
            skLineSegment(sketch, "E1388.trimOffspring", {"start": v(1190, 1045) * mm, "end": v(1190, 894.9) * mm});
            skLineSegment(sketch, "E1389.trimOffspring", {"start": v(1190, 1322.13) * mm, "end": v(1190, 1172.02) * mm});
            skLineSegment(sketch, "E1390.trimOffspring", {"start": v(1190, 1599.26) * mm, "end": v(1190, 1449.15) * mm});
            skPoint(sketch, "E1391", {"position": v(-810, 1749.17) * mm});
            skPoint(sketch, "E1392", {"position": v(-810, 1149.17) * mm});
            skPoint(sketch, "E1393", {"position": v(-810, 549.17) * mm});
            skSolve(sketch);
        }
        {
            var Q0;
            Q0=makeQuery(id+"F0.imprint","IMPRINT",FACE,{"disambiguationData":[TD([[makeQuery(id+"F0.imprint","IMPRINT",EDGE,{"derivedFrom":sQuery(id+"F0.wireOp",EDGE,"E0")}),1.0]])]});
            extrude(context, id + "F1", {"entities" : qUnion([Q0]), "depth" : 20 * mm, "offsetDistance" : 25 * mm});
        }
        {
            var Q0;
            Q0=sQuery(id+"F0.wireOp",VERTEX,"E1393");
            var Q1;
            Q1=sQuery(id+"F0.wireOp",VERTEX,"E1392");
            var Q2;
            Q2=sQuery(id+"F0.wireOp",VERTEX,"E1391");
            var Q3;
            Q3=makeQuery(id+"F1.opExtrude","SWEPT_BODY",BODY,{"disambiguationData":[OSD([sQuery(id+"F0.wireOp",EDGE,"E0"),sQuery(id+"F0.wireOp",EDGE,"E1"),sQuery(id+"F0.wireOp",EDGE,"E2"),sQuery(id+"F0.wireOp",EDGE,"E3"),sQuery(id+"F0.wireOp",EDGE,"E4"),sQuery(id+"F0.wireOp",EDGE,"E5"),sQuery(id+"F0.wireOp",EDGE,"E6.MirrorCS"),sQuery(id+"F0.wireOp",EDGE,"E7.MirrorCS"),sQuery(id+"F0.wireOp",EDGE,"E10.MirrorCS"),sQuery(id+"F0.wireOp",EDGE,"E11.MirrorCS"),sQuery(id+"F0.wireOp",EDGE,"E12.MirrorCS"),sQuery(id+"F0.wireOp",EDGE,"E13.MirrorCS"),sQuery(id+"F0.wireOp",EDGE,"E14.MirrorCS"),sQuery(id+"F0.wireOp",EDGE,"E15.MirrorCS"),sQuery(id+"F0.wireOp",EDGE,"E16.MirrorCS"),sQuery(id+"F0.wireOp",EDGE,"E17.MirrorCS"),sQuery(id+"F0.wireOp",EDGE,"E18.MirrorCS"),sQuery(id+"F0.wireOp",EDGE,"E19.MirrorCS"),sQuery(id+"F0.wireOp",EDGE,"E20.MirrorCS"),sQuery(id+"F0.wireOp",EDGE,"E21.MirrorCS"),sQuery(id+"F0.wireOp",EDGE,"E22.MirrorCS"),sQuery(id+"F0.wireOp",EDGE,"E23.MirrorCS"),sQuery(id+"F0.wireOp",EDGE,"E24.MirrorCS"),sQuery(id+"F0.wireOp",EDGE,"E25.MirrorCS"),sQuery(id+"F0.wireOp",EDGE,"E27.MirrorCS"),sQuery(id+"F0.wireOp",EDGE,"E28.MirrorCS"),sQuery(id+"F0.wireOp",EDGE,"E29.MirrorCS"),sQuery(id+"F0.wireOp",EDGE,"E30.MirrorCS"),sQuery(id+"F0.wireOp",EDGE,"E31.MirrorCS"),sQuery(id+"F0.wireOp",EDGE,"E32.MirrorCS"),sQuery(id+"F0.wireOp",EDGE,"E33.MirrorCS"),sQuery(id+"F0.wireOp",EDGE,"E34.MirrorCS"),sQuery(id+"F0.wireOp",EDGE,"E36.MirrorCS"),sQuery(id+"F0.wireOp",EDGE,"E37.MirrorCS"),sQuery(id+"F0.wireOp",EDGE,"E38.MirrorCS"),sQuery(id+"F0.wireOp",EDGE,"E39.MirrorCS"),sQuery(id+"F0.wireOp",EDGE,"E41.MirrorCS"),sQuery(id+"F0.wireOp",EDGE,"E42.MirrorCS"),sQuery(id+"F0.wireOp",EDGE,"E43.MirrorCS"),sQuery(id+"F0.wireOp",EDGE,"E45.MirrorCS"),sQuery(id+"F0.wireOp",EDGE,"E46.MirrorCS"),sQuery(id+"F0.wireOp",EDGE,"E47.MirrorCS"),sQuery(id+"F0.wireOp",EDGE,"E49.MirrorCS"),sQuery(id+"F0.wireOp",EDGE,"E50.MirrorCS"),sQuery(id+"F0.wireOp",EDGE,"E51.MirrorCS"),sQuery(id+"F0.wireOp",EDGE,"E52.MirrorCS"),sQuery(id+"F0.wireOp",EDGE,"E53.MirrorCS"),sQuery(id+"F0.wireOp",EDGE,"E54.MirrorCS"),sQuery(id+"F0.wireOp",EDGE,"E55.MirrorCS"),sQuery(id+"F0.wireOp",EDGE,"E56.MirrorCS"),sQuery(id+"F0.wireOp",EDGE,"E57.MirrorCS"),sQuery(id+"F0.wireOp",EDGE,"E58.MirrorCS"),sQuery(id+"F0.wireOp",EDGE,"E59.MirrorCS"),sQuery(id+"F0.wireOp",EDGE,"E61.MirrorCS"),sQuery(id+"F0.wireOp",EDGE,"E62.MirrorCS"),sQuery(id+"F0.wireOp",EDGE,"E63.MirrorCS"),sQuery(id+"F0.wireOp",EDGE,"E64.MirrorCS"),sQuery(id+"F0.wireOp",EDGE,"E65.MirrorCS"),sQuery(id+"F0.wireOp",EDGE,"E66.MirrorCS"),sQuery(id+"F0.wireOp",EDGE,"E67.MirrorCS"),sQuery(id+"F0.wireOp",EDGE,"E68.MirrorCS"),sQuery(id+"F0.wireOp",EDGE,"E69.MirrorCS"),sQuery(id+"F0.wireOp",EDGE,"E71.MirrorCS"),sQuery(id+"F0.wireOp",EDGE,"E72.MirrorCS"),sQuery(id+"F0.wireOp",EDGE,"E73.MirrorCS"),sQuery(id+"F0.wireOp",EDGE,"E74.MirrorCS"),sQuery(id+"F0.wireOp",EDGE,"E75.MirrorCS"),sQuery(id+"F0.wireOp",EDGE,"E76.MirrorCS"),sQuery(id+"F0.wireOp",EDGE,"E77.MirrorCS"),sQuery(id+"F0.wireOp",EDGE,"E78.MirrorCS"),sQuery(id+"F0.wireOp",EDGE,"E80.MirrorCS"),sQuery(id+"F0.wireOp",EDGE,"E81.MirrorCS"),sQuery(id+"F0.wireOp",EDGE,"E82.MirrorCS"),sQuery(id+"F0.wireOp",EDGE,"E83.MirrorCS"),sQuery(id+"F0.wireOp",EDGE,"E84.MirrorCS"),sQuery(id+"F0.wireOp",EDGE,"E85.MirrorCS"),sQuery(id+"F0.wireOp",EDGE,"E86.MirrorCS"),sQuery(id+"F0.wireOp",EDGE,"E87.MirrorCS"),sQuery(id+"F0.wireOp",EDGE,"E88.MirrorCS"),sQuery(id+"F0.wireOp",EDGE,"E89.MirrorCS"),sQuery(id+"F0.wireOp",EDGE,"E91.MirrorCS"),sQuery(id+"F0.wireOp",EDGE,"E92.MirrorCS"),sQuery(id+"F0.wireOp",EDGE,"E93.MirrorCS"),sQuery(id+"F0.wireOp",EDGE,"E95.MirrorCS"),sQuery(id+"F0.wireOp",EDGE,"E97.MirrorCS"),sQuery(id+"F0.wireOp",EDGE,"E98.MirrorCS"),sQuery(id+"F0.wireOp",EDGE,"E99.MirrorCS"),sQuery(id+"F0.wireOp",EDGE,"E100.MirrorCS"),sQuery(id+"F0.wireOp",EDGE,"E101.MirrorCS"),sQuery(id+"F0.wireOp",EDGE,"E102.MirrorCS"),sQuery(id+"F0.wireOp",EDGE,"E103.MirrorCS"),sQuery(id+"F0.wireOp",EDGE,"E104.MirrorCS"),sQuery(id+"F0.wireOp",EDGE,"E106.MirrorCS"),sQuery(id+"F0.wireOp",EDGE,"E107.MirrorCS"),sQuery(id+"F0.wireOp",EDGE,"E108.MirrorCS"),sQuery(id+"F0.wireOp",EDGE,"E109.MirrorCS"),sQuery(id+"F0.wireOp",EDGE,"E111.MirrorCS"),sQuery(id+"F0.wireOp",EDGE,"E113.MirrorCS"),sQuery(id+"F0.wireOp",EDGE,"E114.MirrorCS"),sQuery(id+"F0.wireOp",EDGE,"E116.MirrorCS"),sQuery(id+"F0.wireOp",EDGE,"E117.MirrorCS"),sQuery(id+"F0.wireOp",EDGE,"E119.MirrorCS"),sQuery(id+"F0.wireOp",EDGE,"E120.MirrorCS"),sQuery(id+"F0.wireOp",EDGE,"E121.MirrorCS"),sQuery(id+"F0.wireOp",EDGE,"E122.MirrorCS"),sQuery(id+"F0.wireOp",EDGE,"E123.MirrorCS"),sQuery(id+"F0.wireOp",EDGE,"E129.MirrorCS"),sQuery(id+"F0.wireOp",EDGE,"E130.MirrorCS"),sQuery(id+"F0.wireOp",EDGE,"E131.MirrorCS"),sQuery(id+"F0.wireOp",EDGE,"E132.MirrorCS"),sQuery(id+"F0.wireOp",EDGE,"E133.MirrorCS"),sQuery(id+"F0.wireOp",EDGE,"E135.MirrorCS"),sQuery(id+"F0.wireOp",EDGE,"E137.MirrorCS"),sQuery(id+"F0.wireOp",EDGE,"E138.MirrorCS"),sQuery(id+"F0.wireOp",EDGE,"E139.MirrorCS"),sQuery(id+"F0.wireOp",EDGE,"E141.MirrorCS"),sQuery(id+"F0.wireOp",EDGE,"E142.MirrorCS"),sQuery(id+"F0.wireOp",EDGE,"E143.MirrorCS"),sQuery(id+"F0.wireOp",EDGE,"E146.MirrorCS"),sQuery(id+"F0.wireOp",EDGE,"E148.MirrorCS"),sQuery(id+"F0.wireOp",EDGE,"E149.MirrorCS"),sQuery(id+"F0.wireOp",EDGE,"E150.MirrorCS"),sQuery(id+"F0.wireOp",EDGE,"E152.MirrorCS"),sQuery(id+"F0.wireOp",EDGE,"E153.MirrorCS"),sQuery(id+"F0.wireOp",EDGE,"E154.MirrorCS"),sQuery(id+"F0.wireOp",EDGE,"E155.MirrorCS"),sQuery(id+"F0.wireOp",EDGE,"E156.MirrorCS"),sQuery(id+"F0.wireOp",EDGE,"E157.MirrorCS"),sQuery(id+"F0.wireOp",EDGE,"E158.MirrorCS"),sQuery(id+"F0.wireOp",EDGE,"E159.MirrorCS"),sQuery(id+"F0.wireOp",EDGE,"E160.MirrorCS"),sQuery(id+"F0.wireOp",EDGE,"E161.MirrorCS"),sQuery(id+"F0.wireOp",EDGE,"E162.MirrorCS"),sQuery(id+"F0.wireOp",EDGE,"E163.MirrorCS"),sQuery(id+"F0.wireOp",EDGE,"E164.MirrorCS"),sQuery(id+"F0.wireOp",EDGE,"E166.MirrorCS"),sQuery(id+"F0.wireOp",EDGE,"E167.MirrorCS"),sQuery(id+"F0.wireOp",EDGE,"E168.MirrorCS"),sQuery(id+"F0.wireOp",EDGE,"E170.MirrorCS"),sQuery(id+"F0.wireOp",EDGE,"E171.MirrorCS"),sQuery(id+"F0.wireOp",EDGE,"E173.MirrorCS"),sQuery(id+"F0.wireOp",EDGE,"E174.MirrorCS"),sQuery(id+"F0.wireOp",EDGE,"E176.MirrorCS"),sQuery(id+"F0.wireOp",EDGE,"E177.MirrorCS"),sQuery(id+"F0.wireOp",EDGE,"E178.MirrorCS"),sQuery(id+"F0.wireOp",EDGE,"E180.MirrorCS"),sQuery(id+"F0.wireOp",EDGE,"E182.MirrorCS"),sQuery(id+"F0.wireOp",EDGE,"E183.MirrorCS"),sQuery(id+"F0.wireOp",EDGE,"E184.MirrorCS"),sQuery(id+"F0.wireOp",EDGE,"E185.MirrorCS"),sQuery(id+"F0.wireOp",EDGE,"E186.MirrorCS"),sQuery(id+"F0.wireOp",EDGE,"E187.MirrorCS"),sQuery(id+"F0.wireOp",EDGE,"E189.MirrorCS"),sQuery(id+"F0.wireOp",EDGE,"E190.MirrorCS"),sQuery(id+"F0.wireOp",EDGE,"E191.MirrorCS"),sQuery(id+"F0.wireOp",EDGE,"E192.MirrorCS"),sQuery(id+"F0.wireOp",EDGE,"E193.MirrorCS"),sQuery(id+"F0.wireOp",EDGE,"E194.MirrorCS"),sQuery(id+"F0.wireOp",EDGE,"E195.MirrorCS"),sQuery(id+"F0.wireOp",EDGE,"E196.MirrorCS"),sQuery(id+"F0.wireOp",EDGE,"E197.MirrorCS"),sQuery(id+"F0.wireOp",EDGE,"E198.MirrorCS"),sQuery(id+"F0.wireOp",EDGE,"E199.MirrorCS"),sQuery(id+"F0.wireOp",EDGE,"E200.MirrorCS"),sQuery(id+"F0.wireOp",EDGE,"E201.MirrorCS"),sQuery(id+"F0.wireOp",EDGE,"E203.MirrorCS"),sQuery(id+"F0.wireOp",EDGE,"E204.MirrorCS"),sQuery(id+"F0.wireOp",EDGE,"E205.MirrorCS"),sQuery(id+"F0.wireOp",EDGE,"E206.MirrorCS"),sQuery(id+"F0.wireOp",EDGE,"E210.MirrorCS"),sQuery(id+"F0.wireOp",EDGE,"E212.MirrorCS"),sQuery(id+"F0.wireOp",EDGE,"E213.MirrorCS"),sQuery(id+"F0.wireOp",EDGE,"E216.MirrorCS"),sQuery(id+"F0.wireOp",EDGE,"E218.MirrorCS"),sQuery(id+"F0.wireOp",EDGE,"E220.MirrorCS"),sQuery(id+"F0.wireOp",EDGE,"E221.MirrorCS"),sQuery(id+"F0.wireOp",EDGE,"E222.MirrorCS"),sQuery(id+"F0.wireOp",EDGE,"E223.MirrorCS"),sQuery(id+"F0.wireOp",EDGE,"E224.MirrorCS"),sQuery(id+"F0.wireOp",EDGE,"E225.MirrorCS"),sQuery(id+"F0.wireOp",EDGE,"E227.MirrorCS"),sQuery(id+"F0.wireOp",EDGE,"E228.MirrorCS"),sQuery(id+"F0.wireOp",EDGE,"E229.MirrorCS"),sQuery(id+"F0.wireOp",EDGE,"E230.MirrorCS"),sQuery(id+"F0.wireOp",EDGE,"E231.MirrorCS"),sQuery(id+"F0.wireOp",EDGE,"E232.MirrorCS"),sQuery(id+"F0.wireOp",EDGE,"E233.MirrorCS"),sQuery(id+"F0.wireOp",EDGE,"E234.MirrorCS"),sQuery(id+"F0.wireOp",EDGE,"E237.MirrorCS"),sQuery(id+"F0.wireOp",EDGE,"E238.MirrorCS"),sQuery(id+"F0.wireOp",EDGE,"E241.MirrorCS"),sQuery(id+"F0.wireOp",EDGE,"E242.MirrorCS"),sQuery(id+"F0.wireOp",EDGE,"E246.MirrorCS"),sQuery(id+"F0.wireOp",EDGE,"E252.MirrorCS"),sQuery(id+"F0.wireOp",EDGE,"E274.MirrorCS"),sQuery(id+"F0.wireOp",EDGE,"E275.MirrorCS"),sQuery(id+"F0.wireOp",EDGE,"E276.MirrorCS"),sQuery(id+"F0.wireOp",EDGE,"E277.MirrorCS"),sQuery(id+"F0.wireOp",EDGE,"E278.MirrorCS"),sQuery(id+"F0.wireOp",EDGE,"E279.MirrorCS"),sQuery(id+"F0.wireOp",EDGE,"E280.MirrorCS"),sQuery(id+"F0.wireOp",EDGE,"E281.MirrorCS"),sQuery(id+"F0.wireOp",EDGE,"E283.MirrorCS"),sQuery(id+"F0.wireOp",EDGE,"E285.MirrorCS"),sQuery(id+"F0.wireOp",EDGE,"E286.MirrorCS"),sQuery(id+"F0.wireOp",EDGE,"E287.MirrorCS"),sQuery(id+"F0.wireOp",EDGE,"E289.MirrorCS"),sQuery(id+"F0.wireOp",EDGE,"E290.MirrorCS"),sQuery(id+"F0.wireOp",EDGE,"E291.MirrorCS"),sQuery(id+"F0.wireOp",EDGE,"E292.MirrorCS"),sQuery(id+"F0.wireOp",EDGE,"E294.MirrorCS"),sQuery(id+"F0.wireOp",EDGE,"E295.MirrorCS"),sQuery(id+"F0.wireOp",EDGE,"E296.MirrorCS"),sQuery(id+"F0.wireOp",EDGE,"E297.MirrorCS"),sQuery(id+"F0.wireOp",EDGE,"E298.MirrorCS"),sQuery(id+"F0.wireOp",EDGE,"E299.MirrorCS"),sQuery(id+"F0.wireOp",EDGE,"E300.MirrorCS"),sQuery(id+"F0.wireOp",EDGE,"E301.MirrorCS"),sQuery(id+"F0.wireOp",EDGE,"E302.MirrorCS"),sQuery(id+"F0.wireOp",EDGE,"E303.MirrorCS"),sQuery(id+"F0.wireOp",EDGE,"E304.MirrorCS"),sQuery(id+"F0.wireOp",EDGE,"E305.MirrorCS"),sQuery(id+"F0.wireOp",EDGE,"E306.MirrorCS"),sQuery(id+"F0.wireOp",EDGE,"E308.MirrorCS"),sQuery(id+"F0.wireOp",EDGE,"E309.MirrorCS"),sQuery(id+"F0.wireOp",EDGE,"E310.MirrorCS"),sQuery(id+"F0.wireOp",EDGE,"E311.MirrorCS"),sQuery(id+"F0.wireOp",EDGE,"E312.MirrorCS"),sQuery(id+"F0.wireOp",EDGE,"E313.MirrorCS"),sQuery(id+"F0.wireOp",EDGE,"E315.MirrorCS"),sQuery(id+"F0.wireOp",EDGE,"E316.MirrorCS"),sQuery(id+"F0.wireOp",EDGE,"E317.MirrorCS"),sQuery(id+"F0.wireOp",EDGE,"E318.MirrorCS"),sQuery(id+"F0.wireOp",EDGE,"E319.MirrorCS"),sQuery(id+"F0.wireOp",EDGE,"E320.MirrorCS"),sQuery(id+"F0.wireOp",EDGE,"E321.MirrorCS"),sQuery(id+"F0.wireOp",EDGE,"E322.MirrorCS"),sQuery(id+"F0.wireOp",EDGE,"E323.MirrorCS"),sQuery(id+"F0.wireOp",EDGE,"E324.MirrorCS"),sQuery(id+"F0.wireOp",EDGE,"E327.MirrorCS"),sQuery(id+"F0.wireOp",EDGE,"E329.MirrorCS"),sQuery(id+"F0.wireOp",EDGE,"E331.MirrorCS"),sQuery(id+"F0.wireOp",EDGE,"E333.MirrorCS"),sQuery(id+"F0.wireOp",EDGE,"E334.MirrorCS"),sQuery(id+"F0.wireOp",EDGE,"E335.MirrorCS"),sQuery(id+"F0.wireOp",EDGE,"E336.MirrorCS"),sQuery(id+"F0.wireOp",EDGE,"E337.MirrorCS"),sQuery(id+"F0.wireOp",EDGE,"E338.MirrorCS"),sQuery(id+"F0.wireOp",EDGE,"E339.MirrorCS"),sQuery(id+"F0.wireOp",EDGE,"E340.MirrorCS"),sQuery(id+"F0.wireOp",EDGE,"E341.MirrorCS"),sQuery(id+"F0.wireOp",EDGE,"E342.MirrorCS"),sQuery(id+"F0.wireOp",EDGE,"E344.MirrorCS"),sQuery(id+"F0.wireOp",EDGE,"E345.MirrorCS"),sQuery(id+"F0.wireOp",EDGE,"E346.MirrorCS"),sQuery(id+"F0.wireOp",EDGE,"E347.MirrorCS"),sQuery(id+"F0.wireOp",EDGE,"E348.MirrorCS"),sQuery(id+"F0.wireOp",EDGE,"E349.MirrorCS"),sQuery(id+"F0.wireOp",EDGE,"E350.MirrorCS"),sQuery(id+"F0.wireOp",EDGE,"E351.MirrorCS"),sQuery(id+"F0.wireOp",EDGE,"E352.MirrorCS"),sQuery(id+"F0.wireOp",EDGE,"E353.MirrorCS"),sQuery(id+"F0.wireOp",EDGE,"E354.MirrorCS"),sQuery(id+"F0.wireOp",EDGE,"E355.MirrorCS"),sQuery(id+"F0.wireOp",EDGE,"E356.MirrorCS"),sQuery(id+"F0.wireOp",EDGE,"E358.MirrorCS"),sQuery(id+"F0.wireOp",EDGE,"E359.MirrorCS"),sQuery(id+"F0.wireOp",EDGE,"E361.MirrorCS"),sQuery(id+"F0.wireOp",EDGE,"E362.MirrorCS"),sQuery(id+"F0.wireOp",EDGE,"E364.MirrorCS"),sQuery(id+"F0.wireOp",EDGE,"E365.MirrorCS"),sQuery(id+"F0.wireOp",EDGE,"E366.MirrorCS"),sQuery(id+"F0.wireOp",EDGE,"E367.MirrorCS"),sQuery(id+"F0.wireOp",EDGE,"E370.MirrorCS"),sQuery(id+"F0.wireOp",EDGE,"E371.MirrorCS"),sQuery(id+"F0.wireOp",EDGE,"E372.MirrorCS"),sQuery(id+"F0.wireOp",EDGE,"E373.MirrorCS"),sQuery(id+"F0.wireOp",EDGE,"E374.MirrorCS"),sQuery(id+"F0.wireOp",EDGE,"E375.MirrorCS"),sQuery(id+"F0.wireOp",EDGE,"E376.MirrorCS"),sQuery(id+"F0.wireOp",EDGE,"E377.MirrorCS"),sQuery(id+"F0.wireOp",EDGE,"E378.MirrorCS"),sQuery(id+"F0.wireOp",EDGE,"E379.MirrorCS"),sQuery(id+"F0.wireOp",EDGE,"E380.MirrorCS"),sQuery(id+"F0.wireOp",EDGE,"E381.MirrorCS"),sQuery(id+"F0.wireOp",EDGE,"E383.MirrorCS"),sQuery(id+"F0.wireOp",EDGE,"E384.MirrorCS"),sQuery(id+"F0.wireOp",EDGE,"E386.MirrorCS"),sQuery(id+"F0.wireOp",EDGE,"E387.MirrorCS"),sQuery(id+"F0.wireOp",EDGE,"E388.MirrorCS"),sQuery(id+"F0.wireOp",EDGE,"E389.MirrorCS"),sQuery(id+"F0.wireOp",EDGE,"E390.MirrorCS"),sQuery(id+"F0.wireOp",EDGE,"E391.MirrorCS"),sQuery(id+"F0.wireOp",EDGE,"E393.MirrorCS"),sQuery(id+"F0.wireOp",EDGE,"E395.MirrorCS"),sQuery(id+"F0.wireOp",EDGE,"E396.MirrorCS"),sQuery(id+"F0.wireOp",EDGE,"E397.MirrorCS"),sQuery(id+"F0.wireOp",EDGE,"E398.MirrorCS"),sQuery(id+"F0.wireOp",EDGE,"E400.MirrorCS"),sQuery(id+"F0.wireOp",EDGE,"E401.MirrorCS"),sQuery(id+"F0.wireOp",EDGE,"E403.MirrorCS"),sQuery(id+"F0.wireOp",EDGE,"E404.MirrorCS"),sQuery(id+"F0.wireOp",EDGE,"E405.MirrorCS"),sQuery(id+"F0.wireOp",EDGE,"E406.MirrorCS"),sQuery(id+"F0.wireOp",EDGE,"E407.MirrorCS"),sQuery(id+"F0.wireOp",EDGE,"E408.MirrorCS"),sQuery(id+"F0.wireOp",EDGE,"E409.MirrorCS"),sQuery(id+"F0.wireOp",EDGE,"E410.MirrorCS"),sQuery(id+"F0.wireOp",EDGE,"E411.MirrorCS"),sQuery(id+"F0.wireOp",EDGE,"E412.MirrorCS"),sQuery(id+"F0.wireOp",EDGE,"E413.MirrorCS"),sQuery(id+"F0.wireOp",EDGE,"E415.MirrorCS"),sQuery(id+"F0.wireOp",EDGE,"E416.MirrorCS"),sQuery(id+"F0.wireOp",EDGE,"E417.MirrorCS"),sQuery(id+"F0.wireOp",EDGE,"E418.MirrorCS"),sQuery(id+"F0.wireOp",EDGE,"E419.MirrorCS"),sQuery(id+"F0.wireOp",EDGE,"E420.MirrorCS"),sQuery(id+"F0.wireOp",EDGE,"E421.MirrorCS"),sQuery(id+"F0.wireOp",EDGE,"E422.MirrorCS"),sQuery(id+"F0.wireOp",EDGE,"E423.MirrorCS"),sQuery(id+"F0.wireOp",EDGE,"E424.MirrorCS"),sQuery(id+"F0.wireOp",EDGE,"E425.MirrorCS"),sQuery(id+"F0.wireOp",EDGE,"E426.MirrorCS"),sQuery(id+"F0.wireOp",EDGE,"E427.MirrorCS"),sQuery(id+"F0.wireOp",EDGE,"E428.MirrorCS"),sQuery(id+"F0.wireOp",EDGE,"E429.MirrorCS"),sQuery(id+"F0.wireOp",EDGE,"E430.MirrorCS"),sQuery(id+"F0.wireOp",EDGE,"E432.MirrorCS"),sQuery(id+"F0.wireOp",EDGE,"E433.MirrorCS"),sQuery(id+"F0.wireOp",EDGE,"E434.MirrorCS"),sQuery(id+"F0.wireOp",EDGE,"E436.MirrorCS"),sQuery(id+"F0.wireOp",EDGE,"E437.MirrorCS"),sQuery(id+"F0.wireOp",EDGE,"E438.MirrorCS"),sQuery(id+"F0.wireOp",EDGE,"E439.MirrorCS"),sQuery(id+"F0.wireOp",EDGE,"E440.MirrorCS"),sQuery(id+"F0.wireOp",EDGE,"E441.MirrorCS"),sQuery(id+"F0.wireOp",EDGE,"E442.MirrorCS"),sQuery(id+"F0.wireOp",EDGE,"E443.MirrorCS"),sQuery(id+"F0.wireOp",EDGE,"E444.MirrorCS"),sQuery(id+"F0.wireOp",EDGE,"E445.MirrorCS"),sQuery(id+"F0.wireOp",EDGE,"E446.MirrorCS"),sQuery(id+"F0.wireOp",EDGE,"E469.MirrorCS"),sQuery(id+"F0.wireOp",EDGE,"E477.MirrorCS"),sQuery(id+"F0.wireOp",EDGE,"E525.MirrorCS"),sQuery(id+"F0.wireOp",EDGE,"E526.MirrorCS"),sQuery(id+"F0.wireOp",EDGE,"E527.MirrorCS"),sQuery(id+"F0.wireOp",EDGE,"E528.MirrorCS"),sQuery(id+"F0.wireOp",EDGE,"E529.MirrorCS"),sQuery(id+"F0.wireOp",EDGE,"E530.MirrorCS"),sQuery(id+"F0.wireOp",EDGE,"E531.MirrorCS"),sQuery(id+"F0.wireOp",EDGE,"E532.MirrorCS"),sQuery(id+"F0.wireOp",EDGE,"E533.MirrorCS"),sQuery(id+"F0.wireOp",EDGE,"E534.MirrorCS"),sQuery(id+"F0.wireOp",EDGE,"E535.MirrorCS"),sQuery(id+"F0.wireOp",EDGE,"E536.MirrorCS"),sQuery(id+"F0.wireOp",EDGE,"E537.MirrorCS"),sQuery(id+"F0.wireOp",EDGE,"E538.MirrorCS"),sQuery(id+"F0.wireOp",EDGE,"E539.MirrorCS"),sQuery(id+"F0.wireOp",EDGE,"E541.MirrorCS"),sQuery(id+"F0.wireOp",EDGE,"E542.MirrorCS"),sQuery(id+"F0.wireOp",EDGE,"E543.MirrorCS"),sQuery(id+"F0.wireOp",EDGE,"E544.MirrorCS"),sQuery(id+"F0.wireOp",EDGE,"E545.MirrorCS"),sQuery(id+"F0.wireOp",EDGE,"E546.MirrorCS"),sQuery(id+"F0.wireOp",EDGE,"E547.MirrorCS"),sQuery(id+"F0.wireOp",EDGE,"E548.MirrorCS"),sQuery(id+"F0.wireOp",EDGE,"E549.MirrorCS"),sQuery(id+"F0.wireOp",EDGE,"E551.MirrorCS"),sQuery(id+"F0.wireOp",EDGE,"E553.MirrorCS"),sQuery(id+"F0.wireOp",EDGE,"E555.MirrorCS"),sQuery(id+"F0.wireOp",EDGE,"E556.MirrorCS"),sQuery(id+"F0.wireOp",EDGE,"E557.MirrorCS"),sQuery(id+"F0.wireOp",EDGE,"E558.MirrorCS"),sQuery(id+"F0.wireOp",EDGE,"E559.MirrorCS"),sQuery(id+"F0.wireOp",EDGE,"E560.MirrorCS"),sQuery(id+"F0.wireOp",EDGE,"E561.MirrorCS"),sQuery(id+"F0.wireOp",EDGE,"E562.MirrorCS"),sQuery(id+"F0.wireOp",EDGE,"E563.MirrorCS"),sQuery(id+"F0.wireOp",EDGE,"E564.MirrorCS"),sQuery(id+"F0.wireOp",EDGE,"E565.MirrorCS"),sQuery(id+"F0.wireOp",EDGE,"E566.MirrorCS"),sQuery(id+"F0.wireOp",EDGE,"E567.MirrorCS"),sQuery(id+"F0.wireOp",EDGE,"E568.MirrorCS"),sQuery(id+"F0.wireOp",EDGE,"E569.MirrorCS"),sQuery(id+"F0.wireOp",EDGE,"E570.MirrorCS"),sQuery(id+"F0.wireOp",EDGE,"E571.MirrorCS"),sQuery(id+"F0.wireOp",EDGE,"E572.MirrorCS"),sQuery(id+"F0.wireOp",EDGE,"E575.MirrorCS"),sQuery(id+"F0.wireOp",EDGE,"E576.MirrorCS"),sQuery(id+"F0.wireOp",EDGE,"E577.MirrorCS"),sQuery(id+"F0.wireOp",EDGE,"E578.MirrorCS"),sQuery(id+"F0.wireOp",EDGE,"E580.MirrorCS"),sQuery(id+"F0.wireOp",EDGE,"E581.MirrorCS"),sQuery(id+"F0.wireOp",EDGE,"E582.MirrorCS"),sQuery(id+"F0.wireOp",EDGE,"E584.MirrorCS"),sQuery(id+"F0.wireOp",EDGE,"E585.MirrorCS"),sQuery(id+"F0.wireOp",EDGE,"E586.MirrorCS"),sQuery(id+"F0.wireOp",EDGE,"E587.MirrorCS"),sQuery(id+"F0.wireOp",EDGE,"E588.MirrorCS"),sQuery(id+"F0.wireOp",EDGE,"E589.MirrorCS"),sQuery(id+"F0.wireOp",EDGE,"E591.MirrorCS"),sQuery(id+"F0.wireOp",EDGE,"E592.MirrorCS"),sQuery(id+"F0.wireOp",EDGE,"E593.MirrorCS"),sQuery(id+"F0.wireOp",EDGE,"E594.MirrorCS"),sQuery(id+"F0.wireOp",EDGE,"E595.MirrorCS"),sQuery(id+"F0.wireOp",EDGE,"E596.MirrorCS"),sQuery(id+"F0.wireOp",EDGE,"E597.MirrorCS"),sQuery(id+"F0.wireOp",EDGE,"E598.MirrorCS"),sQuery(id+"F0.wireOp",EDGE,"E599.MirrorCS"),sQuery(id+"F0.wireOp",EDGE,"E600.MirrorCS"),sQuery(id+"F0.wireOp",EDGE,"E601.MirrorCS"),sQuery(id+"F0.wireOp",EDGE,"E602.MirrorCS"),sQuery(id+"F0.wireOp",EDGE,"E603.MirrorCS"),sQuery(id+"F0.wireOp",EDGE,"E604.MirrorCS"),sQuery(id+"F0.wireOp",EDGE,"E605.MirrorCS"),sQuery(id+"F0.wireOp",EDGE,"E606.MirrorCS"),sQuery(id+"F0.wireOp",EDGE,"E607.MirrorCS"),sQuery(id+"F0.wireOp",EDGE,"E608.MirrorCS"),sQuery(id+"F0.wireOp",EDGE,"E609.MirrorCS"),sQuery(id+"F0.wireOp",EDGE,"E610.MirrorCS"),sQuery(id+"F0.wireOp",EDGE,"E611.MirrorCS"),sQuery(id+"F0.wireOp",EDGE,"E612.MirrorCS"),sQuery(id+"F0.wireOp",EDGE,"E613.MirrorCS"),sQuery(id+"F0.wireOp",EDGE,"E614.MirrorCS"),sQuery(id+"F0.wireOp",EDGE,"E616.MirrorCS"),sQuery(id+"F0.wireOp",EDGE,"E617.MirrorCS"),sQuery(id+"F0.wireOp",EDGE,"E618.MirrorCS"),sQuery(id+"F0.wireOp",EDGE,"E619.MirrorCS"),sQuery(id+"F0.wireOp",EDGE,"E620.MirrorCS"),sQuery(id+"F0.wireOp",EDGE,"E621.MirrorCS"),sQuery(id+"F0.wireOp",EDGE,"E622.MirrorCS"),sQuery(id+"F0.wireOp",EDGE,"E623.MirrorCS"),sQuery(id+"F0.wireOp",EDGE,"E624.MirrorCS"),sQuery(id+"F0.wireOp",EDGE,"E625.MirrorCS"),sQuery(id+"F0.wireOp",EDGE,"E626.MirrorCS"),sQuery(id+"F0.wireOp",EDGE,"E628.MirrorCS"),sQuery(id+"F0.wireOp",EDGE,"E629.MirrorCS"),sQuery(id+"F0.wireOp",EDGE,"E630.MirrorCS"),sQuery(id+"F0.wireOp",EDGE,"E632.MirrorCS"),sQuery(id+"F0.wireOp",EDGE,"E633.MirrorCS"),sQuery(id+"F0.wireOp",EDGE,"E635.MirrorCS"),sQuery(id+"F0.wireOp",EDGE,"E636.MirrorCS"),sQuery(id+"F0.wireOp",EDGE,"E637.MirrorCS"),sQuery(id+"F0.wireOp",EDGE,"E638.MirrorCS"),sQuery(id+"F0.wireOp",EDGE,"E639.MirrorCS"),sQuery(id+"F0.wireOp",EDGE,"E640.MirrorCS"),sQuery(id+"F0.wireOp",EDGE,"E641.MirrorCS"),sQuery(id+"F0.wireOp",EDGE,"E642.MirrorCS"),sQuery(id+"F0.wireOp",EDGE,"E643.MirrorCS"),sQuery(id+"F0.wireOp",EDGE,"E644.MirrorCS"),sQuery(id+"F0.wireOp",EDGE,"E645.MirrorCS"),sQuery(id+"F0.wireOp",EDGE,"E646.MirrorCS"),sQuery(id+"F0.wireOp",EDGE,"E647.MirrorCS"),sQuery(id+"F0.wireOp",EDGE,"E648.MirrorCS"),sQuery(id+"F0.wireOp",EDGE,"E649.MirrorCS"),sQuery(id+"F0.wireOp",EDGE,"E650.MirrorCS"),sQuery(id+"F0.wireOp",EDGE,"E651.MirrorCS"),sQuery(id+"F0.wireOp",EDGE,"E652.MirrorCS"),sQuery(id+"F0.wireOp",EDGE,"E653.MirrorCS"),sQuery(id+"F0.wireOp",EDGE,"E654.MirrorCS"),sQuery(id+"F0.wireOp",EDGE,"E655.MirrorCS"),sQuery(id+"F0.wireOp",EDGE,"E656.MirrorCS"),sQuery(id+"F0.wireOp",EDGE,"E657.MirrorCS"),sQuery(id+"F0.wireOp",EDGE,"E658.MirrorCS"),sQuery(id+"F0.wireOp",EDGE,"E659.MirrorCS"),sQuery(id+"F0.wireOp",EDGE,"E660.MirrorCS"),sQuery(id+"F0.wireOp",EDGE,"E661.MirrorCS"),sQuery(id+"F0.wireOp",EDGE,"E662.MirrorCS"),sQuery(id+"F0.wireOp",EDGE,"E663.MirrorCS"),sQuery(id+"F0.wireOp",EDGE,"E664.MirrorCS"),sQuery(id+"F0.wireOp",EDGE,"E665.MirrorCS"),sQuery(id+"F0.wireOp",EDGE,"E667.MirrorCS"),sQuery(id+"F0.wireOp",EDGE,"E668.MirrorCS"),sQuery(id+"F0.wireOp",EDGE,"E669.MirrorCS"),sQuery(id+"F0.wireOp",EDGE,"E670.MirrorCS"),sQuery(id+"F0.wireOp",EDGE,"E671.MirrorCS"),sQuery(id+"F0.wireOp",EDGE,"E672.MirrorCS"),sQuery(id+"F0.wireOp",EDGE,"E673.MirrorCS"),sQuery(id+"F0.wireOp",EDGE,"E674.MirrorCS"),sQuery(id+"F0.wireOp",EDGE,"E675.MirrorCS"),sQuery(id+"F0.wireOp",EDGE,"E676.MirrorCS"),sQuery(id+"F0.wireOp",EDGE,"E677.MirrorCS"),sQuery(id+"F0.wireOp",EDGE,"E679.MirrorCS"),sQuery(id+"F0.wireOp",EDGE,"E680.MirrorCS"),sQuery(id+"F0.wireOp",EDGE,"E681.MirrorCS"),sQuery(id+"F0.wireOp",EDGE,"E682.MirrorCS"),sQuery(id+"F0.wireOp",EDGE,"E683.MirrorCS"),sQuery(id+"F0.wireOp",EDGE,"E684.MirrorCS"),sQuery(id+"F0.wireOp",EDGE,"E685.MirrorCS"),sQuery(id+"F0.wireOp",EDGE,"E686.MirrorCS"),sQuery(id+"F0.wireOp",EDGE,"E687.MirrorCS"),sQuery(id+"F0.wireOp",EDGE,"E690.MirrorCS"),sQuery(id+"F0.wireOp",EDGE,"E691.MirrorCS"),sQuery(id+"F0.wireOp",EDGE,"E692.MirrorCS"),sQuery(id+"F0.wireOp",EDGE,"E693.MirrorCS"),sQuery(id+"F0.wireOp",EDGE,"E694.MirrorCS"),sQuery(id+"F0.wireOp",EDGE,"E695.MirrorCS"),sQuery(id+"F0.wireOp",EDGE,"E696.MirrorCS"),sQuery(id+"F0.wireOp",EDGE,"E697.MirrorCS"),sQuery(id+"F0.wireOp",EDGE,"E698.MirrorCS"),sQuery(id+"F0.wireOp",EDGE,"E699.MirrorCS"),sQuery(id+"F0.wireOp",EDGE,"E701.MirrorCS"),sQuery(id+"F0.wireOp",EDGE,"E702.MirrorCS"),sQuery(id+"F0.wireOp",EDGE,"E703.MirrorCS"),sQuery(id+"F0.wireOp",EDGE,"E704.MirrorCS"),sQuery(id+"F0.wireOp",EDGE,"E705.MirrorCS"),sQuery(id+"F0.wireOp",EDGE,"E706.MirrorCS"),sQuery(id+"F0.wireOp",EDGE,"E707.MirrorCS"),sQuery(id+"F0.wireOp",EDGE,"E708.MirrorCS"),sQuery(id+"F0.wireOp",EDGE,"E709.MirrorCS"),sQuery(id+"F0.wireOp",EDGE,"E710.MirrorCS"),sQuery(id+"F0.wireOp",EDGE,"E711.MirrorCS"),sQuery(id+"F0.wireOp",EDGE,"E712.MirrorCS"),sQuery(id+"F0.wireOp",EDGE,"E713.MirrorCS"),sQuery(id+"F0.wireOp",EDGE,"E714.MirrorCS"),sQuery(id+"F0.wireOp",EDGE,"E715.MirrorCS"),sQuery(id+"F0.wireOp",EDGE,"E716.MirrorCS"),sQuery(id+"F0.wireOp",EDGE,"E717.MirrorCS"),sQuery(id+"F0.wireOp",EDGE,"E718.MirrorCS"),sQuery(id+"F0.wireOp",EDGE,"E719.MirrorCS"),sQuery(id+"F0.wireOp",EDGE,"E720.MirrorCS"),sQuery(id+"F0.wireOp",EDGE,"E721.MirrorCS"),sQuery(id+"F0.wireOp",EDGE,"E722.MirrorCS"),sQuery(id+"F0.wireOp",EDGE,"E723.MirrorCS"),sQuery(id+"F0.wireOp",EDGE,"E724.MirrorCS"),sQuery(id+"F0.wireOp",EDGE,"E725.MirrorCS"),sQuery(id+"F0.wireOp",EDGE,"E726.MirrorCS"),sQuery(id+"F0.wireOp",EDGE,"E727.MirrorCS"),sQuery(id+"F0.wireOp",EDGE,"E728.MirrorCS"),sQuery(id+"F0.wireOp",EDGE,"E729.MirrorCS"),sQuery(id+"F0.wireOp",EDGE,"E730.MirrorCS"),sQuery(id+"F0.wireOp",EDGE,"E731.MirrorCS"),sQuery(id+"F0.wireOp",EDGE,"E732.MirrorCS"),sQuery(id+"F0.wireOp",EDGE,"E734.MirrorCS"),sQuery(id+"F0.wireOp",EDGE,"E735.MirrorCS"),sQuery(id+"F0.wireOp",EDGE,"E736.MirrorCS"),sQuery(id+"F0.wireOp",EDGE,"E737.MirrorCS"),sQuery(id+"F0.wireOp",EDGE,"E738.MirrorCS"),sQuery(id+"F0.wireOp",EDGE,"E739.MirrorCS"),sQuery(id+"F0.wireOp",EDGE,"E740.MirrorCS"),sQuery(id+"F0.wireOp",EDGE,"E741.MirrorCS"),sQuery(id+"F0.wireOp",EDGE,"E743.MirrorCS"),sQuery(id+"F0.wireOp",EDGE,"E744.MirrorCS"),sQuery(id+"F0.wireOp",EDGE,"E745.MirrorCS"),sQuery(id+"F0.wireOp",EDGE,"E746.MirrorCS"),sQuery(id+"F0.wireOp",EDGE,"E747.MirrorCS"),sQuery(id+"F0.wireOp",EDGE,"E748.MirrorCS"),sQuery(id+"F0.wireOp",EDGE,"E749.MirrorCS"),sQuery(id+"F0.wireOp",EDGE,"E750.MirrorCS"),sQuery(id+"F0.wireOp",EDGE,"E751.MirrorCS"),sQuery(id+"F0.wireOp",EDGE,"E752.MirrorCS"),sQuery(id+"F0.wireOp",EDGE,"E753.MirrorCS"),sQuery(id+"F0.wireOp",EDGE,"E754.MirrorCS"),sQuery(id+"F0.wireOp",EDGE,"E755.MirrorCS"),sQuery(id+"F0.wireOp",EDGE,"E756.MirrorCS"),sQuery(id+"F0.wireOp",EDGE,"E757.MirrorCS"),sQuery(id+"F0.wireOp",EDGE,"E758.MirrorCS"),sQuery(id+"F0.wireOp",EDGE,"E760.MirrorCS"),sQuery(id+"F0.wireOp",EDGE,"E761.MirrorCS"),sQuery(id+"F0.wireOp",EDGE,"E762.MirrorCS"),sQuery(id+"F0.wireOp",EDGE,"E763.MirrorCS"),sQuery(id+"F0.wireOp",EDGE,"E765.MirrorCS"),sQuery(id+"F0.wireOp",EDGE,"E766.MirrorCS"),sQuery(id+"F0.wireOp",EDGE,"E767.MirrorCS"),sQuery(id+"F0.wireOp",EDGE,"E770.MirrorCS"),sQuery(id+"F0.wireOp",EDGE,"E771.MirrorCS"),sQuery(id+"F0.wireOp",EDGE,"E772.MirrorCS"),sQuery(id+"F0.wireOp",EDGE,"E773.MirrorCS"),sQuery(id+"F0.wireOp",EDGE,"E774.MirrorCS"),sQuery(id+"F0.wireOp",EDGE,"E775.MirrorCS"),sQuery(id+"F0.wireOp",EDGE,"E776.MirrorCS"),sQuery(id+"F0.wireOp",EDGE,"E777.MirrorCS"),sQuery(id+"F0.wireOp",EDGE,"E778.MirrorCS"),sQuery(id+"F0.wireOp",EDGE,"E779.MirrorCS"),sQuery(id+"F0.wireOp",EDGE,"E781.MirrorCS"),sQuery(id+"F0.wireOp",EDGE,"E782.MirrorCS"),sQuery(id+"F0.wireOp",EDGE,"E783.MirrorCS"),sQuery(id+"F0.wireOp",EDGE,"E784.MirrorCS"),sQuery(id+"F0.wireOp",EDGE,"E785.MirrorCS"),sQuery(id+"F0.wireOp",EDGE,"E786.MirrorCS"),sQuery(id+"F0.wireOp",EDGE,"E787.MirrorCS"),sQuery(id+"F0.wireOp",EDGE,"E788.MirrorCS"),sQuery(id+"F0.wireOp",EDGE,"E789.MirrorCS"),sQuery(id+"F0.wireOp",EDGE,"E790.MirrorCS"),sQuery(id+"F0.wireOp",EDGE,"E791.MirrorCS"),sQuery(id+"F0.wireOp",EDGE,"E792.MirrorCS"),sQuery(id+"F0.wireOp",EDGE,"E793.MirrorCS"),sQuery(id+"F0.wireOp",EDGE,"E794.MirrorCS"),sQuery(id+"F0.wireOp",EDGE,"E795.MirrorCS"),sQuery(id+"F0.wireOp",EDGE,"E796.MirrorCS"),sQuery(id+"F0.wireOp",EDGE,"E797.MirrorCS"),sQuery(id+"F0.wireOp",EDGE,"E798.MirrorCS"),sQuery(id+"F0.wireOp",EDGE,"E799.MirrorCS"),sQuery(id+"F0.wireOp",EDGE,"E800.MirrorCS"),sQuery(id+"F0.wireOp",EDGE,"E801.MirrorCS"),sQuery(id+"F0.wireOp",EDGE,"E802.MirrorCS"),sQuery(id+"F0.wireOp",EDGE,"E803.MirrorCS"),sQuery(id+"F0.wireOp",EDGE,"E804.MirrorCS"),sQuery(id+"F0.wireOp",EDGE,"E805.MirrorCS"),sQuery(id+"F0.wireOp",EDGE,"E806.MirrorCS"),sQuery(id+"F0.wireOp",EDGE,"E807.MirrorCS"),sQuery(id+"F0.wireOp",EDGE,"E808.MirrorCS"),sQuery(id+"F0.wireOp",EDGE,"E809.MirrorCS"),sQuery(id+"F0.wireOp",EDGE,"E810.MirrorCS"),sQuery(id+"F0.wireOp",EDGE,"E811.MirrorCS"),sQuery(id+"F0.wireOp",EDGE,"E812.MirrorCS"),sQuery(id+"F0.wireOp",EDGE,"E813.MirrorCS"),sQuery(id+"F0.wireOp",EDGE,"E814.MirrorCS"),sQuery(id+"F0.wireOp",EDGE,"E815.MirrorCS"),sQuery(id+"F0.wireOp",EDGE,"E816.MirrorCS"),sQuery(id+"F0.wireOp",EDGE,"E817.MirrorCS"),sQuery(id+"F0.wireOp",EDGE,"E818.MirrorCS"),sQuery(id+"F0.wireOp",EDGE,"E819.MirrorCS"),sQuery(id+"F0.wireOp",EDGE,"E820.MirrorCS"),sQuery(id+"F0.wireOp",EDGE,"E821.MirrorCS"),sQuery(id+"F0.wireOp",EDGE,"E822.MirrorCS"),sQuery(id+"F0.wireOp",EDGE,"E823.MirrorCS"),sQuery(id+"F0.wireOp",EDGE,"E824.MirrorCS"),sQuery(id+"F0.wireOp",EDGE,"E825.MirrorCS"),sQuery(id+"F0.wireOp",EDGE,"E826.MirrorCS"),sQuery(id+"F0.wireOp",EDGE,"E827.MirrorCS"),sQuery(id+"F0.wireOp",EDGE,"E828.MirrorCS"),sQuery(id+"F0.wireOp",EDGE,"E829.MirrorCS"),sQuery(id+"F0.wireOp",EDGE,"E830.MirrorCS"),sQuery(id+"F0.wireOp",EDGE,"E832.MirrorCS"),sQuery(id+"F0.wireOp",EDGE,"E833.MirrorCS"),sQuery(id+"F0.wireOp",EDGE,"E834.MirrorCS"),sQuery(id+"F0.wireOp",EDGE,"E835.MirrorCS"),sQuery(id+"F0.wireOp",EDGE,"E836.MirrorCS"),sQuery(id+"F0.wireOp",EDGE,"E838.MirrorCS"),sQuery(id+"F0.wireOp",EDGE,"E839.MirrorCS"),sQuery(id+"F0.wireOp",EDGE,"E840.MirrorCS"),sQuery(id+"F0.wireOp",EDGE,"E841.MirrorCS"),sQuery(id+"F0.wireOp",EDGE,"E842.MirrorCS"),sQuery(id+"F0.wireOp",EDGE,"E843.MirrorCS"),sQuery(id+"F0.wireOp",EDGE,"E844.MirrorCS"),sQuery(id+"F0.wireOp",EDGE,"E845.MirrorCS"),sQuery(id+"F0.wireOp",EDGE,"E971.MirrorCS"),sQuery(id+"F0.wireOp",EDGE,"E972.MirrorCS"),sQuery(id+"F0.wireOp",EDGE,"E973.MirrorCS"),sQuery(id+"F0.wireOp",EDGE,"E974.MirrorCS"),sQuery(id+"F0.wireOp",EDGE,"E975.MirrorCS"),sQuery(id+"F0.wireOp",EDGE,"E976.MirrorCS"),sQuery(id+"F0.wireOp",EDGE,"E977.MirrorCS"),sQuery(id+"F0.wireOp",EDGE,"E978.MirrorCS"),sQuery(id+"F0.wireOp",EDGE,"E979.MirrorCS"),sQuery(id+"F0.wireOp",EDGE,"E980.MirrorCS"),sQuery(id+"F0.wireOp",EDGE,"E981.MirrorCS"),sQuery(id+"F0.wireOp",EDGE,"E982.MirrorCS"),sQuery(id+"F0.wireOp",EDGE,"E983.MirrorCS"),sQuery(id+"F0.wireOp",EDGE,"E984.MirrorCS"),sQuery(id+"F0.wireOp",EDGE,"E985.MirrorCS"),sQuery(id+"F0.wireOp",EDGE,"E986.MirrorCS"),sQuery(id+"F0.wireOp",EDGE,"E987.MirrorCS"),sQuery(id+"F0.wireOp",EDGE,"E988.MirrorCS"),sQuery(id+"F0.wireOp",EDGE,"E989.MirrorCS"),sQuery(id+"F0.wireOp",EDGE,"E990.MirrorCS"),sQuery(id+"F0.wireOp",EDGE,"E991.MirrorCS"),sQuery(id+"F0.wireOp",EDGE,"E992.MirrorCS"),sQuery(id+"F0.wireOp",EDGE,"E993.MirrorCS"),sQuery(id+"F0.wireOp",EDGE,"E994.MirrorCS"),sQuery(id+"F0.wireOp",EDGE,"E995.MirrorCS"),sQuery(id+"F0.wireOp",EDGE,"E996.MirrorCS"),sQuery(id+"F0.wireOp",EDGE,"E997.MirrorCS"),sQuery(id+"F0.wireOp",EDGE,"E998.MirrorCS"),sQuery(id+"F0.wireOp",EDGE,"E999.MirrorCS"),sQuery(id+"F0.wireOp",EDGE,"E1000.MirrorCS"),sQuery(id+"F0.wireOp",EDGE,"E1001.MirrorCS"),sQuery(id+"F0.wireOp",EDGE,"E1002.MirrorCS"),sQuery(id+"F0.wireOp",EDGE,"E1003.MirrorCS"),sQuery(id+"F0.wireOp",EDGE,"E1004.MirrorCS"),sQuery(id+"F0.wireOp",EDGE,"E1005.MirrorCS"),sQuery(id+"F0.wireOp",EDGE,"E1006.MirrorCS"),sQuery(id+"F0.wireOp",EDGE,"E1007.MirrorCS"),sQuery(id+"F0.wireOp",EDGE,"E1008.MirrorCS"),sQuery(id+"F0.wireOp",EDGE,"E1009.MirrorCS"),sQuery(id+"F0.wireOp",EDGE,"E1010.MirrorCS"),sQuery(id+"F0.wireOp",EDGE,"E1011.MirrorCS"),sQuery(id+"F0.wireOp",EDGE,"E1012.MirrorCS"),sQuery(id+"F0.wireOp",EDGE,"E1013.MirrorCS"),sQuery(id+"F0.wireOp",EDGE,"E1014.MirrorCS"),sQuery(id+"F0.wireOp",EDGE,"E1015.MirrorCS"),sQuery(id+"F0.wireOp",EDGE,"E1016.MirrorCS"),sQuery(id+"F0.wireOp",EDGE,"E1017.MirrorCS"),sQuery(id+"F0.wireOp",EDGE,"E1018.MirrorCS"),sQuery(id+"F0.wireOp",EDGE,"E1019.MirrorCS"),sQuery(id+"F0.wireOp",EDGE,"E1020.MirrorCS"),sQuery(id+"F0.wireOp",EDGE,"E1021.MirrorCS"),sQuery(id+"F0.wireOp",EDGE,"E1022.MirrorCS"),sQuery(id+"F0.wireOp",EDGE,"E1023.MirrorCS"),sQuery(id+"F0.wireOp",EDGE,"E1024.MirrorCS"),sQuery(id+"F0.wireOp",EDGE,"E1025.MirrorCS"),sQuery(id+"F0.wireOp",EDGE,"E1026.MirrorCS"),sQuery(id+"F0.wireOp",EDGE,"E1027.MirrorCS"),sQuery(id+"F0.wireOp",EDGE,"E1028.MirrorCS"),sQuery(id+"F0.wireOp",EDGE,"E1029.MirrorCS"),sQuery(id+"F0.wireOp",EDGE,"E1030.MirrorCS"),sQuery(id+"F0.wireOp",EDGE,"E1031.MirrorCS"),sQuery(id+"F0.wireOp",EDGE,"E1032.MirrorCS"),sQuery(id+"F0.wireOp",EDGE,"E1033.MirrorCS"),sQuery(id+"F0.wireOp",EDGE,"E1034.MirrorCS"),sQuery(id+"F0.wireOp",EDGE,"E1035.MirrorCS"),sQuery(id+"F0.wireOp",EDGE,"E1036.MirrorCS"),sQuery(id+"F0.wireOp",EDGE,"E1037.MirrorCS"),sQuery(id+"F0.wireOp",EDGE,"E1038.MirrorCS"),sQuery(id+"F0.wireOp",EDGE,"E1039.MirrorCS"),sQuery(id+"F0.wireOp",EDGE,"E1040.MirrorCS"),sQuery(id+"F0.wireOp",EDGE,"E1041.MirrorCS"),sQuery(id+"F0.wireOp",EDGE,"E1042.MirrorCS"),sQuery(id+"F0.wireOp",EDGE,"E1043.MirrorCS"),sQuery(id+"F0.wireOp",EDGE,"E1044.MirrorCS"),sQuery(id+"F0.wireOp",EDGE,"E1045.MirrorCS"),sQuery(id+"F0.wireOp",EDGE,"E1046.MirrorCS"),sQuery(id+"F0.wireOp",EDGE,"E1047.MirrorCS"),sQuery(id+"F0.wireOp",EDGE,"E1048.MirrorCS"),sQuery(id+"F0.wireOp",EDGE,"E1049.MirrorCS"),sQuery(id+"F0.wireOp",EDGE,"E1050.MirrorCS"),sQuery(id+"F0.wireOp",EDGE,"E1051.MirrorCS"),sQuery(id+"F0.wireOp",EDGE,"E1052.MirrorCS"),sQuery(id+"F0.wireOp",EDGE,"E1053.MirrorCS"),sQuery(id+"F0.wireOp",EDGE,"E1054.MirrorCS"),sQuery(id+"F0.wireOp",EDGE,"E1055.MirrorCS"),sQuery(id+"F0.wireOp",EDGE,"E1056.MirrorCS"),sQuery(id+"F0.wireOp",EDGE,"E1057.MirrorCS"),sQuery(id+"F0.wireOp",EDGE,"E1058.MirrorCS"),sQuery(id+"F0.wireOp",EDGE,"E1059.MirrorCS"),sQuery(id+"F0.wireOp",EDGE,"E1060.MirrorCS"),sQuery(id+"F0.wireOp",EDGE,"E1061.MirrorCS"),sQuery(id+"F0.wireOp",EDGE,"E1062.MirrorCS"),sQuery(id+"F0.wireOp",EDGE,"E1063.MirrorCS"),sQuery(id+"F0.wireOp",EDGE,"E1064.MirrorCS"),sQuery(id+"F0.wireOp",EDGE,"E1065.MirrorCS"),sQuery(id+"F0.wireOp",EDGE,"E1066.MirrorCS"),sQuery(id+"F0.wireOp",EDGE,"E1067.MirrorCS"),sQuery(id+"F0.wireOp",EDGE,"E1068.MirrorCS"),sQuery(id+"F0.wireOp",EDGE,"E1069.MirrorCS"),sQuery(id+"F0.wireOp",EDGE,"E1070.MirrorCS"),sQuery(id+"F0.wireOp",EDGE,"E1071.MirrorCS"),sQuery(id+"F0.wireOp",EDGE,"E1072.MirrorCS"),sQuery(id+"F0.wireOp",EDGE,"E1074.MirrorCS"),sQuery(id+"F0.wireOp",EDGE,"E1075.MirrorCS"),sQuery(id+"F0.wireOp",EDGE,"E1076.MirrorCS"),sQuery(id+"F0.wireOp",EDGE,"E1077.MirrorCS"),sQuery(id+"F0.wireOp",EDGE,"E1078.MirrorCS"),sQuery(id+"F0.wireOp",EDGE,"E1079.MirrorCS"),sQuery(id+"F0.wireOp",EDGE,"E1080.MirrorCS"),sQuery(id+"F0.wireOp",EDGE,"E1081.MirrorCS"),sQuery(id+"F0.wireOp",EDGE,"E1082.MirrorCS"),sQuery(id+"F0.wireOp",EDGE,"E1083.MirrorCS"),sQuery(id+"F0.wireOp",EDGE,"E1084.MirrorCS"),sQuery(id+"F0.wireOp",EDGE,"E1085.MirrorCS"),sQuery(id+"F0.wireOp",EDGE,"E1086.MirrorCS"),sQuery(id+"F0.wireOp",EDGE,"E1087.MirrorCS"),sQuery(id+"F0.wireOp",EDGE,"E1088.MirrorCS"),sQuery(id+"F0.wireOp",EDGE,"E1089.MirrorCS"),sQuery(id+"F0.wireOp",EDGE,"E1090.MirrorCS"),sQuery(id+"F0.wireOp",EDGE,"E1091.MirrorCS"),sQuery(id+"F0.wireOp",EDGE,"E1092.MirrorCS"),sQuery(id+"F0.wireOp",EDGE,"E1093.MirrorCS"),sQuery(id+"F0.wireOp",EDGE,"E1094.MirrorCS"),sQuery(id+"F0.wireOp",EDGE,"E1095.MirrorCS"),sQuery(id+"F0.wireOp",EDGE,"E1096.MirrorCS"),sQuery(id+"F0.wireOp",EDGE,"E1097.MirrorCS"),sQuery(id+"F0.wireOp",EDGE,"E1098.MirrorCS"),sQuery(id+"F0.wireOp",EDGE,"E1099.MirrorCS"),sQuery(id+"F0.wireOp",EDGE,"E1100.MirrorCS"),sQuery(id+"F0.wireOp",EDGE,"E1101.MirrorCS"),sQuery(id+"F0.wireOp",EDGE,"E1102.MirrorCS"),sQuery(id+"F0.wireOp",EDGE,"E1103.MirrorCS"),sQuery(id+"F0.wireOp",EDGE,"E1104.MirrorCS"),sQuery(id+"F0.wireOp",EDGE,"E1105.MirrorCS"),sQuery(id+"F0.wireOp",EDGE,"E1106.MirrorCS"),sQuery(id+"F0.wireOp",EDGE,"E1107.MirrorCS"),sQuery(id+"F0.wireOp",EDGE,"E1108.MirrorCS"),sQuery(id+"F0.wireOp",EDGE,"E1109.MirrorCS"),sQuery(id+"F0.wireOp",EDGE,"E1110.MirrorCS"),sQuery(id+"F0.wireOp",EDGE,"E1111.MirrorCS"),sQuery(id+"F0.wireOp",EDGE,"E1112.MirrorCS"),sQuery(id+"F0.wireOp",EDGE,"E1113.MirrorCS"),sQuery(id+"F0.wireOp",EDGE,"E1114.MirrorCS"),sQuery(id+"F0.wireOp",EDGE,"E1115.MirrorCS"),sQuery(id+"F0.wireOp",EDGE,"E1116.MirrorCS"),sQuery(id+"F0.wireOp",EDGE,"E1117.MirrorCS"),sQuery(id+"F0.wireOp",EDGE,"E1118.MirrorCS"),sQuery(id+"F0.wireOp",EDGE,"E1119.MirrorCS"),sQuery(id+"F0.wireOp",EDGE,"E1120.MirrorCS"),sQuery(id+"F0.wireOp",EDGE,"E1121.MirrorCS"),sQuery(id+"F0.wireOp",EDGE,"E1122.MirrorCS"),sQuery(id+"F0.wireOp",EDGE,"E1123.MirrorCS"),sQuery(id+"F0.wireOp",EDGE,"E1124.MirrorCS"),sQuery(id+"F0.wireOp",EDGE,"E1126.MirrorCS"),sQuery(id+"F0.wireOp",EDGE,"E1127.MirrorCS"),sQuery(id+"F0.wireOp",EDGE,"E1128.MirrorCS"),sQuery(id+"F0.wireOp",EDGE,"E1129.MirrorCS"),sQuery(id+"F0.wireOp",EDGE,"E1130.MirrorCS"),sQuery(id+"F0.wireOp",EDGE,"E1131.MirrorCS"),sQuery(id+"F0.wireOp",EDGE,"E1132.MirrorCS"),sQuery(id+"F0.wireOp",EDGE,"E1133.MirrorCS"),sQuery(id+"F0.wireOp",EDGE,"E1134.MirrorCS"),sQuery(id+"F0.wireOp",EDGE,"E1135.MirrorCS"),sQuery(id+"F0.wireOp",EDGE,"E1136.MirrorCS"),sQuery(id+"F0.wireOp",EDGE,"E1137.MirrorCS"),sQuery(id+"F0.wireOp",EDGE,"E1138.MirrorCS"),sQuery(id+"F0.wireOp",EDGE,"E1139.MirrorCS"),sQuery(id+"F0.wireOp",EDGE,"E1140.MirrorCS"),sQuery(id+"F0.wireOp",EDGE,"E1141.MirrorCS"),sQuery(id+"F0.wireOp",EDGE,"E1142.MirrorCS"),sQuery(id+"F0.wireOp",EDGE,"E1143.MirrorCS"),sQuery(id+"F0.wireOp",EDGE,"E1144.MirrorCS"),sQuery(id+"F0.wireOp",EDGE,"E1145.MirrorCS"),sQuery(id+"F0.wireOp",EDGE,"E1146.MirrorCS"),sQuery(id+"F0.wireOp",EDGE,"E1147.MirrorCS"),sQuery(id+"F0.wireOp",EDGE,"E1148.MirrorCS"),sQuery(id+"F0.wireOp",EDGE,"E1149.MirrorCS"),sQuery(id+"F0.wireOp",EDGE,"E1150.MirrorCS"),sQuery(id+"F0.wireOp",EDGE,"E1151.MirrorCS"),sQuery(id+"F0.wireOp",EDGE,"E1152.MirrorCS"),sQuery(id+"F0.wireOp",EDGE,"E1153.MirrorCS"),sQuery(id+"F0.wireOp",EDGE,"E1154.MirrorCS"),sQuery(id+"F0.wireOp",EDGE,"E1155.MirrorCS"),sQuery(id+"F0.wireOp",EDGE,"E1156.MirrorCS"),sQuery(id+"F0.wireOp",EDGE,"E1157.MirrorCS"),sQuery(id+"F0.wireOp",EDGE,"E1158.MirrorCS"),sQuery(id+"F0.wireOp",EDGE,"E1159.MirrorCS"),sQuery(id+"F0.wireOp",EDGE,"E1160.MirrorCS"),sQuery(id+"F0.wireOp",EDGE,"E1161.MirrorCS"),sQuery(id+"F0.wireOp",EDGE,"E1162.MirrorCS"),sQuery(id+"F0.wireOp",EDGE,"E1163.MirrorCS"),sQuery(id+"F0.wireOp",EDGE,"E1164.MirrorCS"),sQuery(id+"F0.wireOp",EDGE,"E1165.MirrorCS"),sQuery(id+"F0.wireOp",EDGE,"E1166.MirrorCS"),sQuery(id+"F0.wireOp",EDGE,"E1167.MirrorCS"),sQuery(id+"F0.wireOp",EDGE,"E1168.MirrorCS"),sQuery(id+"F0.wireOp",EDGE,"E1169.MirrorCS"),sQuery(id+"F0.wireOp",EDGE,"E1170.MirrorCS"),sQuery(id+"F0.wireOp",EDGE,"E1171.MirrorCS"),sQuery(id+"F0.wireOp",EDGE,"E1172.MirrorCS"),sQuery(id+"F0.wireOp",EDGE,"E1173.MirrorCS"),sQuery(id+"F0.wireOp",EDGE,"E1174.MirrorCS"),sQuery(id+"F0.wireOp",EDGE,"E1175.MirrorCS"),sQuery(id+"F0.wireOp",EDGE,"E1176.MirrorCS"),sQuery(id+"F0.wireOp",EDGE,"E1177.MirrorCS"),sQuery(id+"F0.wireOp",EDGE,"E1178.MirrorCS"),sQuery(id+"F0.wireOp",EDGE,"E1179.MirrorCS"),sQuery(id+"F0.wireOp",EDGE,"E1180.MirrorCS"),sQuery(id+"F0.wireOp",EDGE,"E1181.MirrorCS"),sQuery(id+"F0.wireOp",EDGE,"E1182.MirrorCS"),sQuery(id+"F0.wireOp",EDGE,"E1183.MirrorCS"),sQuery(id+"F0.wireOp",EDGE,"E1184.MirrorCS"),sQuery(id+"F0.wireOp",EDGE,"E1185.MirrorCS"),sQuery(id+"F0.wireOp",EDGE,"E1186.MirrorCS"),sQuery(id+"F0.wireOp",EDGE,"E1187.MirrorCS"),sQuery(id+"F0.wireOp",EDGE,"E1188.MirrorCS"),sQuery(id+"F0.wireOp",EDGE,"E1189.MirrorCS"),sQuery(id+"F0.wireOp",EDGE,"E1190.MirrorCS"),sQuery(id+"F0.wireOp",EDGE,"E1191.MirrorCS"),sQuery(id+"F0.wireOp",EDGE,"E1192.MirrorCS"),sQuery(id+"F0.wireOp",EDGE,"E1193.MirrorCS"),sQuery(id+"F0.wireOp",EDGE,"E1194.MirrorCS"),sQuery(id+"F0.wireOp",EDGE,"E1196.MirrorCS"),sQuery(id+"F0.wireOp",EDGE,"E1197.MirrorCS"),sQuery(id+"F0.wireOp",EDGE,"E1198.MirrorCS"),sQuery(id+"F0.wireOp",EDGE,"E1199.MirrorCS"),sQuery(id+"F0.wireOp",EDGE,"E1200.MirrorCS"),sQuery(id+"F0.wireOp",EDGE,"E1201.MirrorCS"),sQuery(id+"F0.wireOp",EDGE,"E1202.MirrorCS"),sQuery(id+"F0.wireOp",EDGE,"E1203.MirrorCS"),sQuery(id+"F0.wireOp",EDGE,"E1204.MirrorCS"),sQuery(id+"F0.wireOp",EDGE,"E1205.MirrorCS"),sQuery(id+"F0.wireOp",EDGE,"E1206.MirrorCS"),sQuery(id+"F0.wireOp",EDGE,"E1207.MirrorCS"),sQuery(id+"F0.wireOp",EDGE,"E1208.MirrorCS"),sQuery(id+"F0.wireOp",EDGE,"E1209.MirrorCS"),sQuery(id+"F0.wireOp",EDGE,"E1210.MirrorCS"),sQuery(id+"F0.wireOp",EDGE,"E1211.MirrorCS"),sQuery(id+"F0.wireOp",EDGE,"E1212.MirrorCS"),sQuery(id+"F0.wireOp",EDGE,"E1213.MirrorCS"),sQuery(id+"F0.wireOp",EDGE,"E1214.MirrorCS"),sQuery(id+"F0.wireOp",EDGE,"E1215.MirrorCS"),sQuery(id+"F0.wireOp",EDGE,"E1216.MirrorCS"),sQuery(id+"F0.wireOp",EDGE,"E1217.MirrorCS"),sQuery(id+"F0.wireOp",EDGE,"E1218.MirrorCS"),sQuery(id+"F0.wireOp",EDGE,"E1219.MirrorCS"),sQuery(id+"F0.wireOp",EDGE,"E1220.MirrorCS"),sQuery(id+"F0.wireOp",EDGE,"E1221.MirrorCS"),sQuery(id+"F0.wireOp",EDGE,"E1222.MirrorCS"),sQuery(id+"F0.wireOp",EDGE,"E1223.MirrorCS"),sQuery(id+"F0.wireOp",EDGE,"E1224.MirrorCS"),sQuery(id+"F0.wireOp",EDGE,"E1225.MirrorCS"),sQuery(id+"F0.wireOp",EDGE,"E1226.MirrorCS"),sQuery(id+"F0.wireOp",EDGE,"E1227.MirrorCS"),sQuery(id+"F0.wireOp",EDGE,"E1228.MirrorCS"),sQuery(id+"F0.wireOp",EDGE,"E1229.MirrorCS"),sQuery(id+"F0.wireOp",EDGE,"E1230.MirrorCS"),sQuery(id+"F0.wireOp",EDGE,"E1231.MirrorCS"),sQuery(id+"F0.wireOp",EDGE,"E1232.MirrorCS"),sQuery(id+"F0.wireOp",EDGE,"E1233.MirrorCS"),sQuery(id+"F0.wireOp",EDGE,"E1234.MirrorCS"),sQuery(id+"F0.wireOp",EDGE,"E1235.MirrorCS"),sQuery(id+"F0.wireOp",EDGE,"E1236.MirrorCS"),sQuery(id+"F0.wireOp",EDGE,"E1237.MirrorCS"),sQuery(id+"F0.wireOp",EDGE,"E1238.MirrorCS"),sQuery(id+"F0.wireOp",EDGE,"E1239.MirrorCS"),sQuery(id+"F0.wireOp",EDGE,"E1240.MirrorCS"),sQuery(id+"F0.wireOp",EDGE,"E1241.MirrorCS"),sQuery(id+"F0.wireOp",EDGE,"E1242.MirrorCS"),sQuery(id+"F0.wireOp",EDGE,"E1243.MirrorCS"),sQuery(id+"F0.wireOp",EDGE,"E1244.MirrorCS"),sQuery(id+"F0.wireOp",EDGE,"E1245.MirrorCS"),sQuery(id+"F0.wireOp",EDGE,"E1246.MirrorCS"),sQuery(id+"F0.wireOp",EDGE,"E1247.MirrorCS"),sQuery(id+"F0.wireOp",EDGE,"E1249.MirrorCS"),sQuery(id+"F0.wireOp",EDGE,"E1250.MirrorCS"),sQuery(id+"F0.wireOp",EDGE,"E1251.MirrorCS"),sQuery(id+"F0.wireOp",EDGE,"E1252.MirrorCS"),sQuery(id+"F0.wireOp",EDGE,"E1253.MirrorCS"),sQuery(id+"F0.wireOp",EDGE,"E1254.MirrorCS"),sQuery(id+"F0.wireOp",EDGE,"E1255.MirrorCS"),sQuery(id+"F0.wireOp",EDGE,"E1257.MirrorCS"),sQuery(id+"F0.wireOp",EDGE,"E1258.MirrorCS"),sQuery(id+"F0.wireOp",EDGE,"E1259.MirrorCS"),sQuery(id+"F0.wireOp",EDGE,"E1260.MirrorCS"),sQuery(id+"F0.wireOp",EDGE,"E1261.MirrorCS"),sQuery(id+"F0.wireOp",EDGE,"E1262.MirrorCS"),sQuery(id+"F0.wireOp",EDGE,"E1263.MirrorCS"),sQuery(id+"F0.wireOp",EDGE,"E1264.MirrorCS"),sQuery(id+"F0.wireOp",EDGE,"E1265.MirrorCS"),sQuery(id+"F0.wireOp",EDGE,"E1266.MirrorCS"),sQuery(id+"F0.wireOp",EDGE,"E1267.MirrorCS"),sQuery(id+"F0.wireOp",EDGE,"E1268.MirrorCS"),sQuery(id+"F0.wireOp",EDGE,"E1269.MirrorCS"),sQuery(id+"F0.wireOp",EDGE,"E1270.MirrorCS"),sQuery(id+"F0.wireOp",EDGE,"E1271.MirrorCS"),sQuery(id+"F0.wireOp",EDGE,"E1272.MirrorCS"),sQuery(id+"F0.wireOp",EDGE,"E1273.MirrorCS"),sQuery(id+"F0.wireOp",EDGE,"E1274.MirrorCS"),sQuery(id+"F0.wireOp",EDGE,"E1275.MirrorCS"),sQuery(id+"F0.wireOp",EDGE,"E1276.MirrorCS"),sQuery(id+"F0.wireOp",EDGE,"E1277.MirrorCS"),sQuery(id+"F0.wireOp",EDGE,"E1278.MirrorCS"),sQuery(id+"F0.wireOp",EDGE,"E1279.MirrorCS"),sQuery(id+"F0.wireOp",EDGE,"E1280.MirrorCS"),sQuery(id+"F0.wireOp",EDGE,"E1281.MirrorCS"),sQuery(id+"F0.wireOp",EDGE,"E1282.MirrorCS"),sQuery(id+"F0.wireOp",EDGE,"E1283.MirrorCS"),sQuery(id+"F0.wireOp",EDGE,"E1284.MirrorCS"),sQuery(id+"F0.wireOp",EDGE,"E1285.MirrorCS"),sQuery(id+"F0.wireOp",EDGE,"E1286.MirrorCS"),sQuery(id+"F0.wireOp",EDGE,"E1287.MirrorCS"),sQuery(id+"F0.wireOp",EDGE,"E1288.MirrorCS"),sQuery(id+"F0.wireOp",EDGE,"E1289.MirrorCS"),sQuery(id+"F0.wireOp",EDGE,"E1290.MirrorCS"),sQuery(id+"F0.wireOp",EDGE,"E1291.MirrorCS"),sQuery(id+"F0.wireOp",EDGE,"E1292.MirrorCS"),sQuery(id+"F0.wireOp",EDGE,"E1293.MirrorCS"),sQuery(id+"F0.wireOp",EDGE,"E1294.MirrorCS"),sQuery(id+"F0.wireOp",EDGE,"E1295.MirrorCS"),sQuery(id+"F0.wireOp",EDGE,"E1296.MirrorCS"),sQuery(id+"F0.wireOp",EDGE,"E1297.MirrorCS"),sQuery(id+"F0.wireOp",EDGE,"E1298.MirrorCS"),sQuery(id+"F0.wireOp",EDGE,"E1299.MirrorCS"),sQuery(id+"F0.wireOp",EDGE,"E1300.MirrorCS"),sQuery(id+"F0.wireOp",EDGE,"E1301.MirrorCS"),sQuery(id+"F0.wireOp",EDGE,"E1302.MirrorCS"),sQuery(id+"F0.wireOp",EDGE,"E1303.MirrorCS"),sQuery(id+"F0.wireOp",EDGE,"E1304.MirrorCS"),sQuery(id+"F0.wireOp",EDGE,"E1305.MirrorCS"),sQuery(id+"F0.wireOp",EDGE,"E1306.MirrorCS"),sQuery(id+"F0.wireOp",EDGE,"E1307.MirrorCS"),sQuery(id+"F0.wireOp",EDGE,"E1308.MirrorCS"),sQuery(id+"F0.wireOp",EDGE,"E1309.MirrorCS"),sQuery(id+"F0.wireOp",EDGE,"E1310.MirrorCS"),sQuery(id+"F0.wireOp",EDGE,"E1311.MirrorCS"),sQuery(id+"F0.wireOp",EDGE,"E1312.MirrorCS"),sQuery(id+"F0.wireOp",EDGE,"E1313.MirrorCS"),sQuery(id+"F0.wireOp",EDGE,"E1314.MirrorCS"),sQuery(id+"F0.wireOp",EDGE,"E1315.MirrorCS"),sQuery(id+"F0.wireOp",EDGE,"E1316.MirrorCS"),sQuery(id+"F0.wireOp",EDGE,"E1317.MirrorCS"),sQuery(id+"F0.wireOp",EDGE,"E1318.MirrorCS"),sQuery(id+"F0.wireOp",EDGE,"E1319.MirrorCS"),sQuery(id+"F0.wireOp",EDGE,"E1320.MirrorCS"),sQuery(id+"F0.wireOp",EDGE,"E1321.MirrorCS"),sQuery(id+"F0.wireOp",EDGE,"E1322.MirrorCS"),sQuery(id+"F0.wireOp",EDGE,"E1323.MirrorCS"),sQuery(id+"F0.wireOp",EDGE,"E1324.MirrorCS"),sQuery(id+"F0.wireOp",EDGE,"E1325.MirrorCS"),sQuery(id+"F0.wireOp",EDGE,"E1326.MirrorCS"),sQuery(id+"F0.wireOp",EDGE,"E1327.MirrorCS"),sQuery(id+"F0.wireOp",EDGE,"E1328.MirrorCS"),sQuery(id+"F0.wireOp",EDGE,"E1329.MirrorCS"),sQuery(id+"F0.wireOp",EDGE,"E1330.MirrorCS"),sQuery(id+"F0.wireOp",EDGE,"E1331.MirrorCS"),sQuery(id+"F0.wireOp",EDGE,"E1332.MirrorCS"),sQuery(id+"F0.wireOp",EDGE,"E1333.MirrorCS"),sQuery(id+"F0.wireOp",EDGE,"E1334.MirrorCS"),sQuery(id+"F0.wireOp",EDGE,"E1335.MirrorCS"),sQuery(id+"F0.wireOp",EDGE,"E1336.MirrorCS"),sQuery(id+"F0.wireOp",EDGE,"E1337.MirrorCS"),sQuery(id+"F0.wireOp",EDGE,"E1338.MirrorCS"),sQuery(id+"F0.wireOp",EDGE,"E1339.MirrorCS"),sQuery(id+"F0.wireOp",EDGE,"E1340.MirrorCS"),sQuery(id+"F0.wireOp",EDGE,"E1341.MirrorCS"),sQuery(id+"F0.wireOp",EDGE,"E1342.MirrorCS"),sQuery(id+"F0.wireOp",EDGE,"E1343.MirrorCS"),sQuery(id+"F0.wireOp",EDGE,"E1344.MirrorCS"),sQuery(id+"F0.wireOp",EDGE,"E1345.MirrorCS"),sQuery(id+"F0.wireOp",EDGE,"E1346.MirrorCS"),sQuery(id+"F0.wireOp",EDGE,"E1347.MirrorCS"),sQuery(id+"F0.wireOp",EDGE,"E1348.MirrorCS"),sQuery(id+"F0.wireOp",EDGE,"E1349.MirrorCS"),sQuery(id+"F0.wireOp",EDGE,"E1350.MirrorCS"),sQuery(id+"F0.wireOp",EDGE,"E1351.MirrorCS"),sQuery(id+"F0.wireOp",EDGE,"E1352.MirrorCS"),sQuery(id+"F0.wireOp",EDGE,"E1353.MirrorCS"),sQuery(id+"F0.wireOp",EDGE,"E1354.MirrorCS"),sQuery(id+"F0.wireOp",EDGE,"E1355.MirrorCS"),sQuery(id+"F0.wireOp",EDGE,"E1356.MirrorCS"),sQuery(id+"F0.wireOp",EDGE,"E1357.MirrorCS"),sQuery(id+"F0.wireOp",EDGE,"E1358.MirrorCS"),sQuery(id+"F0.wireOp",EDGE,"E1359.MirrorCS"),sQuery(id+"F0.wireOp",EDGE,"E1360.MirrorCS"),sQuery(id+"F0.wireOp",EDGE,"E1361.MirrorCS"),sQuery(id+"F0.wireOp",EDGE,"E1362.MirrorCS"),sQuery(id+"F0.wireOp",EDGE,"E1363.MirrorCS"),sQuery(id+"F0.wireOp",EDGE,"E1364.MirrorCS"),sQuery(id+"F0.wireOp",EDGE,"E1365.MirrorCS"),sQuery(id+"F0.wireOp",EDGE,"E1366.MirrorCS"),sQuery(id+"F0.wireOp",EDGE,"E1367.MirrorCS"),sQuery(id+"F0.wireOp",EDGE,"E96.MirrorCS"),sQuery(id+"F0.wireOp",EDGE,"E1368"),sQuery(id+"F0.wireOp",EDGE,"E1369"),sQuery(id+"F0.wireOp",EDGE,"E1370"),sQuery(id+"F0.wireOp",EDGE,"E1372.1"),sQuery(id+"F0.wireOp",EDGE,"E1372.3"),sQuery(id+"F0.wireOp",EDGE,"E1373"),sQuery(id+"F0.wireOp",EDGE,"E1374.trimOffspring"),sQuery(id+"F0.wireOp",EDGE,"E1375.trimOffspring"),sQuery(id+"F0.wireOp",EDGE,"E1195.MirrorCS"),sQuery(id+"F0.wireOp",EDGE,"E1376.trimOffspring"),sQuery(id+"F0.wireOp",EDGE,"E1377.trimOffspring"),sQuery(id+"F0.wireOp",EDGE,"E1378.trimOffspring"),sQuery(id+"F0.wireOp",EDGE,"E780.MirrorCS"),sQuery(id+"F0.wireOp",EDGE,"E1379.trimOffspring"),sQuery(id+"F0.wireOp",EDGE,"E1380.trimOffspring"),sQuery(id+"F0.wireOp",EDGE,"E1381.trimOffspring"),sQuery(id+"F0.wireOp",EDGE,"E343.MirrorCS"),sQuery(id+"F0.wireOp",EDGE,"E1382.trimOffspring"),sQuery(id+"F0.wireOp",EDGE,"E1383.trimOffspring"),sQuery(id+"F0.wireOp",EDGE,"E1384.trimOffspring"),sQuery(id+"F0.wireOp",EDGE,"E202.MirrorCS"),sQuery(id+"F0.wireOp",EDGE,"E1385.trimOffspring"),sQuery(id+"F0.wireOp",EDGE,"E284.MirrorCS"),sQuery(id+"F0.wireOp",EDGE,"E1386.trimOffspring"),sQuery(id+"F0.wireOp",EDGE,"E1387.trimOffspring"),sQuery(id+"F0.wireOp",EDGE,"E1388.trimOffspring"),sQuery(id+"F0.wireOp",EDGE,"E759.MirrorCS"),sQuery(id+"F0.wireOp",EDGE,"E1389.trimOffspring"),sQuery(id+"F0.wireOp",EDGE,"E1248.MirrorCS"),sQuery(id+"F0.wireOp",EDGE,"E1390.trimOffspring")])]});
            hole(context, id + "F2", {"style" : HoleStyle.SIMPLE, "endStyle" : HoleEndStyle.THROUGH, "oppositeDirection" : true, "holeDiameter" : 0.05 * mm, "majorDiameter" : 5 * mm, "isTappedThrough" : true, "tappedDepth" : 12 * mm, "tapClearance" : 3, "startFromSketch" : true, "locations" : qUnion([Q0, Q1, Q2]), "scope" : qUnion([Q3])});
        }
    });
